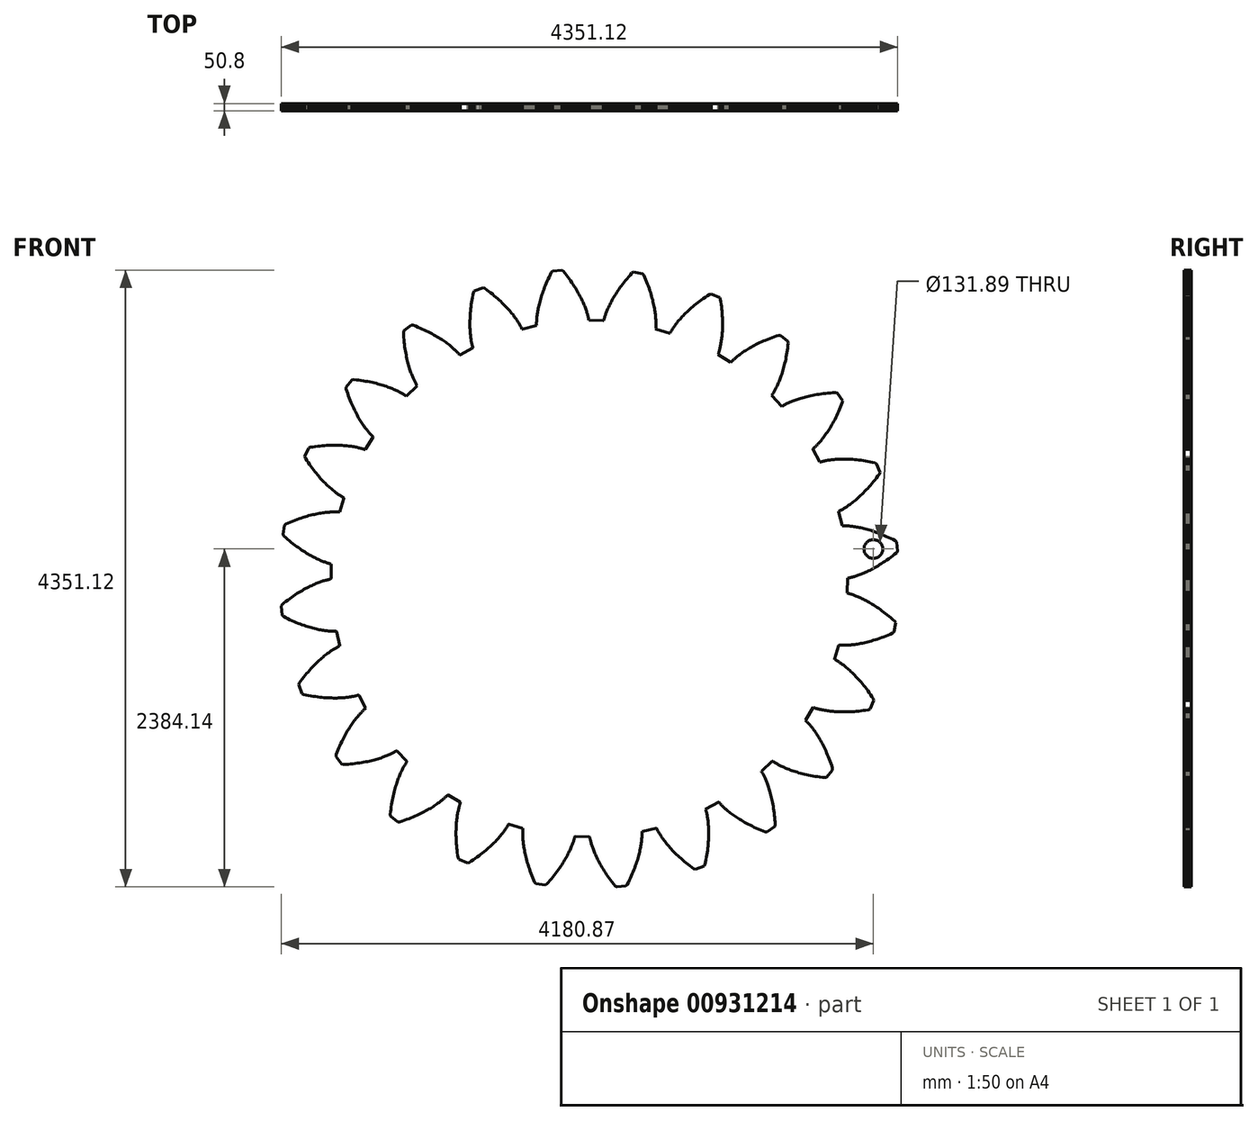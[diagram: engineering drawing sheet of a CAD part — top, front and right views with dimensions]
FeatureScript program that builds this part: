
annotation { "Feature Type Name" : "Feature", "Feature Type Description" : "" }
export const myFeature = defineFeature(function(context is Context, id is Id, definition is map)
    precondition{}
    {
        {
            var Q0;
            Q0=qCreatedBy(makeId("Front.planeOp"),FACE);
            var sketch = newSketch(context, id + "F0", { "sketchPlane" : qUnion([Q0])});
            skLineSegment(sketch, "E0", {"start": v(1823.53, 3.17) * mm, "end": v(1822.91, 0) * mm});
            skLineSegment(sketch, "E1", {"start": v(1822.91, 0) * mm, "end": v(1820.2, -99.34) * mm});
            skLineSegment(sketch, "E2", {"start": v(1820.2, -99.34) * mm, "end": v(1820.65, -102.54) * mm});
            skLineSegment(sketch, "E3", {"start": v(1820.65, -102.54) * mm, "end": v(1825.27, -103.65) * mm});
            skLineSegment(sketch, "E4", {"start": v(1825.27, -103.65) * mm, "end": v(1830.24, -104.93) * mm});
            skLineSegment(sketch, "E5", {"start": v(1830.24, -104.93) * mm, "end": v(1835.55, -106.37) * mm});
            skLineSegment(sketch, "E6", {"start": v(1835.55, -106.37) * mm, "end": v(1841.22, -108) * mm});
            skLineSegment(sketch, "E7", {"start": v(1841.22, -108) * mm, "end": v(1847.22, -109.82) * mm});
            skLineSegment(sketch, "E8", {"start": v(1847.22, -109.82) * mm, "end": v(1853.55, -111.84) * mm});
            skLineSegment(sketch, "E9", {"start": v(1853.55, -111.84) * mm, "end": v(1860.22, -114.08) * mm});
            skLineSegment(sketch, "E10", {"start": v(1860.22, -114.08) * mm, "end": v(1867.2, -116.54) * mm});
            skLineSegment(sketch, "E11", {"start": v(1867.2, -116.54) * mm, "end": v(1874.52, -119.23) * mm});
            skLineSegment(sketch, "E12", {"start": v(1874.52, -119.23) * mm, "end": v(1882.14, -122.16) * mm});
            skLineSegment(sketch, "E13", {"start": v(1882.14, -122.16) * mm, "end": v(1890.08, -125.35) * mm});
            skLineSegment(sketch, "E14", {"start": v(1890.08, -125.35) * mm, "end": v(1898.31, -128.8) * mm});
            skLineSegment(sketch, "E15", {"start": v(1898.31, -128.8) * mm, "end": v(1906.85, -132.52) * mm});
            skLineSegment(sketch, "E16", {"start": v(1906.85, -132.52) * mm, "end": v(1915.67, -136.52) * mm});
            skLineSegment(sketch, "E17", {"start": v(1915.67, -136.52) * mm, "end": v(1924.79, -140.8) * mm});
            skLineSegment(sketch, "E18", {"start": v(1924.79, -140.8) * mm, "end": v(1934.17, -145.4) * mm});
            skLineSegment(sketch, "E19", {"start": v(1934.17, -145.4) * mm, "end": v(1943.83, -150.29) * mm});
            skLineSegment(sketch, "E20", {"start": v(1943.83, -150.29) * mm, "end": v(1953.76, -155.5) * mm});
            skLineSegment(sketch, "E21", {"start": v(1953.76, -155.5) * mm, "end": v(1963.94, -161.04) * mm});
            skLineSegment(sketch, "E22", {"start": v(1963.94, -161.04) * mm, "end": v(1974.37, -166.91) * mm});
            skLineSegment(sketch, "E23", {"start": v(1974.37, -166.91) * mm, "end": v(1985.04, -173.12) * mm});
            skLineSegment(sketch, "E24", {"start": v(1985.04, -173.12) * mm, "end": v(1995.95, -179.69) * mm});
            skLineSegment(sketch, "E25", {"start": v(1995.95, -179.69) * mm, "end": v(2007.08, -186.61) * mm});
            skLineSegment(sketch, "E26", {"start": v(2007.08, -186.61) * mm, "end": v(2018.44, -193.9) * mm});
            skLineSegment(sketch, "E27", {"start": v(2018.44, -193.9) * mm, "end": v(2030, -201.57) * mm});
            skLineSegment(sketch, "E28", {"start": v(2030, -201.57) * mm, "end": v(2041.76, -209.61) * mm});
            skLineSegment(sketch, "E29", {"start": v(2041.76, -209.61) * mm, "end": v(2053.71, -218.05) * mm});
            skLineSegment(sketch, "E30", {"start": v(2053.71, -218.05) * mm, "end": v(2065.85, -226.88) * mm});
            skLineSegment(sketch, "E31", {"start": v(2065.85, -226.88) * mm, "end": v(2078.16, -236.11) * mm});
            skLineSegment(sketch, "E32", {"start": v(2078.16, -236.11) * mm, "end": v(2090.63, -245.76) * mm});
            skLineSegment(sketch, "E33", {"start": v(2090.63, -245.76) * mm, "end": v(2103.27, -255.82) * mm});
            skLineSegment(sketch, "E34", {"start": v(2103.27, -255.82) * mm, "end": v(2116.04, -266.3) * mm});
            skLineSegment(sketch, "E35", {"start": v(2116.04, -266.3) * mm, "end": v(2128.96, -277.23) * mm});
            skLineSegment(sketch, "E36", {"start": v(2128.96, -277.23) * mm, "end": v(2142, -288.58) * mm});
            skLineSegment(sketch, "E37", {"start": v(2142, -288.58) * mm, "end": v(2155.16, -300.37) * mm});
            skLineSegment(sketch, "E38", {"start": v(2155.16, -300.37) * mm, "end": v(2161.79, -311.66) * mm});
            skLineSegment(sketch, "E39", {"start": v(2161.79, -311.66) * mm, "end": v(2151.48, -376.27) * mm});
            skLineSegment(sketch, "E40", {"start": v(2151.48, -376.27) * mm, "end": v(2141.67, -384.94) * mm});
            skLineSegment(sketch, "E41", {"start": v(2141.67, -384.94) * mm, "end": v(2125.5, -392.05) * mm});
            skLineSegment(sketch, "E42", {"start": v(2125.5, -392.05) * mm, "end": v(2109.57, -398.79) * mm});
            skLineSegment(sketch, "E43", {"start": v(2109.57, -398.79) * mm, "end": v(2093.9, -405.14) * mm});
            skLineSegment(sketch, "E44", {"start": v(2093.9, -405.14) * mm, "end": v(2078.5, -411.14) * mm});
            skLineSegment(sketch, "E45", {"start": v(2078.5, -411.14) * mm, "end": v(2063.36, -416.77) * mm});
            skLineSegment(sketch, "E46", {"start": v(2063.36, -416.77) * mm, "end": v(2048.5, -422.06) * mm});
            skLineSegment(sketch, "E47", {"start": v(2048.5, -422.06) * mm, "end": v(2033.93, -427) * mm});
            skLineSegment(sketch, "E48", {"start": v(2033.93, -427) * mm, "end": v(2019.65, -431.62) * mm});
            skLineSegment(sketch, "E49", {"start": v(2019.65, -431.62) * mm, "end": v(2005.66, -435.92) * mm});
            skLineSegment(sketch, "E50", {"start": v(2005.66, -435.92) * mm, "end": v(1991.98, -439.9) * mm});
            skLineSegment(sketch, "E51", {"start": v(1991.98, -439.9) * mm, "end": v(1978.61, -443.6) * mm});
            skLineSegment(sketch, "E52", {"start": v(1978.61, -443.6) * mm, "end": v(1965.56, -447) * mm});
            skLineSegment(sketch, "E53", {"start": v(1965.56, -447) * mm, "end": v(1952.82, -450.1) * mm});
            skLineSegment(sketch, "E54", {"start": v(1952.82, -450.1) * mm, "end": v(1940.41, -452.96) * mm});
            skLineSegment(sketch, "E55", {"start": v(1940.41, -452.96) * mm, "end": v(1928.34, -455.54) * mm});
            skLineSegment(sketch, "E56", {"start": v(1928.34, -455.54) * mm, "end": v(1916.6, -457.88) * mm});
            skLineSegment(sketch, "E57", {"start": v(1916.6, -457.88) * mm, "end": v(1905.2, -459.97) * mm});
            skLineSegment(sketch, "E58", {"start": v(1905.2, -459.97) * mm, "end": v(1894.14, -461.84) * mm});
            skLineSegment(sketch, "E59", {"start": v(1894.14, -461.84) * mm, "end": v(1883.44, -463.49) * mm});
            skLineSegment(sketch, "E60", {"start": v(1883.44, -463.49) * mm, "end": v(1873.1, -464.93) * mm});
            skLineSegment(sketch, "E61", {"start": v(1873.1, -464.93) * mm, "end": v(1863.1, -466.17) * mm});
            skLineSegment(sketch, "E62", {"start": v(1863.1, -466.17) * mm, "end": v(1853.46, -467.22) * mm});
            skLineSegment(sketch, "E63", {"start": v(1853.46, -467.22) * mm, "end": v(1844.2, -468.1) * mm});
            skLineSegment(sketch, "E64", {"start": v(1844.2, -468.1) * mm, "end": v(1835.3, -468.82) * mm});
            skLineSegment(sketch, "E65", {"start": v(1835.3, -468.82) * mm, "end": v(1826.76, -469.38) * mm});
            skLineSegment(sketch, "E66", {"start": v(1826.76, -469.38) * mm, "end": v(1818.6, -469.8) * mm});
            skLineSegment(sketch, "E67", {"start": v(1818.6, -469.8) * mm, "end": v(1810.82, -470.08) * mm});
            skLineSegment(sketch, "E68", {"start": v(1810.82, -470.08) * mm, "end": v(1803.41, -470.24) * mm});
            skLineSegment(sketch, "E69", {"start": v(1803.41, -470.24) * mm, "end": v(1796.38, -470.3) * mm});
            skLineSegment(sketch, "E70", {"start": v(1796.38, -470.3) * mm, "end": v(1789.73, -470.24) * mm});
            skLineSegment(sketch, "E71", {"start": v(1789.73, -470.24) * mm, "end": v(1783.46, -470.1) * mm});
            skLineSegment(sketch, "E72", {"start": v(1783.46, -470.1) * mm, "end": v(1777.58, -469.9) * mm});
            skLineSegment(sketch, "E73", {"start": v(1777.58, -469.9) * mm, "end": v(1772.07, -469.61) * mm});
            skLineSegment(sketch, "E74", {"start": v(1772.07, -469.61) * mm, "end": v(1766.95, -469.28) * mm});
            skLineSegment(sketch, "E75", {"start": v(1766.95, -469.28) * mm, "end": v(1762.22, -468.9) * mm});
            skLineSegment(sketch, "E76", {"start": v(1762.22, -468.9) * mm, "end": v(1760.8, -471.8) * mm});
            skLineSegment(sketch, "E77", {"start": v(1760.8, -471.8) * mm, "end": v(1732.47, -567.06) * mm});
            skLineSegment(sketch, "E78", {"start": v(1732.47, -567.06) * mm, "end": v(1732.07, -570.26) * mm});
            skLineSegment(sketch, "E79", {"start": v(1732.07, -570.26) * mm, "end": v(1736.25, -572.54) * mm});
            skLineSegment(sketch, "E80", {"start": v(1736.25, -572.54) * mm, "end": v(1740.72, -575.05) * mm});
            skLineSegment(sketch, "E81", {"start": v(1740.72, -575.05) * mm, "end": v(1745.48, -577.82) * mm});
            skLineSegment(sketch, "E82", {"start": v(1745.48, -577.82) * mm, "end": v(1750.52, -580.86) * mm});
            skLineSegment(sketch, "E83", {"start": v(1750.52, -580.86) * mm, "end": v(1755.85, -584.17) * mm});
            skLineSegment(sketch, "E84", {"start": v(1755.85, -584.17) * mm, "end": v(1761.44, -587.77) * mm});
            skLineSegment(sketch, "E85", {"start": v(1761.44, -587.77) * mm, "end": v(1767.3, -591.65) * mm});
            skLineSegment(sketch, "E86", {"start": v(1767.3, -591.65) * mm, "end": v(1773.42, -595.84) * mm});
            skLineSegment(sketch, "E87", {"start": v(1773.42, -595.84) * mm, "end": v(1779.78, -600.33) * mm});
            skLineSegment(sketch, "E88", {"start": v(1779.78, -600.33) * mm, "end": v(1786.4, -605.13) * mm});
            skLineSegment(sketch, "E89", {"start": v(1786.4, -605.13) * mm, "end": v(1793.23, -610.27) * mm});
            skLineSegment(sketch, "E90", {"start": v(1793.23, -610.27) * mm, "end": v(1800.3, -615.73) * mm});
            skLineSegment(sketch, "E91", {"start": v(1800.3, -615.73) * mm, "end": v(1807.58, -621.53) * mm});
            skLineSegment(sketch, "E92", {"start": v(1807.58, -621.53) * mm, "end": v(1815.07, -627.68) * mm});
            skLineSegment(sketch, "E93", {"start": v(1815.07, -627.68) * mm, "end": v(1822.76, -634.18) * mm});
            skLineSegment(sketch, "E94", {"start": v(1822.76, -634.18) * mm, "end": v(1830.64, -641.04) * mm});
            skLineSegment(sketch, "E95", {"start": v(1830.64, -641.04) * mm, "end": v(1838.7, -648.27) * mm});
            skLineSegment(sketch, "E96", {"start": v(1838.7, -648.27) * mm, "end": v(1846.94, -655.87) * mm});
            skLineSegment(sketch, "E97", {"start": v(1846.94, -655.87) * mm, "end": v(1855.34, -663.86) * mm});
            skLineSegment(sketch, "E98", {"start": v(1855.34, -663.86) * mm, "end": v(1863.9, -672.23) * mm});
            skLineSegment(sketch, "E99", {"start": v(1863.9, -672.23) * mm, "end": v(1872.6, -681) * mm});
            skLineSegment(sketch, "E100", {"start": v(1872.6, -681) * mm, "end": v(1881.43, -690.16) * mm});
            skLineSegment(sketch, "E101", {"start": v(1881.43, -690.16) * mm, "end": v(1890.4, -699.73) * mm});
            skLineSegment(sketch, "E102", {"start": v(1890.4, -699.73) * mm, "end": v(1899.47, -709.7) * mm});
            skLineSegment(sketch, "E103", {"start": v(1899.47, -709.7) * mm, "end": v(1908.66, -720.1) * mm});
            skLineSegment(sketch, "E104", {"start": v(1908.66, -720.1) * mm, "end": v(1917.93, -730.91) * mm});
            skLineSegment(sketch, "E105", {"start": v(1917.93, -730.91) * mm, "end": v(1927.3, -742.16) * mm});
            skLineSegment(sketch, "E106", {"start": v(1927.3, -742.16) * mm, "end": v(1936.74, -753.83) * mm});
            skLineSegment(sketch, "E107", {"start": v(1936.74, -753.83) * mm, "end": v(1946.24, -765.94) * mm});
            skLineSegment(sketch, "E108", {"start": v(1946.24, -765.94) * mm, "end": v(1955.8, -778.48) * mm});
            skLineSegment(sketch, "E109", {"start": v(1955.8, -778.48) * mm, "end": v(1965.39, -791.47) * mm});
            skLineSegment(sketch, "E110", {"start": v(1965.39, -791.47) * mm, "end": v(1975.02, -804.9) * mm});
            skLineSegment(sketch, "E111", {"start": v(1975.02, -804.9) * mm, "end": v(1984.66, -818.8) * mm});
            skLineSegment(sketch, "E112", {"start": v(1984.66, -818.8) * mm, "end": v(1994.32, -833.14) * mm});
            skLineSegment(sketch, "E113", {"start": v(1994.32, -833.14) * mm, "end": v(2003.98, -847.93) * mm});
            skLineSegment(sketch, "E114", {"start": v(2003.98, -847.93) * mm, "end": v(2007.46, -860.55) * mm});
            skLineSegment(sketch, "E115", {"start": v(2007.46, -860.55) * mm, "end": v(1980.78, -920.3) * mm});
            skLineSegment(sketch, "E116", {"start": v(1980.78, -920.3) * mm, "end": v(1969.07, -926.12) * mm});
            skLineSegment(sketch, "E117", {"start": v(1969.07, -926.12) * mm, "end": v(1951.6, -928.81) * mm});
            skLineSegment(sketch, "E118", {"start": v(1951.6, -928.81) * mm, "end": v(1934.48, -931.2) * mm});
            skLineSegment(sketch, "E119", {"start": v(1934.48, -931.2) * mm, "end": v(1917.7, -933.28) * mm});
            skLineSegment(sketch, "E120", {"start": v(1917.7, -933.28) * mm, "end": v(1901.26, -935.08) * mm});
            skLineSegment(sketch, "E121", {"start": v(1901.26, -935.08) * mm, "end": v(1885.19, -936.6) * mm});
            skLineSegment(sketch, "E122", {"start": v(1885.19, -936.6) * mm, "end": v(1869.47, -937.87) * mm});
            skLineSegment(sketch, "E123", {"start": v(1869.47, -937.87) * mm, "end": v(1854.1, -938.87) * mm});
            skLineSegment(sketch, "E124", {"start": v(1854.1, -938.87) * mm, "end": v(1839.12, -939.64) * mm});
            skLineSegment(sketch, "E125", {"start": v(1839.12, -939.64) * mm, "end": v(1824.5, -940.17) * mm});
            skLineSegment(sketch, "E126", {"start": v(1824.5, -940.17) * mm, "end": v(1810.25, -940.48) * mm});
            skLineSegment(sketch, "E127", {"start": v(1810.25, -940.48) * mm, "end": v(1796.38, -940.58) * mm});
            skLineSegment(sketch, "E128", {"start": v(1796.38, -940.58) * mm, "end": v(1782.9, -940.48) * mm});
            skLineSegment(sketch, "E129", {"start": v(1782.9, -940.48) * mm, "end": v(1769.78, -940.2) * mm});
            skLineSegment(sketch, "E130", {"start": v(1769.78, -940.2) * mm, "end": v(1757.06, -939.74) * mm});
            skLineSegment(sketch, "E131", {"start": v(1757.06, -939.74) * mm, "end": v(1744.73, -939.1) * mm});
            skLineSegment(sketch, "E132", {"start": v(1744.73, -939.1) * mm, "end": v(1732.78, -938.33) * mm});
            skLineSegment(sketch, "E133", {"start": v(1732.78, -938.33) * mm, "end": v(1721.23, -937.4) * mm});
            skLineSegment(sketch, "E134", {"start": v(1721.23, -937.4) * mm, "end": v(1710.07, -936.34) * mm});
            skLineSegment(sketch, "E135", {"start": v(1710.07, -936.34) * mm, "end": v(1699.3, -935.16) * mm});
            skLineSegment(sketch, "E136", {"start": v(1699.3, -935.16) * mm, "end": v(1688.93, -933.88) * mm});
            skLineSegment(sketch, "E137", {"start": v(1688.93, -933.88) * mm, "end": v(1678.96, -932.5) * mm});
            skLineSegment(sketch, "E138", {"start": v(1678.96, -932.5) * mm, "end": v(1669.38, -931.02) * mm});
            skLineSegment(sketch, "E139", {"start": v(1669.38, -931.02) * mm, "end": v(1660.2, -929.47) * mm});
            skLineSegment(sketch, "E140", {"start": v(1660.2, -929.47) * mm, "end": v(1651.42, -927.85) * mm});
            skLineSegment(sketch, "E141", {"start": v(1651.42, -927.85) * mm, "end": v(1643.03, -926.18) * mm});
            skLineSegment(sketch, "E142", {"start": v(1643.03, -926.18) * mm, "end": v(1635.04, -924.48) * mm});
            skLineSegment(sketch, "E143", {"start": v(1635.04, -924.48) * mm, "end": v(1627.45, -922.73) * mm});
            skLineSegment(sketch, "E144", {"start": v(1627.45, -922.73) * mm, "end": v(1620.25, -920.97) * mm});
            skLineSegment(sketch, "E145", {"start": v(1620.25, -920.97) * mm, "end": v(1613.45, -919.2) * mm});
            skLineSegment(sketch, "E146", {"start": v(1613.45, -919.2) * mm, "end": v(1607.04, -917.44) * mm});
            skLineSegment(sketch, "E147", {"start": v(1607.04, -917.44) * mm, "end": v(1601.02, -915.68) * mm});
            skLineSegment(sketch, "E148", {"start": v(1601.02, -915.68) * mm, "end": v(1595.39, -913.95) * mm});
            skLineSegment(sketch, "E149", {"start": v(1595.39, -913.95) * mm, "end": v(1590.15, -912.26) * mm});
            skLineSegment(sketch, "E150", {"start": v(1590.15, -912.26) * mm, "end": v(1585.29, -910.6) * mm});
            skLineSegment(sketch, "E151", {"start": v(1585.29, -910.6) * mm, "end": v(1580.81, -909.02) * mm});
            skLineSegment(sketch, "E152", {"start": v(1580.81, -909.02) * mm, "end": v(1578.69, -911.46) * mm});
            skLineSegment(sketch, "E153", {"start": v(1578.69, -911.46) * mm, "end": v(1526.67, -996.13) * mm});
            skLineSegment(sketch, "E154", {"start": v(1526.67, -996.13) * mm, "end": v(1525.46, -999.13) * mm});
            skLineSegment(sketch, "E155", {"start": v(1525.46, -999.13) * mm, "end": v(1528.9, -1002.4) * mm});
            skLineSegment(sketch, "E156", {"start": v(1528.9, -1002.4) * mm, "end": v(1532.57, -1005.99) * mm});
            skLineSegment(sketch, "E157", {"start": v(1532.57, -1005.99) * mm, "end": v(1536.45, -1009.9) * mm});
            skLineSegment(sketch, "E158", {"start": v(1536.45, -1009.9) * mm, "end": v(1540.54, -1014.14) * mm});
            skLineSegment(sketch, "E159", {"start": v(1540.54, -1014.14) * mm, "end": v(1544.82, -1018.72) * mm});
            skLineSegment(sketch, "E160", {"start": v(1544.82, -1018.72) * mm, "end": v(1549.3, -1023.63) * mm});
            skLineSegment(sketch, "E161", {"start": v(1549.3, -1023.63) * mm, "end": v(1553.95, -1028.9) * mm});
            skLineSegment(sketch, "E162", {"start": v(1553.95, -1028.9) * mm, "end": v(1558.78, -1034.53) * mm});
            skLineSegment(sketch, "E163", {"start": v(1558.78, -1034.53) * mm, "end": v(1563.76, -1040.51) * mm});
            skLineSegment(sketch, "E164", {"start": v(1563.76, -1040.51) * mm, "end": v(1568.9, -1046.87) * mm});
            skLineSegment(sketch, "E165", {"start": v(1568.9, -1046.87) * mm, "end": v(1574.18, -1053.6) * mm});
            skLineSegment(sketch, "E166", {"start": v(1574.18, -1053.6) * mm, "end": v(1579.59, -1060.7) * mm});
            skLineSegment(sketch, "E167", {"start": v(1579.59, -1060.7) * mm, "end": v(1585.12, -1068.19) * mm});
            skLineSegment(sketch, "E168", {"start": v(1585.12, -1068.19) * mm, "end": v(1590.76, -1076.06) * mm});
            skLineSegment(sketch, "E169", {"start": v(1590.76, -1076.06) * mm, "end": v(1596.51, -1084.33) * mm});
            skLineSegment(sketch, "E170", {"start": v(1596.51, -1084.33) * mm, "end": v(1602.35, -1093) * mm});
            skLineSegment(sketch, "E171", {"start": v(1602.35, -1093) * mm, "end": v(1608.27, -1102.07) * mm});
            skLineSegment(sketch, "E172", {"start": v(1608.27, -1102.07) * mm, "end": v(1614.25, -1111.55) * mm});
            skLineSegment(sketch, "E173", {"start": v(1614.25, -1111.55) * mm, "end": v(1620.3, -1121.43) * mm});
            skLineSegment(sketch, "E174", {"start": v(1620.3, -1121.43) * mm, "end": v(1626.4, -1131.73) * mm});
            skLineSegment(sketch, "E175", {"start": v(1626.4, -1131.73) * mm, "end": v(1632.54, -1142.45) * mm});
            skLineSegment(sketch, "E176", {"start": v(1632.54, -1142.45) * mm, "end": v(1638.7, -1153.6) * mm});
            skLineSegment(sketch, "E177", {"start": v(1638.7, -1153.6) * mm, "end": v(1644.88, -1165.15) * mm});
            skLineSegment(sketch, "E178", {"start": v(1644.88, -1165.15) * mm, "end": v(1651.07, -1177.14) * mm});
            skLineSegment(sketch, "E179", {"start": v(1651.07, -1177.14) * mm, "end": v(1657.24, -1189.56) * mm});
            skLineSegment(sketch, "E180", {"start": v(1657.24, -1189.56) * mm, "end": v(1663.4, -1202.4) * mm});
            skLineSegment(sketch, "E181", {"start": v(1663.4, -1202.4) * mm, "end": v(1669.54, -1215.69) * mm});
            skLineSegment(sketch, "E182", {"start": v(1669.54, -1215.69) * mm, "end": v(1675.64, -1229.4) * mm});
            skLineSegment(sketch, "E183", {"start": v(1675.64, -1229.4) * mm, "end": v(1681.68, -1243.56) * mm});
            skLineSegment(sketch, "E184", {"start": v(1681.68, -1243.56) * mm, "end": v(1687.66, -1258.15) * mm});
            skLineSegment(sketch, "E185", {"start": v(1687.66, -1258.15) * mm, "end": v(1693.57, -1273.18) * mm});
            skLineSegment(sketch, "E186", {"start": v(1693.57, -1273.18) * mm, "end": v(1699.4, -1288.65) * mm});
            skLineSegment(sketch, "E187", {"start": v(1699.4, -1288.65) * mm, "end": v(1705.12, -1304.56) * mm});
            skLineSegment(sketch, "E188", {"start": v(1705.12, -1304.56) * mm, "end": v(1710.74, -1320.92) * mm});
            skLineSegment(sketch, "E189", {"start": v(1710.74, -1320.92) * mm, "end": v(1716.23, -1337.7) * mm});
            skLineSegment(sketch, "E190", {"start": v(1716.23, -1337.7) * mm, "end": v(1716.33, -1350.8) * mm});
            skLineSegment(sketch, "E191", {"start": v(1716.33, -1350.8) * mm, "end": v(1675.1, -1401.6) * mm});
            skLineSegment(sketch, "E192", {"start": v(1675.1, -1401.6) * mm, "end": v(1662.27, -1404.2) * mm});
            skLineSegment(sketch, "E193", {"start": v(1662.27, -1404.2) * mm, "end": v(1644.7, -1402.28) * mm});
            skLineSegment(sketch, "E194", {"start": v(1644.7, -1402.28) * mm, "end": v(1627.55, -1400.14) * mm});
            skLineSegment(sketch, "E195", {"start": v(1627.55, -1400.14) * mm, "end": v(1610.8, -1397.82) * mm});
            skLineSegment(sketch, "E196", {"start": v(1610.8, -1397.82) * mm, "end": v(1594.46, -1395.3) * mm});
            skLineSegment(sketch, "E197", {"start": v(1594.46, -1395.3) * mm, "end": v(1578.54, -1392.61) * mm});
            skLineSegment(sketch, "E198", {"start": v(1578.54, -1392.61) * mm, "end": v(1563.03, -1389.76) * mm});
            skLineSegment(sketch, "E199", {"start": v(1563.03, -1389.76) * mm, "end": v(1547.93, -1386.76) * mm});
            skLineSegment(sketch, "E200", {"start": v(1547.93, -1386.76) * mm, "end": v(1533.25, -1383.62) * mm});
            skLineSegment(sketch, "E201", {"start": v(1533.25, -1383.62) * mm, "end": v(1519, -1380.35) * mm});
            skLineSegment(sketch, "E202", {"start": v(1519, -1380.35) * mm, "end": v(1505.15, -1376.96) * mm});
            skLineSegment(sketch, "E203", {"start": v(1505.15, -1376.96) * mm, "end": v(1491.73, -1373.47) * mm});
            skLineSegment(sketch, "E204", {"start": v(1491.73, -1373.47) * mm, "end": v(1478.72, -1369.89) * mm});
            skLineSegment(sketch, "E205", {"start": v(1478.72, -1369.89) * mm, "end": v(1466.14, -1366.22) * mm});
            skLineSegment(sketch, "E206", {"start": v(1466.14, -1366.22) * mm, "end": v(1453.97, -1362.48) * mm});
            skLineSegment(sketch, "E207", {"start": v(1453.97, -1362.48) * mm, "end": v(1442.22, -1358.68) * mm});
            skLineSegment(sketch, "E208", {"start": v(1442.22, -1358.68) * mm, "end": v(1430.88, -1354.83) * mm});
            skLineSegment(sketch, "E209", {"start": v(1430.88, -1354.83) * mm, "end": v(1419.96, -1350.95) * mm});
            skLineSegment(sketch, "E210", {"start": v(1419.96, -1350.95) * mm, "end": v(1409.46, -1347.04) * mm});
            skLineSegment(sketch, "E211", {"start": v(1409.46, -1347.04) * mm, "end": v(1399.36, -1343.11) * mm});
            skLineSegment(sketch, "E212", {"start": v(1399.36, -1343.11) * mm, "end": v(1389.68, -1339.18) * mm});
            skLineSegment(sketch, "E213", {"start": v(1389.68, -1339.18) * mm, "end": v(1380.4, -1335.26) * mm});
            skLineSegment(sketch, "E214", {"start": v(1380.4, -1335.26) * mm, "end": v(1371.53, -1331.36) * mm});
            skLineSegment(sketch, "E215", {"start": v(1371.53, -1331.36) * mm, "end": v(1363.07, -1327.49) * mm});
            skLineSegment(sketch, "E216", {"start": v(1363.07, -1327.49) * mm, "end": v(1355, -1323.66) * mm});
            skLineSegment(sketch, "E217", {"start": v(1355, -1323.66) * mm, "end": v(1347.33, -1319.87) * mm});
            skLineSegment(sketch, "E218", {"start": v(1347.33, -1319.87) * mm, "end": v(1340.06, -1316.16) * mm});
            skLineSegment(sketch, "E219", {"start": v(1340.06, -1316.16) * mm, "end": v(1333.18, -1312.5) * mm});
            skLineSegment(sketch, "E220", {"start": v(1333.18, -1312.5) * mm, "end": v(1326.68, -1308.94) * mm});
            skLineSegment(sketch, "E221", {"start": v(1326.68, -1308.94) * mm, "end": v(1320.57, -1305.47) * mm});
            skLineSegment(sketch, "E222", {"start": v(1320.57, -1305.47) * mm, "end": v(1314.83, -1302.1) * mm});
            skLineSegment(sketch, "E223", {"start": v(1314.83, -1302.1) * mm, "end": v(1309.47, -1298.86) * mm});
            skLineSegment(sketch, "E224", {"start": v(1309.47, -1298.86) * mm, "end": v(1304.48, -1295.73) * mm});
            skLineSegment(sketch, "E225", {"start": v(1304.48, -1295.73) * mm, "end": v(1299.85, -1292.73) * mm});
            skLineSegment(sketch, "E226", {"start": v(1299.85, -1292.73) * mm, "end": v(1295.59, -1289.88) * mm});
            skLineSegment(sketch, "E227", {"start": v(1295.59, -1289.88) * mm, "end": v(1291.68, -1287.19) * mm});
            skLineSegment(sketch, "E228", {"start": v(1291.68, -1287.19) * mm, "end": v(1289, -1289) * mm});
            skLineSegment(sketch, "E229", {"start": v(1289, -1289) * mm, "end": v(1216.84, -1357.32) * mm});
            skLineSegment(sketch, "E230", {"start": v(1216.84, -1357.32) * mm, "end": v(1214.89, -1359.9) * mm});
            skLineSegment(sketch, "E231", {"start": v(1214.89, -1359.9) * mm, "end": v(1217.37, -1363.95) * mm});
            skLineSegment(sketch, "E232", {"start": v(1217.37, -1363.95) * mm, "end": v(1219.98, -1368.37) * mm});
            skLineSegment(sketch, "E233", {"start": v(1219.98, -1368.37) * mm, "end": v(1222.72, -1373.15) * mm});
            skLineSegment(sketch, "E234", {"start": v(1222.72, -1373.15) * mm, "end": v(1225.57, -1378.3) * mm});
            skLineSegment(sketch, "E235", {"start": v(1225.57, -1378.3) * mm, "end": v(1228.52, -1383.83) * mm});
            skLineSegment(sketch, "E236", {"start": v(1228.52, -1383.83) * mm, "end": v(1231.57, -1389.74) * mm});
            skLineSegment(sketch, "E237", {"start": v(1231.57, -1389.74) * mm, "end": v(1234.7, -1396.04) * mm});
            skLineSegment(sketch, "E238", {"start": v(1234.7, -1396.04) * mm, "end": v(1237.9, -1402.72) * mm});
            skLineSegment(sketch, "E239", {"start": v(1237.9, -1402.72) * mm, "end": v(1241.17, -1409.8) * mm});
            skLineSegment(sketch, "E240", {"start": v(1241.17, -1409.8) * mm, "end": v(1244.5, -1417.26) * mm});
            skLineSegment(sketch, "E241", {"start": v(1244.5, -1417.26) * mm, "end": v(1247.85, -1425.12) * mm});
            skLineSegment(sketch, "E242", {"start": v(1247.85, -1425.12) * mm, "end": v(1251.24, -1433.38) * mm});
            skLineSegment(sketch, "E243", {"start": v(1251.24, -1433.38) * mm, "end": v(1254.64, -1442.05) * mm});
            skLineSegment(sketch, "E244", {"start": v(1254.64, -1442.05) * mm, "end": v(1258.06, -1451.12) * mm});
            skLineSegment(sketch, "E245", {"start": v(1258.06, -1451.12) * mm, "end": v(1261.47, -1460.6) * mm});
            skLineSegment(sketch, "E246", {"start": v(1261.47, -1460.6) * mm, "end": v(1264.86, -1470.48) * mm});
            skLineSegment(sketch, "E247", {"start": v(1264.86, -1470.48) * mm, "end": v(1268.23, -1480.77) * mm});
            skLineSegment(sketch, "E248", {"start": v(1268.23, -1480.77) * mm, "end": v(1271.56, -1491.47) * mm});
            skLineSegment(sketch, "E249", {"start": v(1271.56, -1491.47) * mm, "end": v(1274.84, -1502.59) * mm});
            skLineSegment(sketch, "E250", {"start": v(1274.84, -1502.59) * mm, "end": v(1278.07, -1514.11) * mm});
            skLineSegment(sketch, "E251", {"start": v(1278.07, -1514.11) * mm, "end": v(1281.22, -1526.06) * mm});
            skLineSegment(sketch, "E252", {"start": v(1281.22, -1526.06) * mm, "end": v(1284.3, -1538.41) * mm});
            skLineSegment(sketch, "E253", {"start": v(1284.3, -1538.41) * mm, "end": v(1287.27, -1551.18) * mm});
            skLineSegment(sketch, "E254", {"start": v(1287.27, -1551.18) * mm, "end": v(1290.14, -1564.36) * mm});
            skLineSegment(sketch, "E255", {"start": v(1290.14, -1564.36) * mm, "end": v(1292.9, -1577.95) * mm});
            skLineSegment(sketch, "E256", {"start": v(1292.9, -1577.95) * mm, "end": v(1295.52, -1591.96) * mm});
            skLineSegment(sketch, "E257", {"start": v(1295.52, -1591.96) * mm, "end": v(1298.01, -1606.38) * mm});
            skLineSegment(sketch, "E258", {"start": v(1298.01, -1606.38) * mm, "end": v(1300.35, -1621.2) * mm});
            skLineSegment(sketch, "E259", {"start": v(1300.35, -1621.2) * mm, "end": v(1302.52, -1636.44) * mm});
            skLineSegment(sketch, "E260", {"start": v(1302.52, -1636.44) * mm, "end": v(1304.52, -1652.08) * mm});
            skLineSegment(sketch, "E261", {"start": v(1304.52, -1652.08) * mm, "end": v(1306.34, -1668.13) * mm});
            skLineSegment(sketch, "E262", {"start": v(1306.34, -1668.13) * mm, "end": v(1307.96, -1684.58) * mm});
            skLineSegment(sketch, "E263", {"start": v(1307.96, -1684.58) * mm, "end": v(1309.37, -1701.43) * mm});
            skLineSegment(sketch, "E264", {"start": v(1309.37, -1701.43) * mm, "end": v(1310.57, -1718.68) * mm});
            skLineSegment(sketch, "E265", {"start": v(1310.57, -1718.68) * mm, "end": v(1311.53, -1736.32) * mm});
            skLineSegment(sketch, "E266", {"start": v(1311.53, -1736.32) * mm, "end": v(1308.24, -1748.99) * mm});
            skLineSegment(sketch, "E267", {"start": v(1308.24, -1748.99) * mm, "end": v(1255.26, -1787.4) * mm});
            skLineSegment(sketch, "E268", {"start": v(1255.26, -1787.4) * mm, "end": v(1242.2, -1786.58) * mm});
            skLineSegment(sketch, "E269", {"start": v(1242.2, -1786.58) * mm, "end": v(1225.73, -1780.18) * mm});
            skLineSegment(sketch, "E270", {"start": v(1225.73, -1780.18) * mm, "end": v(1209.7, -1773.68) * mm});
            skLineSegment(sketch, "E271", {"start": v(1209.7, -1773.68) * mm, "end": v(1194.13, -1767.1) * mm});
            skLineSegment(sketch, "E272", {"start": v(1194.13, -1767.1) * mm, "end": v(1179, -1760.44) * mm});
            skLineSegment(sketch, "E273", {"start": v(1179, -1760.44) * mm, "end": v(1164.31, -1753.72) * mm});
            skLineSegment(sketch, "E274", {"start": v(1164.31, -1753.72) * mm, "end": v(1150.07, -1746.95) * mm});
            skLineSegment(sketch, "E275", {"start": v(1150.07, -1746.95) * mm, "end": v(1136.27, -1740.14) * mm});
            skLineSegment(sketch, "E276", {"start": v(1136.27, -1740.14) * mm, "end": v(1122.9, -1733.3) * mm});
            skLineSegment(sketch, "E277", {"start": v(1122.9, -1733.3) * mm, "end": v(1109.98, -1726.46) * mm});
            skLineSegment(sketch, "E278", {"start": v(1109.98, -1726.46) * mm, "end": v(1097.48, -1719.6) * mm});
            skLineSegment(sketch, "E279", {"start": v(1097.48, -1719.6) * mm, "end": v(1085.42, -1712.76) * mm});
            skLineSegment(sketch, "E280", {"start": v(1085.42, -1712.76) * mm, "end": v(1073.79, -1705.93) * mm});
            skLineSegment(sketch, "E281", {"start": v(1073.79, -1705.93) * mm, "end": v(1062.58, -1699.13) * mm});
            skLineSegment(sketch, "E282", {"start": v(1062.58, -1699.13) * mm, "end": v(1051.8, -1692.37) * mm});
            skLineSegment(sketch, "E283", {"start": v(1051.8, -1692.37) * mm, "end": v(1041.42, -1685.66) * mm});
            skLineSegment(sketch, "E284", {"start": v(1041.42, -1685.66) * mm, "end": v(1031.47, -1679) * mm});
            skLineSegment(sketch, "E285", {"start": v(1031.47, -1679) * mm, "end": v(1021.93, -1672.43) * mm});
            skLineSegment(sketch, "E286", {"start": v(1021.93, -1672.43) * mm, "end": v(1012.8, -1665.93) * mm});
            skLineSegment(sketch, "E287", {"start": v(1012.8, -1665.93) * mm, "end": v(1004.06, -1659.53) * mm});
            skLineSegment(sketch, "E288", {"start": v(1004.06, -1659.53) * mm, "end": v(995.72, -1653.23) * mm});
            skLineSegment(sketch, "E289", {"start": v(995.72, -1653.23) * mm, "end": v(987.78, -1647.04) * mm});
            skLineSegment(sketch, "E290", {"start": v(987.78, -1647.04) * mm, "end": v(980.22, -1640.98) * mm});
            skLineSegment(sketch, "E291", {"start": v(980.22, -1640.98) * mm, "end": v(973.04, -1635.04) * mm});
            skLineSegment(sketch, "E292", {"start": v(973.04, -1635.04) * mm, "end": v(966.24, -1629.25) * mm});
            skLineSegment(sketch, "E293", {"start": v(966.24, -1629.25) * mm, "end": v(959.82, -1623.62) * mm});
            skLineSegment(sketch, "E294", {"start": v(959.82, -1623.62) * mm, "end": v(953.75, -1618.14) * mm});
            skLineSegment(sketch, "E295", {"start": v(953.75, -1618.14) * mm, "end": v(948.05, -1612.84) * mm});
            skLineSegment(sketch, "E296", {"start": v(948.05, -1612.84) * mm, "end": v(942.7, -1607.71) * mm});
            skLineSegment(sketch, "E297", {"start": v(942.7, -1607.71) * mm, "end": v(937.69, -1602.78) * mm});
            skLineSegment(sketch, "E298", {"start": v(937.69, -1602.78) * mm, "end": v(933.02, -1598.04) * mm});
            skLineSegment(sketch, "E299", {"start": v(933.02, -1598.04) * mm, "end": v(928.68, -1593.51) * mm});
            skLineSegment(sketch, "E300", {"start": v(928.68, -1593.51) * mm, "end": v(924.67, -1589.2) * mm});
            skLineSegment(sketch, "E301", {"start": v(924.67, -1589.2) * mm, "end": v(920.98, -1585.11) * mm});
            skLineSegment(sketch, "E302", {"start": v(920.98, -1585.11) * mm, "end": v(917.6, -1581.25) * mm});
            skLineSegment(sketch, "E303", {"start": v(917.6, -1581.25) * mm, "end": v(914.51, -1577.64) * mm});
            skLineSegment(sketch, "E304", {"start": v(914.51, -1577.64) * mm, "end": v(911.46, -1578.69) * mm});
            skLineSegment(sketch, "E305", {"start": v(911.46, -1578.69) * mm, "end": v(824.07, -1626.01) * mm});
            skLineSegment(sketch, "E306", {"start": v(824.07, -1626.01) * mm, "end": v(821.52, -1628) * mm});
            skLineSegment(sketch, "E307", {"start": v(821.52, -1628) * mm, "end": v(822.87, -1632.56) * mm});
            skLineSegment(sketch, "E308", {"start": v(822.87, -1632.56) * mm, "end": v(824.25, -1637.5) * mm});
            skLineSegment(sketch, "E309", {"start": v(824.25, -1637.5) * mm, "end": v(825.66, -1642.82) * mm});
            skLineSegment(sketch, "E310", {"start": v(825.66, -1642.82) * mm, "end": v(827.08, -1648.54) * mm});
            skLineSegment(sketch, "E311", {"start": v(827.08, -1648.54) * mm, "end": v(828.5, -1654.65) * mm});
            skLineSegment(sketch, "E312", {"start": v(828.5, -1654.65) * mm, "end": v(829.92, -1661.14) * mm});
            skLineSegment(sketch, "E313", {"start": v(829.92, -1661.14) * mm, "end": v(831.31, -1668.03) * mm});
            skLineSegment(sketch, "E314", {"start": v(831.31, -1668.03) * mm, "end": v(832.68, -1675.32) * mm});
            skLineSegment(sketch, "E315", {"start": v(832.68, -1675.32) * mm, "end": v(834, -1683) * mm});
            skLineSegment(sketch, "E316", {"start": v(834, -1683) * mm, "end": v(835.27, -1691.06) * mm});
            skLineSegment(sketch, "E317", {"start": v(835.27, -1691.06) * mm, "end": v(836.48, -1699.53) * mm});
            skLineSegment(sketch, "E318", {"start": v(836.48, -1699.53) * mm, "end": v(837.62, -1708.39) * mm});
            skLineSegment(sketch, "E319", {"start": v(837.62, -1708.39) * mm, "end": v(838.66, -1717.64) * mm});
            skLineSegment(sketch, "E320", {"start": v(838.66, -1717.64) * mm, "end": v(839.61, -1727.28) * mm});
            skLineSegment(sketch, "E321", {"start": v(839.61, -1727.28) * mm, "end": v(840.45, -1737.32) * mm});
            skLineSegment(sketch, "E322", {"start": v(840.45, -1737.32) * mm, "end": v(841.17, -1747.74) * mm});
            skLineSegment(sketch, "E323", {"start": v(841.17, -1747.74) * mm, "end": v(841.76, -1758.55) * mm});
            skLineSegment(sketch, "E324", {"start": v(841.76, -1758.55) * mm, "end": v(842.21, -1769.76) * mm});
            skLineSegment(sketch, "E325", {"start": v(842.21, -1769.76) * mm, "end": v(842.5, -1781.34) * mm});
            skLineSegment(sketch, "E326", {"start": v(842.5, -1781.34) * mm, "end": v(842.64, -1793.31) * mm});
            skLineSegment(sketch, "E327", {"start": v(842.64, -1793.31) * mm, "end": v(842.6, -1805.66) * mm});
            skLineSegment(sketch, "E328", {"start": v(842.6, -1805.66) * mm, "end": v(842.36, -1818.39) * mm});
            skLineSegment(sketch, "E329", {"start": v(842.36, -1818.39) * mm, "end": v(841.93, -1831.5) * mm});
            skLineSegment(sketch, "E330", {"start": v(841.93, -1831.5) * mm, "end": v(841.3, -1844.97) * mm});
            skLineSegment(sketch, "E331", {"start": v(841.3, -1844.97) * mm, "end": v(840.44, -1858.81) * mm});
            skLineSegment(sketch, "E332", {"start": v(840.44, -1858.81) * mm, "end": v(839.35, -1873.02) * mm});
            skLineSegment(sketch, "E333", {"start": v(839.35, -1873.02) * mm, "end": v(838.02, -1887.59) * mm});
            skLineSegment(sketch, "E334", {"start": v(838.02, -1887.59) * mm, "end": v(836.44, -1902.52) * mm});
            skLineSegment(sketch, "E335", {"start": v(836.44, -1902.52) * mm, "end": v(834.6, -1917.8) * mm});
            skLineSegment(sketch, "E336", {"start": v(834.6, -1917.8) * mm, "end": v(832.48, -1933.42) * mm});
            skLineSegment(sketch, "E337", {"start": v(832.48, -1933.42) * mm, "end": v(830.08, -1949.4) * mm});
            skLineSegment(sketch, "E338", {"start": v(830.08, -1949.4) * mm, "end": v(827.4, -1965.7) * mm});
            skLineSegment(sketch, "E339", {"start": v(827.4, -1965.7) * mm, "end": v(824.4, -1982.35) * mm});
            skLineSegment(sketch, "E340", {"start": v(824.4, -1982.35) * mm, "end": v(821.08, -1999.32) * mm});
            skLineSegment(sketch, "E341", {"start": v(821.08, -1999.32) * mm, "end": v(817.45, -2016.6) * mm});
            skLineSegment(sketch, "E342", {"start": v(817.45, -2016.6) * mm, "end": v(810.99, -2028) * mm});
            skLineSegment(sketch, "E343", {"start": v(810.99, -2028) * mm, "end": v(749.88, -2051.37) * mm});
            skLineSegment(sketch, "E344", {"start": v(749.88, -2051.37) * mm, "end": v(737.47, -2047.2) * mm});
            skLineSegment(sketch, "E345", {"start": v(737.47, -2047.2) * mm, "end": v(723.22, -2036.76) * mm});
            skLineSegment(sketch, "E346", {"start": v(723.22, -2036.76) * mm, "end": v(709.43, -2026.34) * mm});
            skLineSegment(sketch, "E347", {"start": v(709.43, -2026.34) * mm, "end": v(696.09, -2015.94) * mm});
            skLineSegment(sketch, "E348", {"start": v(696.09, -2015.94) * mm, "end": v(683.2, -2005.6) * mm});
            skLineSegment(sketch, "E349", {"start": v(683.2, -2005.6) * mm, "end": v(670.75, -1995.3) * mm});
            skLineSegment(sketch, "E350", {"start": v(670.75, -1995.3) * mm, "end": v(658.74, -1985.08) * mm});
            skLineSegment(sketch, "E351", {"start": v(658.74, -1985.08) * mm, "end": v(647.17, -1974.94) * mm});
            skLineSegment(sketch, "E352", {"start": v(647.17, -1974.94) * mm, "end": v(636.03, -1964.88) * mm});
            skLineSegment(sketch, "E353", {"start": v(636.03, -1964.88) * mm, "end": v(625.31, -1954.91) * mm});
            skLineSegment(sketch, "E354", {"start": v(625.31, -1954.91) * mm, "end": v(615.02, -1945.06) * mm});
            skLineSegment(sketch, "E355", {"start": v(615.02, -1945.06) * mm, "end": v(605.14, -1935.33) * mm});
            skLineSegment(sketch, "E356", {"start": v(605.14, -1935.33) * mm, "end": v(595.67, -1925.72) * mm});
            skLineSegment(sketch, "E357", {"start": v(595.67, -1925.72) * mm, "end": v(586.6, -1916.25) * mm});
            skLineSegment(sketch, "E358", {"start": v(586.6, -1916.25) * mm, "end": v(577.94, -1906.92) * mm});
            skLineSegment(sketch, "E359", {"start": v(577.94, -1906.92) * mm, "end": v(569.66, -1897.76) * mm});
            skLineSegment(sketch, "E360", {"start": v(569.66, -1897.76) * mm, "end": v(561.77, -1888.76) * mm});
            skLineSegment(sketch, "E361", {"start": v(561.77, -1888.76) * mm, "end": v(554.25, -1879.94) * mm});
            skLineSegment(sketch, "E362", {"start": v(554.25, -1879.94) * mm, "end": v(547.1, -1871.3) * mm});
            skLineSegment(sketch, "E363", {"start": v(547.1, -1871.3) * mm, "end": v(540.33, -1862.85) * mm});
            skLineSegment(sketch, "E364", {"start": v(540.33, -1862.85) * mm, "end": v(533.9, -1854.6) * mm});
            skLineSegment(sketch, "E365", {"start": v(533.9, -1854.6) * mm, "end": v(527.83, -1846.57) * mm});
            skLineSegment(sketch, "E366", {"start": v(527.83, -1846.57) * mm, "end": v(522.1, -1838.76) * mm});
            skLineSegment(sketch, "E367", {"start": v(522.1, -1838.76) * mm, "end": v(516.7, -1831.17) * mm});
            skLineSegment(sketch, "E368", {"start": v(516.7, -1831.17) * mm, "end": v(511.64, -1823.82) * mm});
            skLineSegment(sketch, "E369", {"start": v(511.64, -1823.82) * mm, "end": v(506.89, -1816.71) * mm});
            skLineSegment(sketch, "E370", {"start": v(506.89, -1816.71) * mm, "end": v(502.45, -1809.85) * mm});
            skLineSegment(sketch, "E371", {"start": v(502.45, -1809.85) * mm, "end": v(498.31, -1803.25) * mm});
            skLineSegment(sketch, "E372", {"start": v(498.31, -1803.25) * mm, "end": v(494.47, -1796.92) * mm});
            skLineSegment(sketch, "E373", {"start": v(494.47, -1796.92) * mm, "end": v(490.9, -1790.86) * mm});
            skLineSegment(sketch, "E374", {"start": v(490.9, -1790.86) * mm, "end": v(487.62, -1785.07) * mm});
            skLineSegment(sketch, "E375", {"start": v(487.62, -1785.07) * mm, "end": v(484.6, -1779.58) * mm});
            skLineSegment(sketch, "E376", {"start": v(484.6, -1779.58) * mm, "end": v(481.85, -1774.37) * mm});
            skLineSegment(sketch, "E377", {"start": v(481.85, -1774.37) * mm, "end": v(479.34, -1769.47) * mm});
            skLineSegment(sketch, "E378", {"start": v(479.34, -1769.47) * mm, "end": v(477.07, -1764.87) * mm});
            skLineSegment(sketch, "E379", {"start": v(477.07, -1764.87) * mm, "end": v(475.03, -1760.58) * mm});
            skLineSegment(sketch, "E380", {"start": v(475.03, -1760.58) * mm, "end": v(471.8, -1760.8) * mm});
            skLineSegment(sketch, "E381", {"start": v(471.8, -1760.8) * mm, "end": v(375.15, -1783.9) * mm});
            skLineSegment(sketch, "E382", {"start": v(375.15, -1783.9) * mm, "end": v(372.17, -1785.15) * mm});
            skLineSegment(sketch, "E383", {"start": v(372.17, -1785.15) * mm, "end": v(372.3, -1789.9) * mm});
            skLineSegment(sketch, "E384", {"start": v(372.3, -1789.9) * mm, "end": v(372.35, -1795.03) * mm});
            skLineSegment(sketch, "E385", {"start": v(372.35, -1795.03) * mm, "end": v(372.33, -1800.54) * mm});
            skLineSegment(sketch, "E386", {"start": v(372.33, -1800.54) * mm, "end": v(372.22, -1806.43) * mm});
            skLineSegment(sketch, "E387", {"start": v(372.22, -1806.43) * mm, "end": v(372.02, -1812.7) * mm});
            skLineSegment(sketch, "E388", {"start": v(372.02, -1812.7) * mm, "end": v(371.7, -1819.34) * mm});
            skLineSegment(sketch, "E389", {"start": v(371.7, -1819.34) * mm, "end": v(371.27, -1826.36) * mm});
            skLineSegment(sketch, "E390", {"start": v(371.27, -1826.36) * mm, "end": v(370.7, -1833.74) * mm});
            skLineSegment(sketch, "E391", {"start": v(370.7, -1833.74) * mm, "end": v(370, -1841.5) * mm});
            skLineSegment(sketch, "E392", {"start": v(370, -1841.5) * mm, "end": v(369.13, -1849.63) * mm});
            skLineSegment(sketch, "E393", {"start": v(369.13, -1849.63) * mm, "end": v(368.1, -1858.12) * mm});
            skLineSegment(sketch, "E394", {"start": v(368.1, -1858.12) * mm, "end": v(366.91, -1866.96) * mm});
            skLineSegment(sketch, "E395", {"start": v(366.91, -1866.96) * mm, "end": v(365.53, -1876.17) * mm});
            skLineSegment(sketch, "E396", {"start": v(365.53, -1876.17) * mm, "end": v(363.95, -1885.73) * mm});
            skLineSegment(sketch, "E397", {"start": v(363.95, -1885.73) * mm, "end": v(362.16, -1895.64) * mm});
            skLineSegment(sketch, "E398", {"start": v(362.16, -1895.64) * mm, "end": v(360.16, -1905.9) * mm});
            skLineSegment(sketch, "E399", {"start": v(360.16, -1905.9) * mm, "end": v(357.93, -1916.5) * mm});
            skLineSegment(sketch, "E400", {"start": v(357.93, -1916.5) * mm, "end": v(355.47, -1927.43) * mm});
            skLineSegment(sketch, "E401", {"start": v(355.47, -1927.43) * mm, "end": v(352.75, -1938.7) * mm});
            skLineSegment(sketch, "E402", {"start": v(352.75, -1938.7) * mm, "end": v(349.78, -1950.3) * mm});
            skLineSegment(sketch, "E403", {"start": v(349.78, -1950.3) * mm, "end": v(346.54, -1962.21) * mm});
            skLineSegment(sketch, "E404", {"start": v(346.54, -1962.21) * mm, "end": v(343.02, -1974.45) * mm});
            skLineSegment(sketch, "E405", {"start": v(343.02, -1974.45) * mm, "end": v(339.22, -1987) * mm});
            skLineSegment(sketch, "E406", {"start": v(339.22, -1987) * mm, "end": v(335.11, -1999.84) * mm});
            skLineSegment(sketch, "E407", {"start": v(335.11, -1999.84) * mm, "end": v(330.7, -2013) * mm});
            skLineSegment(sketch, "E408", {"start": v(330.7, -2013) * mm, "end": v(325.98, -2026.44) * mm});
            skLineSegment(sketch, "E409", {"start": v(325.98, -2026.44) * mm, "end": v(320.92, -2040.17) * mm});
            skLineSegment(sketch, "E410", {"start": v(320.92, -2040.17) * mm, "end": v(315.53, -2054.18) * mm});
            skLineSegment(sketch, "E411", {"start": v(315.53, -2054.18) * mm, "end": v(309.8, -2068.46) * mm});
            skLineSegment(sketch, "E412", {"start": v(309.8, -2068.46) * mm, "end": v(303.71, -2083) * mm});
            skLineSegment(sketch, "E413", {"start": v(303.71, -2083) * mm, "end": v(297.26, -2097.81) * mm});
            skLineSegment(sketch, "E414", {"start": v(297.26, -2097.81) * mm, "end": v(290.44, -2112.87) * mm});
            skLineSegment(sketch, "E415", {"start": v(290.44, -2112.87) * mm, "end": v(283.24, -2128.17) * mm});
            skLineSegment(sketch, "E416", {"start": v(283.24, -2128.17) * mm, "end": v(275.64, -2143.7) * mm});
            skLineSegment(sketch, "E417", {"start": v(275.64, -2143.7) * mm, "end": v(267.66, -2159.46) * mm});
            skLineSegment(sketch, "E418", {"start": v(267.66, -2159.46) * mm, "end": v(258.47, -2168.79) * mm});
            skLineSegment(sketch, "E419", {"start": v(258.47, -2168.79) * mm, "end": v(193.4, -2175.56) * mm});
            skLineSegment(sketch, "E420", {"start": v(193.4, -2175.56) * mm, "end": v(182.48, -2168.32) * mm});
            skLineSegment(sketch, "E421", {"start": v(182.48, -2168.32) * mm, "end": v(171.42, -2154.54) * mm});
            skLineSegment(sketch, "E422", {"start": v(171.42, -2154.54) * mm, "end": v(160.8, -2140.9) * mm});
            skLineSegment(sketch, "E423", {"start": v(160.8, -2140.9) * mm, "end": v(150.6, -2127.41) * mm});
            skLineSegment(sketch, "E424", {"start": v(150.6, -2127.41) * mm, "end": v(140.83, -2114.08) * mm});
            skLineSegment(sketch, "E425", {"start": v(140.83, -2114.08) * mm, "end": v(131.47, -2100.92) * mm});
            skLineSegment(sketch, "E426", {"start": v(131.47, -2100.92) * mm, "end": v(122.52, -2087.94) * mm});
            skLineSegment(sketch, "E427", {"start": v(122.52, -2087.94) * mm, "end": v(113.97, -2075.14) * mm});
            skLineSegment(sketch, "E428", {"start": v(113.97, -2075.14) * mm, "end": v(105.8, -2062.54) * mm});
            skLineSegment(sketch, "E429", {"start": v(105.8, -2062.54) * mm, "end": v(98.04, -2050.15) * mm});
            skLineSegment(sketch, "E430", {"start": v(98.04, -2050.15) * mm, "end": v(90.64, -2037.96) * mm});
            skLineSegment(sketch, "E431", {"start": v(90.64, -2037.96) * mm, "end": v(83.62, -2026) * mm});
            skLineSegment(sketch, "E432", {"start": v(83.62, -2026) * mm, "end": v(76.96, -2014.27) * mm});
            skLineSegment(sketch, "E433", {"start": v(76.96, -2014.27) * mm, "end": v(70.66, -2002.78) * mm});
            skLineSegment(sketch, "E434", {"start": v(70.66, -2002.78) * mm, "end": v(64.7, -1991.53) * mm});
            skLineSegment(sketch, "E435", {"start": v(64.7, -1991.53) * mm, "end": v(59.07, -1980.53) * mm});
            skLineSegment(sketch, "E436", {"start": v(59.07, -1980.53) * mm, "end": v(53.78, -1969.8) * mm});
            skLineSegment(sketch, "E437", {"start": v(53.78, -1969.8) * mm, "end": v(48.8, -1959.33) * mm});
            skLineSegment(sketch, "E438", {"start": v(48.8, -1959.33) * mm, "end": v(44.14, -1949.14) * mm});
            skLineSegment(sketch, "E439", {"start": v(44.14, -1949.14) * mm, "end": v(39.78, -1939.22) * mm});
            skLineSegment(sketch, "E440", {"start": v(39.78, -1939.22) * mm, "end": v(35.7, -1929.6) * mm});
            skLineSegment(sketch, "E441", {"start": v(35.7, -1929.6) * mm, "end": v(31.92, -1920.27) * mm});
            skLineSegment(sketch, "E442", {"start": v(31.92, -1920.27) * mm, "end": v(28.4, -1911.24) * mm});
            skLineSegment(sketch, "E443", {"start": v(28.4, -1911.24) * mm, "end": v(25.16, -1902.51) * mm});
            skLineSegment(sketch, "E444", {"start": v(25.16, -1902.51) * mm, "end": v(22.17, -1894.1) * mm});
            skLineSegment(sketch, "E445", {"start": v(22.17, -1894.1) * mm, "end": v(19.42, -1886) * mm});
            skLineSegment(sketch, "E446", {"start": v(19.42, -1886) * mm, "end": v(16.9, -1878.23) * mm});
            skLineSegment(sketch, "E447", {"start": v(16.9, -1878.23) * mm, "end": v(14.61, -1870.78) * mm});
            skLineSegment(sketch, "E448", {"start": v(14.61, -1870.78) * mm, "end": v(12.54, -1863.67) * mm});
            skLineSegment(sketch, "E449", {"start": v(12.54, -1863.67) * mm, "end": v(10.67, -1856.9) * mm});
            skLineSegment(sketch, "E450", {"start": v(10.67, -1856.9) * mm, "end": v(9, -1850.46) * mm});
            skLineSegment(sketch, "E451", {"start": v(9, -1850.46) * mm, "end": v(7.5, -1844.36) * mm});
            skLineSegment(sketch, "E452", {"start": v(7.5, -1844.36) * mm, "end": v(6.19, -1838.62) * mm});
            skLineSegment(sketch, "E453", {"start": v(6.19, -1838.62) * mm, "end": v(5.03, -1833.24) * mm});
            skLineSegment(sketch, "E454", {"start": v(5.03, -1833.24) * mm, "end": v(4.03, -1828.2) * mm});
            skLineSegment(sketch, "E455", {"start": v(4.03, -1828.2) * mm, "end": v(3.17, -1823.53) * mm});
            skLineSegment(sketch, "E456", {"start": v(3.17, -1823.53) * mm, "end": v(0, -1822.91) * mm});
            skLineSegment(sketch, "E457", {"start": v(0, -1822.91) * mm, "end": v(-99.34, -1820.2) * mm});
            skLineSegment(sketch, "E458", {"start": v(-99.34, -1820.2) * mm, "end": v(-102.54, -1820.65) * mm});
            skLineSegment(sketch, "E459", {"start": v(-102.54, -1820.65) * mm, "end": v(-103.65, -1825.27) * mm});
            skLineSegment(sketch, "E460", {"start": v(-103.65, -1825.27) * mm, "end": v(-104.93, -1830.24) * mm});
            skLineSegment(sketch, "E461", {"start": v(-104.93, -1830.24) * mm, "end": v(-106.37, -1835.55) * mm});
            skLineSegment(sketch, "E462", {"start": v(-106.37, -1835.55) * mm, "end": v(-108, -1841.22) * mm});
            skLineSegment(sketch, "E463", {"start": v(-108, -1841.22) * mm, "end": v(-109.82, -1847.22) * mm});
            skLineSegment(sketch, "E464", {"start": v(-109.82, -1847.22) * mm, "end": v(-111.84, -1853.55) * mm});
            skLineSegment(sketch, "E465", {"start": v(-111.84, -1853.55) * mm, "end": v(-114.08, -1860.22) * mm});
            skLineSegment(sketch, "E466", {"start": v(-114.08, -1860.22) * mm, "end": v(-116.54, -1867.2) * mm});
            skLineSegment(sketch, "E467", {"start": v(-116.54, -1867.2) * mm, "end": v(-119.23, -1874.52) * mm});
            skLineSegment(sketch, "E468", {"start": v(-119.23, -1874.52) * mm, "end": v(-122.16, -1882.14) * mm});
            skLineSegment(sketch, "E469", {"start": v(-122.16, -1882.14) * mm, "end": v(-125.35, -1890.08) * mm});
            skLineSegment(sketch, "E470", {"start": v(-125.35, -1890.08) * mm, "end": v(-128.8, -1898.31) * mm});
            skLineSegment(sketch, "E471", {"start": v(-128.8, -1898.31) * mm, "end": v(-132.52, -1906.85) * mm});
            skLineSegment(sketch, "E472", {"start": v(-132.52, -1906.85) * mm, "end": v(-136.52, -1915.67) * mm});
            skLineSegment(sketch, "E473", {"start": v(-136.52, -1915.67) * mm, "end": v(-140.8, -1924.79) * mm});
            skLineSegment(sketch, "E474", {"start": v(-140.8, -1924.79) * mm, "end": v(-145.4, -1934.17) * mm});
            skLineSegment(sketch, "E475", {"start": v(-145.4, -1934.17) * mm, "end": v(-150.29, -1943.83) * mm});
            skLineSegment(sketch, "E476", {"start": v(-150.29, -1943.83) * mm, "end": v(-155.5, -1953.76) * mm});
            skLineSegment(sketch, "E477", {"start": v(-155.5, -1953.76) * mm, "end": v(-161.04, -1963.94) * mm});
            skLineSegment(sketch, "E478", {"start": v(-161.04, -1963.94) * mm, "end": v(-166.91, -1974.37) * mm});
            skLineSegment(sketch, "E479", {"start": v(-166.91, -1974.37) * mm, "end": v(-173.12, -1985.04) * mm});
            skLineSegment(sketch, "E480", {"start": v(-173.12, -1985.04) * mm, "end": v(-179.69, -1995.95) * mm});
            skLineSegment(sketch, "E481", {"start": v(-179.69, -1995.95) * mm, "end": v(-186.61, -2007.08) * mm});
            skLineSegment(sketch, "E482", {"start": v(-186.61, -2007.08) * mm, "end": v(-193.9, -2018.44) * mm});
            skLineSegment(sketch, "E483", {"start": v(-193.9, -2018.44) * mm, "end": v(-201.57, -2030) * mm});
            skLineSegment(sketch, "E484", {"start": v(-201.57, -2030) * mm, "end": v(-209.61, -2041.76) * mm});
            skLineSegment(sketch, "E485", {"start": v(-209.61, -2041.76) * mm, "end": v(-218.05, -2053.71) * mm});
            skLineSegment(sketch, "E486", {"start": v(-218.05, -2053.71) * mm, "end": v(-226.88, -2065.85) * mm});
            skLineSegment(sketch, "E487", {"start": v(-226.88, -2065.85) * mm, "end": v(-236.11, -2078.16) * mm});
            skLineSegment(sketch, "E488", {"start": v(-236.11, -2078.16) * mm, "end": v(-245.76, -2090.63) * mm});
            skLineSegment(sketch, "E489", {"start": v(-245.76, -2090.63) * mm, "end": v(-255.82, -2103.27) * mm});
            skLineSegment(sketch, "E490", {"start": v(-255.82, -2103.27) * mm, "end": v(-266.3, -2116.04) * mm});
            skLineSegment(sketch, "E491", {"start": v(-266.3, -2116.04) * mm, "end": v(-277.23, -2128.96) * mm});
            skLineSegment(sketch, "E492", {"start": v(-277.23, -2128.96) * mm, "end": v(-288.58, -2142) * mm});
            skLineSegment(sketch, "E493", {"start": v(-288.58, -2142) * mm, "end": v(-300.37, -2155.16) * mm});
            skLineSegment(sketch, "E494", {"start": v(-300.37, -2155.16) * mm, "end": v(-311.66, -2161.79) * mm});
            skLineSegment(sketch, "E495", {"start": v(-311.66, -2161.79) * mm, "end": v(-376.27, -2151.48) * mm});
            skLineSegment(sketch, "E496", {"start": v(-376.27, -2151.48) * mm, "end": v(-384.94, -2141.67) * mm});
            skLineSegment(sketch, "E497", {"start": v(-384.94, -2141.67) * mm, "end": v(-392.05, -2125.5) * mm});
            skLineSegment(sketch, "E498", {"start": v(-392.05, -2125.5) * mm, "end": v(-398.79, -2109.57) * mm});
            skLineSegment(sketch, "E499", {"start": v(-398.79, -2109.57) * mm, "end": v(-405.14, -2093.9) * mm});
            skLineSegment(sketch, "E500", {"start": v(-405.14, -2093.9) * mm, "end": v(-411.14, -2078.5) * mm});
            skLineSegment(sketch, "E501", {"start": v(-411.14, -2078.5) * mm, "end": v(-416.77, -2063.36) * mm});
            skLineSegment(sketch, "E502", {"start": v(-416.77, -2063.36) * mm, "end": v(-422.06, -2048.5) * mm});
            skLineSegment(sketch, "E503", {"start": v(-422.06, -2048.5) * mm, "end": v(-427, -2033.93) * mm});
            skLineSegment(sketch, "E504", {"start": v(-427, -2033.93) * mm, "end": v(-431.62, -2019.65) * mm});
            skLineSegment(sketch, "E505", {"start": v(-431.62, -2019.65) * mm, "end": v(-435.92, -2005.66) * mm});
            skLineSegment(sketch, "E506", {"start": v(-435.92, -2005.66) * mm, "end": v(-439.9, -1991.98) * mm});
            skLineSegment(sketch, "E507", {"start": v(-439.9, -1991.98) * mm, "end": v(-443.6, -1978.61) * mm});
            skLineSegment(sketch, "E508", {"start": v(-443.6, -1978.61) * mm, "end": v(-447, -1965.56) * mm});
            skLineSegment(sketch, "E509", {"start": v(-447, -1965.56) * mm, "end": v(-450.1, -1952.82) * mm});
            skLineSegment(sketch, "E510", {"start": v(-450.1, -1952.82) * mm, "end": v(-452.96, -1940.41) * mm});
            skLineSegment(sketch, "E511", {"start": v(-452.96, -1940.41) * mm, "end": v(-455.54, -1928.34) * mm});
            skLineSegment(sketch, "E512", {"start": v(-455.54, -1928.34) * mm, "end": v(-457.88, -1916.6) * mm});
            skLineSegment(sketch, "E513", {"start": v(-457.88, -1916.6) * mm, "end": v(-459.97, -1905.2) * mm});
            skLineSegment(sketch, "E514", {"start": v(-459.97, -1905.2) * mm, "end": v(-461.84, -1894.14) * mm});
            skLineSegment(sketch, "E515", {"start": v(-461.84, -1894.14) * mm, "end": v(-463.49, -1883.44) * mm});
            skLineSegment(sketch, "E516", {"start": v(-463.49, -1883.44) * mm, "end": v(-464.93, -1873.1) * mm});
            skLineSegment(sketch, "E517", {"start": v(-464.93, -1873.1) * mm, "end": v(-466.17, -1863.1) * mm});
            skLineSegment(sketch, "E518", {"start": v(-466.17, -1863.1) * mm, "end": v(-467.22, -1853.46) * mm});
            skLineSegment(sketch, "E519", {"start": v(-467.22, -1853.46) * mm, "end": v(-468.1, -1844.2) * mm});
            skLineSegment(sketch, "E520", {"start": v(-468.1, -1844.2) * mm, "end": v(-468.82, -1835.3) * mm});
            skLineSegment(sketch, "E521", {"start": v(-468.82, -1835.3) * mm, "end": v(-469.38, -1826.76) * mm});
            skLineSegment(sketch, "E522", {"start": v(-469.38, -1826.76) * mm, "end": v(-469.8, -1818.6) * mm});
            skLineSegment(sketch, "E523", {"start": v(-469.8, -1818.6) * mm, "end": v(-470.08, -1810.82) * mm});
            skLineSegment(sketch, "E524", {"start": v(-470.08, -1810.82) * mm, "end": v(-470.24, -1803.41) * mm});
            skLineSegment(sketch, "E525", {"start": v(-470.24, -1803.41) * mm, "end": v(-470.3, -1796.38) * mm});
            skLineSegment(sketch, "E526", {"start": v(-470.3, -1796.38) * mm, "end": v(-470.24, -1789.73) * mm});
            skLineSegment(sketch, "E527", {"start": v(-470.24, -1789.73) * mm, "end": v(-470.1, -1783.46) * mm});
            skLineSegment(sketch, "E528", {"start": v(-470.1, -1783.46) * mm, "end": v(-469.9, -1777.58) * mm});
            skLineSegment(sketch, "E529", {"start": v(-469.9, -1777.58) * mm, "end": v(-469.61, -1772.07) * mm});
            skLineSegment(sketch, "E530", {"start": v(-469.61, -1772.07) * mm, "end": v(-469.28, -1766.95) * mm});
            skLineSegment(sketch, "E531", {"start": v(-469.28, -1766.95) * mm, "end": v(-468.9, -1762.22) * mm});
            skLineSegment(sketch, "E532", {"start": v(-468.9, -1762.22) * mm, "end": v(-471.8, -1760.8) * mm});
            skLineSegment(sketch, "E533", {"start": v(-471.8, -1760.8) * mm, "end": v(-567.06, -1732.47) * mm});
            skLineSegment(sketch, "E534", {"start": v(-567.06, -1732.47) * mm, "end": v(-570.26, -1732.07) * mm});
            skLineSegment(sketch, "E535", {"start": v(-570.26, -1732.07) * mm, "end": v(-572.54, -1736.25) * mm});
            skLineSegment(sketch, "E536", {"start": v(-572.54, -1736.25) * mm, "end": v(-575.05, -1740.72) * mm});
            skLineSegment(sketch, "E537", {"start": v(-575.05, -1740.72) * mm, "end": v(-577.82, -1745.48) * mm});
            skLineSegment(sketch, "E538", {"start": v(-577.82, -1745.48) * mm, "end": v(-580.86, -1750.52) * mm});
            skLineSegment(sketch, "E539", {"start": v(-580.86, -1750.52) * mm, "end": v(-584.17, -1755.85) * mm});
            skLineSegment(sketch, "E540", {"start": v(-584.17, -1755.85) * mm, "end": v(-587.77, -1761.44) * mm});
            skLineSegment(sketch, "E541", {"start": v(-587.77, -1761.44) * mm, "end": v(-591.65, -1767.3) * mm});
            skLineSegment(sketch, "E542", {"start": v(-591.65, -1767.3) * mm, "end": v(-595.84, -1773.42) * mm});
            skLineSegment(sketch, "E543", {"start": v(-595.84, -1773.42) * mm, "end": v(-600.33, -1779.78) * mm});
            skLineSegment(sketch, "E544", {"start": v(-600.33, -1779.78) * mm, "end": v(-605.13, -1786.4) * mm});
            skLineSegment(sketch, "E545", {"start": v(-605.13, -1786.4) * mm, "end": v(-610.27, -1793.23) * mm});
            skLineSegment(sketch, "E546", {"start": v(-610.27, -1793.23) * mm, "end": v(-615.73, -1800.3) * mm});
            skLineSegment(sketch, "E547", {"start": v(-615.73, -1800.3) * mm, "end": v(-621.53, -1807.58) * mm});
            skLineSegment(sketch, "E548", {"start": v(-621.53, -1807.58) * mm, "end": v(-627.68, -1815.07) * mm});
            skLineSegment(sketch, "E549", {"start": v(-627.68, -1815.07) * mm, "end": v(-634.18, -1822.76) * mm});
            skLineSegment(sketch, "E550", {"start": v(-634.18, -1822.76) * mm, "end": v(-641.04, -1830.64) * mm});
            skLineSegment(sketch, "E551", {"start": v(-641.04, -1830.64) * mm, "end": v(-648.27, -1838.7) * mm});
            skLineSegment(sketch, "E552", {"start": v(-648.27, -1838.7) * mm, "end": v(-655.87, -1846.94) * mm});
            skLineSegment(sketch, "E553", {"start": v(-655.87, -1846.94) * mm, "end": v(-663.86, -1855.34) * mm});
            skLineSegment(sketch, "E554", {"start": v(-663.86, -1855.34) * mm, "end": v(-672.23, -1863.9) * mm});
            skLineSegment(sketch, "E555", {"start": v(-672.23, -1863.9) * mm, "end": v(-681, -1872.6) * mm});
            skLineSegment(sketch, "E556", {"start": v(-681, -1872.6) * mm, "end": v(-690.16, -1881.43) * mm});
            skLineSegment(sketch, "E557", {"start": v(-690.16, -1881.43) * mm, "end": v(-699.73, -1890.4) * mm});
            skLineSegment(sketch, "E558", {"start": v(-699.73, -1890.4) * mm, "end": v(-709.7, -1899.47) * mm});
            skLineSegment(sketch, "E559", {"start": v(-709.7, -1899.47) * mm, "end": v(-720.1, -1908.66) * mm});
            skLineSegment(sketch, "E560", {"start": v(-720.1, -1908.66) * mm, "end": v(-730.91, -1917.93) * mm});
            skLineSegment(sketch, "E561", {"start": v(-730.91, -1917.93) * mm, "end": v(-742.16, -1927.3) * mm});
            skLineSegment(sketch, "E562", {"start": v(-742.16, -1927.3) * mm, "end": v(-753.83, -1936.74) * mm});
            skLineSegment(sketch, "E563", {"start": v(-753.83, -1936.74) * mm, "end": v(-765.94, -1946.24) * mm});
            skLineSegment(sketch, "E564", {"start": v(-765.94, -1946.24) * mm, "end": v(-778.48, -1955.8) * mm});
            skLineSegment(sketch, "E565", {"start": v(-778.48, -1955.8) * mm, "end": v(-791.47, -1965.39) * mm});
            skLineSegment(sketch, "E566", {"start": v(-791.47, -1965.39) * mm, "end": v(-804.9, -1975.02) * mm});
            skLineSegment(sketch, "E567", {"start": v(-804.9, -1975.02) * mm, "end": v(-818.8, -1984.66) * mm});
            skLineSegment(sketch, "E568", {"start": v(-818.8, -1984.66) * mm, "end": v(-833.14, -1994.32) * mm});
            skLineSegment(sketch, "E569", {"start": v(-833.14, -1994.32) * mm, "end": v(-847.93, -2003.98) * mm});
            skLineSegment(sketch, "E570", {"start": v(-847.93, -2003.98) * mm, "end": v(-860.55, -2007.46) * mm});
            skLineSegment(sketch, "E571", {"start": v(-860.55, -2007.46) * mm, "end": v(-920.3, -1980.78) * mm});
            skLineSegment(sketch, "E572", {"start": v(-920.3, -1980.78) * mm, "end": v(-926.12, -1969.07) * mm});
            skLineSegment(sketch, "E573", {"start": v(-926.12, -1969.07) * mm, "end": v(-928.81, -1951.6) * mm});
            skLineSegment(sketch, "E574", {"start": v(-928.81, -1951.6) * mm, "end": v(-931.2, -1934.48) * mm});
            skLineSegment(sketch, "E575", {"start": v(-931.2, -1934.48) * mm, "end": v(-933.28, -1917.7) * mm});
            skLineSegment(sketch, "E576", {"start": v(-933.28, -1917.7) * mm, "end": v(-935.08, -1901.26) * mm});
            skLineSegment(sketch, "E577", {"start": v(-935.08, -1901.26) * mm, "end": v(-936.6, -1885.19) * mm});
            skLineSegment(sketch, "E578", {"start": v(-936.6, -1885.19) * mm, "end": v(-937.87, -1869.47) * mm});
            skLineSegment(sketch, "E579", {"start": v(-937.87, -1869.47) * mm, "end": v(-938.87, -1854.1) * mm});
            skLineSegment(sketch, "E580", {"start": v(-938.87, -1854.1) * mm, "end": v(-939.64, -1839.12) * mm});
            skLineSegment(sketch, "E581", {"start": v(-939.64, -1839.12) * mm, "end": v(-940.17, -1824.5) * mm});
            skLineSegment(sketch, "E582", {"start": v(-940.17, -1824.5) * mm, "end": v(-940.48, -1810.25) * mm});
            skLineSegment(sketch, "E583", {"start": v(-940.48, -1810.25) * mm, "end": v(-940.58, -1796.38) * mm});
            skLineSegment(sketch, "E584", {"start": v(-940.58, -1796.38) * mm, "end": v(-940.48, -1782.9) * mm});
            skLineSegment(sketch, "E585", {"start": v(-940.48, -1782.9) * mm, "end": v(-940.2, -1769.78) * mm});
            skLineSegment(sketch, "E586", {"start": v(-940.2, -1769.78) * mm, "end": v(-939.74, -1757.06) * mm});
            skLineSegment(sketch, "E587", {"start": v(-939.74, -1757.06) * mm, "end": v(-939.1, -1744.73) * mm});
            skLineSegment(sketch, "E588", {"start": v(-939.1, -1744.73) * mm, "end": v(-938.33, -1732.78) * mm});
            skLineSegment(sketch, "E589", {"start": v(-938.33, -1732.78) * mm, "end": v(-937.4, -1721.23) * mm});
            skLineSegment(sketch, "E590", {"start": v(-937.4, -1721.23) * mm, "end": v(-936.34, -1710.07) * mm});
            skLineSegment(sketch, "E591", {"start": v(-936.34, -1710.07) * mm, "end": v(-935.16, -1699.3) * mm});
            skLineSegment(sketch, "E592", {"start": v(-935.16, -1699.3) * mm, "end": v(-933.88, -1688.93) * mm});
            skLineSegment(sketch, "E593", {"start": v(-933.88, -1688.93) * mm, "end": v(-932.5, -1678.96) * mm});
            skLineSegment(sketch, "E594", {"start": v(-932.5, -1678.96) * mm, "end": v(-931.02, -1669.38) * mm});
            skLineSegment(sketch, "E595", {"start": v(-931.02, -1669.38) * mm, "end": v(-929.47, -1660.2) * mm});
            skLineSegment(sketch, "E596", {"start": v(-929.47, -1660.2) * mm, "end": v(-927.85, -1651.42) * mm});
            skLineSegment(sketch, "E597", {"start": v(-927.85, -1651.42) * mm, "end": v(-926.18, -1643.03) * mm});
            skLineSegment(sketch, "E598", {"start": v(-926.18, -1643.03) * mm, "end": v(-924.48, -1635.04) * mm});
            skLineSegment(sketch, "E599", {"start": v(-924.48, -1635.04) * mm, "end": v(-922.73, -1627.45) * mm});
            skLineSegment(sketch, "E600", {"start": v(-922.73, -1627.45) * mm, "end": v(-920.97, -1620.25) * mm});
            skLineSegment(sketch, "E601", {"start": v(-920.97, -1620.25) * mm, "end": v(-919.2, -1613.45) * mm});
            skLineSegment(sketch, "E602", {"start": v(-919.2, -1613.45) * mm, "end": v(-917.44, -1607.04) * mm});
            skLineSegment(sketch, "E603", {"start": v(-917.44, -1607.04) * mm, "end": v(-915.68, -1601.02) * mm});
            skLineSegment(sketch, "E604", {"start": v(-915.68, -1601.02) * mm, "end": v(-913.95, -1595.39) * mm});
            skLineSegment(sketch, "E605", {"start": v(-913.95, -1595.39) * mm, "end": v(-912.26, -1590.15) * mm});
            skLineSegment(sketch, "E606", {"start": v(-912.26, -1590.15) * mm, "end": v(-910.6, -1585.29) * mm});
            skLineSegment(sketch, "E607", {"start": v(-910.6, -1585.29) * mm, "end": v(-909.02, -1580.81) * mm});
            skLineSegment(sketch, "E608", {"start": v(-909.02, -1580.81) * mm, "end": v(-911.46, -1578.69) * mm});
            skLineSegment(sketch, "E609", {"start": v(-911.46, -1578.69) * mm, "end": v(-996.13, -1526.67) * mm});
            skLineSegment(sketch, "E610", {"start": v(-996.13, -1526.67) * mm, "end": v(-999.13, -1525.46) * mm});
            skLineSegment(sketch, "E611", {"start": v(-999.13, -1525.46) * mm, "end": v(-1002.4, -1528.9) * mm});
            skLineSegment(sketch, "E612", {"start": v(-1002.4, -1528.9) * mm, "end": v(-1005.99, -1532.57) * mm});
            skLineSegment(sketch, "E613", {"start": v(-1005.99, -1532.57) * mm, "end": v(-1009.9, -1536.45) * mm});
            skLineSegment(sketch, "E614", {"start": v(-1009.9, -1536.45) * mm, "end": v(-1014.14, -1540.54) * mm});
            skLineSegment(sketch, "E615", {"start": v(-1014.14, -1540.54) * mm, "end": v(-1018.72, -1544.82) * mm});
            skLineSegment(sketch, "E616", {"start": v(-1018.72, -1544.82) * mm, "end": v(-1023.63, -1549.3) * mm});
            skLineSegment(sketch, "E617", {"start": v(-1023.63, -1549.3) * mm, "end": v(-1028.9, -1553.95) * mm});
            skLineSegment(sketch, "E618", {"start": v(-1028.9, -1553.95) * mm, "end": v(-1034.53, -1558.78) * mm});
            skLineSegment(sketch, "E619", {"start": v(-1034.53, -1558.78) * mm, "end": v(-1040.51, -1563.76) * mm});
            skLineSegment(sketch, "E620", {"start": v(-1040.51, -1563.76) * mm, "end": v(-1046.87, -1568.9) * mm});
            skLineSegment(sketch, "E621", {"start": v(-1046.87, -1568.9) * mm, "end": v(-1053.6, -1574.18) * mm});
            skLineSegment(sketch, "E622", {"start": v(-1053.6, -1574.18) * mm, "end": v(-1060.7, -1579.59) * mm});
            skLineSegment(sketch, "E623", {"start": v(-1060.7, -1579.59) * mm, "end": v(-1068.19, -1585.12) * mm});
            skLineSegment(sketch, "E624", {"start": v(-1068.19, -1585.12) * mm, "end": v(-1076.06, -1590.76) * mm});
            skLineSegment(sketch, "E625", {"start": v(-1076.06, -1590.76) * mm, "end": v(-1084.33, -1596.51) * mm});
            skLineSegment(sketch, "E626", {"start": v(-1084.33, -1596.51) * mm, "end": v(-1093, -1602.35) * mm});
            skLineSegment(sketch, "E627", {"start": v(-1093, -1602.35) * mm, "end": v(-1102.07, -1608.27) * mm});
            skLineSegment(sketch, "E628", {"start": v(-1102.07, -1608.27) * mm, "end": v(-1111.55, -1614.25) * mm});
            skLineSegment(sketch, "E629", {"start": v(-1111.55, -1614.25) * mm, "end": v(-1121.43, -1620.3) * mm});
            skLineSegment(sketch, "E630", {"start": v(-1121.43, -1620.3) * mm, "end": v(-1131.73, -1626.4) * mm});
            skLineSegment(sketch, "E631", {"start": v(-1131.73, -1626.4) * mm, "end": v(-1142.45, -1632.54) * mm});
            skLineSegment(sketch, "E632", {"start": v(-1142.45, -1632.54) * mm, "end": v(-1153.6, -1638.7) * mm});
            skLineSegment(sketch, "E633", {"start": v(-1153.6, -1638.7) * mm, "end": v(-1165.15, -1644.88) * mm});
            skLineSegment(sketch, "E634", {"start": v(-1165.15, -1644.88) * mm, "end": v(-1177.14, -1651.07) * mm});
            skLineSegment(sketch, "E635", {"start": v(-1177.14, -1651.07) * mm, "end": v(-1189.56, -1657.24) * mm});
            skLineSegment(sketch, "E636", {"start": v(-1189.56, -1657.24) * mm, "end": v(-1202.4, -1663.4) * mm});
            skLineSegment(sketch, "E637", {"start": v(-1202.4, -1663.4) * mm, "end": v(-1215.69, -1669.54) * mm});
            skLineSegment(sketch, "E638", {"start": v(-1215.69, -1669.54) * mm, "end": v(-1229.4, -1675.64) * mm});
            skLineSegment(sketch, "E639", {"start": v(-1229.4, -1675.64) * mm, "end": v(-1243.56, -1681.68) * mm});
            skLineSegment(sketch, "E640", {"start": v(-1243.56, -1681.68) * mm, "end": v(-1258.15, -1687.66) * mm});
            skLineSegment(sketch, "E641", {"start": v(-1258.15, -1687.66) * mm, "end": v(-1273.18, -1693.57) * mm});
            skLineSegment(sketch, "E642", {"start": v(-1273.18, -1693.57) * mm, "end": v(-1288.65, -1699.4) * mm});
            skLineSegment(sketch, "E643", {"start": v(-1288.65, -1699.4) * mm, "end": v(-1304.56, -1705.12) * mm});
            skLineSegment(sketch, "E644", {"start": v(-1304.56, -1705.12) * mm, "end": v(-1320.92, -1710.74) * mm});
            skLineSegment(sketch, "E645", {"start": v(-1320.92, -1710.74) * mm, "end": v(-1337.7, -1716.23) * mm});
            skLineSegment(sketch, "E646", {"start": v(-1337.7, -1716.23) * mm, "end": v(-1350.8, -1716.33) * mm});
            skLineSegment(sketch, "E647", {"start": v(-1350.8, -1716.33) * mm, "end": v(-1401.6, -1675.1) * mm});
            skLineSegment(sketch, "E648", {"start": v(-1401.6, -1675.1) * mm, "end": v(-1404.2, -1662.27) * mm});
            skLineSegment(sketch, "E649", {"start": v(-1404.2, -1662.27) * mm, "end": v(-1402.28, -1644.7) * mm});
            skLineSegment(sketch, "E650", {"start": v(-1402.28, -1644.7) * mm, "end": v(-1400.14, -1627.55) * mm});
            skLineSegment(sketch, "E651", {"start": v(-1400.14, -1627.55) * mm, "end": v(-1397.82, -1610.8) * mm});
            skLineSegment(sketch, "E652", {"start": v(-1397.82, -1610.8) * mm, "end": v(-1395.3, -1594.46) * mm});
            skLineSegment(sketch, "E653", {"start": v(-1395.3, -1594.46) * mm, "end": v(-1392.61, -1578.54) * mm});
            skLineSegment(sketch, "E654", {"start": v(-1392.61, -1578.54) * mm, "end": v(-1389.76, -1563.03) * mm});
            skLineSegment(sketch, "E655", {"start": v(-1389.76, -1563.03) * mm, "end": v(-1386.76, -1547.93) * mm});
            skLineSegment(sketch, "E656", {"start": v(-1386.76, -1547.93) * mm, "end": v(-1383.62, -1533.25) * mm});
            skLineSegment(sketch, "E657", {"start": v(-1383.62, -1533.25) * mm, "end": v(-1380.35, -1519) * mm});
            skLineSegment(sketch, "E658", {"start": v(-1380.35, -1519) * mm, "end": v(-1376.96, -1505.15) * mm});
            skLineSegment(sketch, "E659", {"start": v(-1376.96, -1505.15) * mm, "end": v(-1373.47, -1491.73) * mm});
            skLineSegment(sketch, "E660", {"start": v(-1373.47, -1491.73) * mm, "end": v(-1369.89, -1478.72) * mm});
            skLineSegment(sketch, "E661", {"start": v(-1369.89, -1478.72) * mm, "end": v(-1366.22, -1466.14) * mm});
            skLineSegment(sketch, "E662", {"start": v(-1366.22, -1466.14) * mm, "end": v(-1362.48, -1453.97) * mm});
            skLineSegment(sketch, "E663", {"start": v(-1362.48, -1453.97) * mm, "end": v(-1358.68, -1442.22) * mm});
            skLineSegment(sketch, "E664", {"start": v(-1358.68, -1442.22) * mm, "end": v(-1354.83, -1430.88) * mm});
            skLineSegment(sketch, "E665", {"start": v(-1354.83, -1430.88) * mm, "end": v(-1350.95, -1419.96) * mm});
            skLineSegment(sketch, "E666", {"start": v(-1350.95, -1419.96) * mm, "end": v(-1347.04, -1409.46) * mm});
            skLineSegment(sketch, "E667", {"start": v(-1347.04, -1409.46) * mm, "end": v(-1343.11, -1399.36) * mm});
            skLineSegment(sketch, "E668", {"start": v(-1343.11, -1399.36) * mm, "end": v(-1339.18, -1389.68) * mm});
            skLineSegment(sketch, "E669", {"start": v(-1339.18, -1389.68) * mm, "end": v(-1335.26, -1380.4) * mm});
            skLineSegment(sketch, "E670", {"start": v(-1335.26, -1380.4) * mm, "end": v(-1331.36, -1371.53) * mm});
            skLineSegment(sketch, "E671", {"start": v(-1331.36, -1371.53) * mm, "end": v(-1327.49, -1363.07) * mm});
            skLineSegment(sketch, "E672", {"start": v(-1327.49, -1363.07) * mm, "end": v(-1323.66, -1355) * mm});
            skLineSegment(sketch, "E673", {"start": v(-1323.66, -1355) * mm, "end": v(-1319.87, -1347.33) * mm});
            skLineSegment(sketch, "E674", {"start": v(-1319.87, -1347.33) * mm, "end": v(-1316.16, -1340.06) * mm});
            skLineSegment(sketch, "E675", {"start": v(-1316.16, -1340.06) * mm, "end": v(-1312.5, -1333.18) * mm});
            skLineSegment(sketch, "E676", {"start": v(-1312.5, -1333.18) * mm, "end": v(-1308.94, -1326.68) * mm});
            skLineSegment(sketch, "E677", {"start": v(-1308.94, -1326.68) * mm, "end": v(-1305.47, -1320.57) * mm});
            skLineSegment(sketch, "E678", {"start": v(-1305.47, -1320.57) * mm, "end": v(-1302.1, -1314.83) * mm});
            skLineSegment(sketch, "E679", {"start": v(-1302.1, -1314.83) * mm, "end": v(-1298.86, -1309.47) * mm});
            skLineSegment(sketch, "E680", {"start": v(-1298.86, -1309.47) * mm, "end": v(-1295.73, -1304.48) * mm});
            skLineSegment(sketch, "E681", {"start": v(-1295.73, -1304.48) * mm, "end": v(-1292.73, -1299.85) * mm});
            skLineSegment(sketch, "E682", {"start": v(-1292.73, -1299.85) * mm, "end": v(-1289.88, -1295.59) * mm});
            skLineSegment(sketch, "E683", {"start": v(-1289.88, -1295.59) * mm, "end": v(-1287.19, -1291.68) * mm});
            skLineSegment(sketch, "E684", {"start": v(-1287.19, -1291.68) * mm, "end": v(-1289, -1289) * mm});
            skLineSegment(sketch, "E685", {"start": v(-1289, -1289) * mm, "end": v(-1357.32, -1216.84) * mm});
            skLineSegment(sketch, "E686", {"start": v(-1357.32, -1216.84) * mm, "end": v(-1359.9, -1214.89) * mm});
            skLineSegment(sketch, "E687", {"start": v(-1359.9, -1214.89) * mm, "end": v(-1363.95, -1217.37) * mm});
            skLineSegment(sketch, "E688", {"start": v(-1363.95, -1217.37) * mm, "end": v(-1368.37, -1219.98) * mm});
            skLineSegment(sketch, "E689", {"start": v(-1368.37, -1219.98) * mm, "end": v(-1373.15, -1222.72) * mm});
            skLineSegment(sketch, "E690", {"start": v(-1373.15, -1222.72) * mm, "end": v(-1378.3, -1225.57) * mm});
            skLineSegment(sketch, "E691", {"start": v(-1378.3, -1225.57) * mm, "end": v(-1383.83, -1228.52) * mm});
            skLineSegment(sketch, "E692", {"start": v(-1383.83, -1228.52) * mm, "end": v(-1389.74, -1231.57) * mm});
            skLineSegment(sketch, "E693", {"start": v(-1389.74, -1231.57) * mm, "end": v(-1396.04, -1234.7) * mm});
            skLineSegment(sketch, "E694", {"start": v(-1396.04, -1234.7) * mm, "end": v(-1402.72, -1237.9) * mm});
            skLineSegment(sketch, "E695", {"start": v(-1402.72, -1237.9) * mm, "end": v(-1409.8, -1241.17) * mm});
            skLineSegment(sketch, "E696", {"start": v(-1409.8, -1241.17) * mm, "end": v(-1417.26, -1244.5) * mm});
            skLineSegment(sketch, "E697", {"start": v(-1417.26, -1244.5) * mm, "end": v(-1425.12, -1247.85) * mm});
            skLineSegment(sketch, "E698", {"start": v(-1425.12, -1247.85) * mm, "end": v(-1433.38, -1251.24) * mm});
            skLineSegment(sketch, "E699", {"start": v(-1433.38, -1251.24) * mm, "end": v(-1442.05, -1254.64) * mm});
            skLineSegment(sketch, "E700", {"start": v(-1442.05, -1254.64) * mm, "end": v(-1451.12, -1258.06) * mm});
            skLineSegment(sketch, "E701", {"start": v(-1451.12, -1258.06) * mm, "end": v(-1460.6, -1261.47) * mm});
            skLineSegment(sketch, "E702", {"start": v(-1460.6, -1261.47) * mm, "end": v(-1470.48, -1264.86) * mm});
            skLineSegment(sketch, "E703", {"start": v(-1470.48, -1264.86) * mm, "end": v(-1480.77, -1268.23) * mm});
            skLineSegment(sketch, "E704", {"start": v(-1480.77, -1268.23) * mm, "end": v(-1491.47, -1271.56) * mm});
            skLineSegment(sketch, "E705", {"start": v(-1491.47, -1271.56) * mm, "end": v(-1502.59, -1274.84) * mm});
            skLineSegment(sketch, "E706", {"start": v(-1502.59, -1274.84) * mm, "end": v(-1514.11, -1278.07) * mm});
            skLineSegment(sketch, "E707", {"start": v(-1514.11, -1278.07) * mm, "end": v(-1526.06, -1281.22) * mm});
            skLineSegment(sketch, "E708", {"start": v(-1526.06, -1281.22) * mm, "end": v(-1538.41, -1284.3) * mm});
            skLineSegment(sketch, "E709", {"start": v(-1538.41, -1284.3) * mm, "end": v(-1551.18, -1287.27) * mm});
            skLineSegment(sketch, "E710", {"start": v(-1551.18, -1287.27) * mm, "end": v(-1564.36, -1290.14) * mm});
            skLineSegment(sketch, "E711", {"start": v(-1564.36, -1290.14) * mm, "end": v(-1577.95, -1292.9) * mm});
            skLineSegment(sketch, "E712", {"start": v(-1577.95, -1292.9) * mm, "end": v(-1591.96, -1295.52) * mm});
            skLineSegment(sketch, "E713", {"start": v(-1591.96, -1295.52) * mm, "end": v(-1606.38, -1298.01) * mm});
            skLineSegment(sketch, "E714", {"start": v(-1606.38, -1298.01) * mm, "end": v(-1621.2, -1300.35) * mm});
            skLineSegment(sketch, "E715", {"start": v(-1621.2, -1300.35) * mm, "end": v(-1636.44, -1302.52) * mm});
            skLineSegment(sketch, "E716", {"start": v(-1636.44, -1302.52) * mm, "end": v(-1652.08, -1304.52) * mm});
            skLineSegment(sketch, "E717", {"start": v(-1652.08, -1304.52) * mm, "end": v(-1668.13, -1306.34) * mm});
            skLineSegment(sketch, "E718", {"start": v(-1668.13, -1306.34) * mm, "end": v(-1684.58, -1307.96) * mm});
            skLineSegment(sketch, "E719", {"start": v(-1684.58, -1307.96) * mm, "end": v(-1701.43, -1309.37) * mm});
            skLineSegment(sketch, "E720", {"start": v(-1701.43, -1309.37) * mm, "end": v(-1718.68, -1310.57) * mm});
            skLineSegment(sketch, "E721", {"start": v(-1718.68, -1310.57) * mm, "end": v(-1736.32, -1311.53) * mm});
            skLineSegment(sketch, "E722", {"start": v(-1736.32, -1311.53) * mm, "end": v(-1748.99, -1308.24) * mm});
            skLineSegment(sketch, "E723", {"start": v(-1748.99, -1308.24) * mm, "end": v(-1787.4, -1255.26) * mm});
            skLineSegment(sketch, "E724", {"start": v(-1787.4, -1255.26) * mm, "end": v(-1786.58, -1242.2) * mm});
            skLineSegment(sketch, "E725", {"start": v(-1786.58, -1242.2) * mm, "end": v(-1780.18, -1225.73) * mm});
            skLineSegment(sketch, "E726", {"start": v(-1780.18, -1225.73) * mm, "end": v(-1773.68, -1209.7) * mm});
            skLineSegment(sketch, "E727", {"start": v(-1773.68, -1209.7) * mm, "end": v(-1767.1, -1194.13) * mm});
            skLineSegment(sketch, "E728", {"start": v(-1767.1, -1194.13) * mm, "end": v(-1760.44, -1179) * mm});
            skLineSegment(sketch, "E729", {"start": v(-1760.44, -1179) * mm, "end": v(-1753.72, -1164.31) * mm});
            skLineSegment(sketch, "E730", {"start": v(-1753.72, -1164.31) * mm, "end": v(-1746.95, -1150.07) * mm});
            skLineSegment(sketch, "E731", {"start": v(-1746.95, -1150.07) * mm, "end": v(-1740.14, -1136.27) * mm});
            skLineSegment(sketch, "E732", {"start": v(-1740.14, -1136.27) * mm, "end": v(-1733.3, -1122.9) * mm});
            skLineSegment(sketch, "E733", {"start": v(-1733.3, -1122.9) * mm, "end": v(-1726.46, -1109.98) * mm});
            skLineSegment(sketch, "E734", {"start": v(-1726.46, -1109.98) * mm, "end": v(-1719.6, -1097.48) * mm});
            skLineSegment(sketch, "E735", {"start": v(-1719.6, -1097.48) * mm, "end": v(-1712.76, -1085.42) * mm});
            skLineSegment(sketch, "E736", {"start": v(-1712.76, -1085.42) * mm, "end": v(-1705.93, -1073.79) * mm});
            skLineSegment(sketch, "E737", {"start": v(-1705.93, -1073.79) * mm, "end": v(-1699.13, -1062.58) * mm});
            skLineSegment(sketch, "E738", {"start": v(-1699.13, -1062.58) * mm, "end": v(-1692.37, -1051.8) * mm});
            skLineSegment(sketch, "E739", {"start": v(-1692.37, -1051.8) * mm, "end": v(-1685.66, -1041.42) * mm});
            skLineSegment(sketch, "E740", {"start": v(-1685.66, -1041.42) * mm, "end": v(-1679, -1031.47) * mm});
            skLineSegment(sketch, "E741", {"start": v(-1679, -1031.47) * mm, "end": v(-1672.43, -1021.93) * mm});
            skLineSegment(sketch, "E742", {"start": v(-1672.43, -1021.93) * mm, "end": v(-1665.93, -1012.8) * mm});
            skLineSegment(sketch, "E743", {"start": v(-1665.93, -1012.8) * mm, "end": v(-1659.53, -1004.06) * mm});
            skLineSegment(sketch, "E744", {"start": v(-1659.53, -1004.06) * mm, "end": v(-1653.23, -995.72) * mm});
            skLineSegment(sketch, "E745", {"start": v(-1653.23, -995.72) * mm, "end": v(-1647.04, -987.78) * mm});
            skLineSegment(sketch, "E746", {"start": v(-1647.04, -987.78) * mm, "end": v(-1640.98, -980.22) * mm});
            skLineSegment(sketch, "E747", {"start": v(-1640.98, -980.22) * mm, "end": v(-1635.04, -973.04) * mm});
            skLineSegment(sketch, "E748", {"start": v(-1635.04, -973.04) * mm, "end": v(-1629.25, -966.24) * mm});
            skLineSegment(sketch, "E749", {"start": v(-1629.25, -966.24) * mm, "end": v(-1623.62, -959.82) * mm});
            skLineSegment(sketch, "E750", {"start": v(-1623.62, -959.82) * mm, "end": v(-1618.14, -953.75) * mm});
            skLineSegment(sketch, "E751", {"start": v(-1618.14, -953.75) * mm, "end": v(-1612.84, -948.05) * mm});
            skLineSegment(sketch, "E752", {"start": v(-1612.84, -948.05) * mm, "end": v(-1607.71, -942.7) * mm});
            skLineSegment(sketch, "E753", {"start": v(-1607.71, -942.7) * mm, "end": v(-1602.78, -937.69) * mm});
            skLineSegment(sketch, "E754", {"start": v(-1602.78, -937.69) * mm, "end": v(-1598.04, -933.02) * mm});
            skLineSegment(sketch, "E755", {"start": v(-1598.04, -933.02) * mm, "end": v(-1593.51, -928.68) * mm});
            skLineSegment(sketch, "E756", {"start": v(-1593.51, -928.68) * mm, "end": v(-1589.2, -924.67) * mm});
            skLineSegment(sketch, "E757", {"start": v(-1589.2, -924.67) * mm, "end": v(-1585.11, -920.98) * mm});
            skLineSegment(sketch, "E758", {"start": v(-1585.11, -920.98) * mm, "end": v(-1581.25, -917.6) * mm});
            skLineSegment(sketch, "E759", {"start": v(-1581.25, -917.6) * mm, "end": v(-1577.64, -914.51) * mm});
            skLineSegment(sketch, "E760", {"start": v(-1577.64, -914.51) * mm, "end": v(-1578.69, -911.46) * mm});
            skLineSegment(sketch, "E761", {"start": v(-1578.69, -911.46) * mm, "end": v(-1626.01, -824.07) * mm});
            skLineSegment(sketch, "E762", {"start": v(-1626.01, -824.07) * mm, "end": v(-1628, -821.52) * mm});
            skLineSegment(sketch, "E763", {"start": v(-1628, -821.52) * mm, "end": v(-1632.56, -822.87) * mm});
            skLineSegment(sketch, "E764", {"start": v(-1632.56, -822.87) * mm, "end": v(-1637.5, -824.25) * mm});
            skLineSegment(sketch, "E765", {"start": v(-1637.5, -824.25) * mm, "end": v(-1642.82, -825.66) * mm});
            skLineSegment(sketch, "E766", {"start": v(-1642.82, -825.66) * mm, "end": v(-1648.54, -827.08) * mm});
            skLineSegment(sketch, "E767", {"start": v(-1648.54, -827.08) * mm, "end": v(-1654.65, -828.5) * mm});
            skLineSegment(sketch, "E768", {"start": v(-1654.65, -828.5) * mm, "end": v(-1661.14, -829.92) * mm});
            skLineSegment(sketch, "E769", {"start": v(-1661.14, -829.92) * mm, "end": v(-1668.03, -831.31) * mm});
            skLineSegment(sketch, "E770", {"start": v(-1668.03, -831.31) * mm, "end": v(-1675.32, -832.68) * mm});
            skLineSegment(sketch, "E771", {"start": v(-1675.32, -832.68) * mm, "end": v(-1683, -834) * mm});
            skLineSegment(sketch, "E772", {"start": v(-1683, -834) * mm, "end": v(-1691.06, -835.27) * mm});
            skLineSegment(sketch, "E773", {"start": v(-1691.06, -835.27) * mm, "end": v(-1699.53, -836.48) * mm});
            skLineSegment(sketch, "E774", {"start": v(-1699.53, -836.48) * mm, "end": v(-1708.39, -837.62) * mm});
            skLineSegment(sketch, "E775", {"start": v(-1708.39, -837.62) * mm, "end": v(-1717.64, -838.66) * mm});
            skLineSegment(sketch, "E776", {"start": v(-1717.64, -838.66) * mm, "end": v(-1727.28, -839.61) * mm});
            skLineSegment(sketch, "E777", {"start": v(-1727.28, -839.61) * mm, "end": v(-1737.32, -840.45) * mm});
            skLineSegment(sketch, "E778", {"start": v(-1737.32, -840.45) * mm, "end": v(-1747.74, -841.17) * mm});
            skLineSegment(sketch, "E779", {"start": v(-1747.74, -841.17) * mm, "end": v(-1758.55, -841.76) * mm});
            skLineSegment(sketch, "E780", {"start": v(-1758.55, -841.76) * mm, "end": v(-1769.76, -842.21) * mm});
            skLineSegment(sketch, "E781", {"start": v(-1769.76, -842.21) * mm, "end": v(-1781.34, -842.5) * mm});
            skLineSegment(sketch, "E782", {"start": v(-1781.34, -842.5) * mm, "end": v(-1793.31, -842.64) * mm});
            skLineSegment(sketch, "E783", {"start": v(-1793.31, -842.64) * mm, "end": v(-1805.66, -842.6) * mm});
            skLineSegment(sketch, "E784", {"start": v(-1805.66, -842.6) * mm, "end": v(-1818.39, -842.36) * mm});
            skLineSegment(sketch, "E785", {"start": v(-1818.39, -842.36) * mm, "end": v(-1831.5, -841.93) * mm});
            skLineSegment(sketch, "E786", {"start": v(-1831.5, -841.93) * mm, "end": v(-1844.97, -841.3) * mm});
            skLineSegment(sketch, "E787", {"start": v(-1844.97, -841.3) * mm, "end": v(-1858.81, -840.44) * mm});
            skLineSegment(sketch, "E788", {"start": v(-1858.81, -840.44) * mm, "end": v(-1873.02, -839.35) * mm});
            skLineSegment(sketch, "E789", {"start": v(-1873.02, -839.35) * mm, "end": v(-1887.59, -838.02) * mm});
            skLineSegment(sketch, "E790", {"start": v(-1887.59, -838.02) * mm, "end": v(-1902.52, -836.44) * mm});
            skLineSegment(sketch, "E791", {"start": v(-1902.52, -836.44) * mm, "end": v(-1917.8, -834.6) * mm});
            skLineSegment(sketch, "E792", {"start": v(-1917.8, -834.6) * mm, "end": v(-1933.42, -832.48) * mm});
            skLineSegment(sketch, "E793", {"start": v(-1933.42, -832.48) * mm, "end": v(-1949.4, -830.08) * mm});
            skLineSegment(sketch, "E794", {"start": v(-1949.4, -830.08) * mm, "end": v(-1965.7, -827.4) * mm});
            skLineSegment(sketch, "E795", {"start": v(-1965.7, -827.4) * mm, "end": v(-1982.35, -824.4) * mm});
            skLineSegment(sketch, "E796", {"start": v(-1982.35, -824.4) * mm, "end": v(-1999.32, -821.08) * mm});
            skLineSegment(sketch, "E797", {"start": v(-1999.32, -821.08) * mm, "end": v(-2016.6, -817.45) * mm});
            skLineSegment(sketch, "E798", {"start": v(-2016.6, -817.45) * mm, "end": v(-2028, -810.99) * mm});
            skLineSegment(sketch, "E799", {"start": v(-2028, -810.99) * mm, "end": v(-2051.37, -749.88) * mm});
            skLineSegment(sketch, "E800", {"start": v(-2051.37, -749.88) * mm, "end": v(-2047.2, -737.47) * mm});
            skLineSegment(sketch, "E801", {"start": v(-2047.2, -737.47) * mm, "end": v(-2036.76, -723.22) * mm});
            skLineSegment(sketch, "E802", {"start": v(-2036.76, -723.22) * mm, "end": v(-2026.34, -709.43) * mm});
            skLineSegment(sketch, "E803", {"start": v(-2026.34, -709.43) * mm, "end": v(-2015.94, -696.09) * mm});
            skLineSegment(sketch, "E804", {"start": v(-2015.94, -696.09) * mm, "end": v(-2005.6, -683.2) * mm});
            skLineSegment(sketch, "E805", {"start": v(-2005.6, -683.2) * mm, "end": v(-1995.3, -670.75) * mm});
            skLineSegment(sketch, "E806", {"start": v(-1995.3, -670.75) * mm, "end": v(-1985.08, -658.74) * mm});
            skLineSegment(sketch, "E807", {"start": v(-1985.08, -658.74) * mm, "end": v(-1974.94, -647.17) * mm});
            skLineSegment(sketch, "E808", {"start": v(-1974.94, -647.17) * mm, "end": v(-1964.88, -636.03) * mm});
            skLineSegment(sketch, "E809", {"start": v(-1964.88, -636.03) * mm, "end": v(-1954.91, -625.31) * mm});
            skLineSegment(sketch, "E810", {"start": v(-1954.91, -625.31) * mm, "end": v(-1945.06, -615.02) * mm});
            skLineSegment(sketch, "E811", {"start": v(-1945.06, -615.02) * mm, "end": v(-1935.33, -605.14) * mm});
            skLineSegment(sketch, "E812", {"start": v(-1935.33, -605.14) * mm, "end": v(-1925.72, -595.67) * mm});
            skLineSegment(sketch, "E813", {"start": v(-1925.72, -595.67) * mm, "end": v(-1916.25, -586.6) * mm});
            skLineSegment(sketch, "E814", {"start": v(-1916.25, -586.6) * mm, "end": v(-1906.92, -577.94) * mm});
            skLineSegment(sketch, "E815", {"start": v(-1906.92, -577.94) * mm, "end": v(-1897.76, -569.66) * mm});
            skLineSegment(sketch, "E816", {"start": v(-1897.76, -569.66) * mm, "end": v(-1888.76, -561.77) * mm});
            skLineSegment(sketch, "E817", {"start": v(-1888.76, -561.77) * mm, "end": v(-1879.94, -554.25) * mm});
            skLineSegment(sketch, "E818", {"start": v(-1879.94, -554.25) * mm, "end": v(-1871.3, -547.1) * mm});
            skLineSegment(sketch, "E819", {"start": v(-1871.3, -547.1) * mm, "end": v(-1862.85, -540.33) * mm});
            skLineSegment(sketch, "E820", {"start": v(-1862.85, -540.33) * mm, "end": v(-1854.6, -533.9) * mm});
            skLineSegment(sketch, "E821", {"start": v(-1854.6, -533.9) * mm, "end": v(-1846.57, -527.83) * mm});
            skLineSegment(sketch, "E822", {"start": v(-1846.57, -527.83) * mm, "end": v(-1838.76, -522.1) * mm});
            skLineSegment(sketch, "E823", {"start": v(-1838.76, -522.1) * mm, "end": v(-1831.17, -516.7) * mm});
            skLineSegment(sketch, "E824", {"start": v(-1831.17, -516.7) * mm, "end": v(-1823.82, -511.64) * mm});
            skLineSegment(sketch, "E825", {"start": v(-1823.82, -511.64) * mm, "end": v(-1816.71, -506.89) * mm});
            skLineSegment(sketch, "E826", {"start": v(-1816.71, -506.89) * mm, "end": v(-1809.85, -502.45) * mm});
            skLineSegment(sketch, "E827", {"start": v(-1809.85, -502.45) * mm, "end": v(-1803.25, -498.31) * mm});
            skLineSegment(sketch, "E828", {"start": v(-1803.25, -498.31) * mm, "end": v(-1796.92, -494.47) * mm});
            skLineSegment(sketch, "E829", {"start": v(-1796.92, -494.47) * mm, "end": v(-1790.86, -490.9) * mm});
            skLineSegment(sketch, "E830", {"start": v(-1790.86, -490.9) * mm, "end": v(-1785.07, -487.62) * mm});
            skLineSegment(sketch, "E831", {"start": v(-1785.07, -487.62) * mm, "end": v(-1779.58, -484.6) * mm});
            skLineSegment(sketch, "E832", {"start": v(-1779.58, -484.6) * mm, "end": v(-1774.37, -481.85) * mm});
            skLineSegment(sketch, "E833", {"start": v(-1774.37, -481.85) * mm, "end": v(-1769.47, -479.34) * mm});
            skLineSegment(sketch, "E834", {"start": v(-1769.47, -479.34) * mm, "end": v(-1764.87, -477.07) * mm});
            skLineSegment(sketch, "E835", {"start": v(-1764.87, -477.07) * mm, "end": v(-1760.58, -475.03) * mm});
            skLineSegment(sketch, "E836", {"start": v(-1760.58, -475.03) * mm, "end": v(-1760.8, -471.8) * mm});
            skLineSegment(sketch, "E837", {"start": v(-1760.8, -471.8) * mm, "end": v(-1783.9, -375.15) * mm});
            skLineSegment(sketch, "E838", {"start": v(-1783.9, -375.15) * mm, "end": v(-1785.15, -372.17) * mm});
            skLineSegment(sketch, "E839", {"start": v(-1785.15, -372.17) * mm, "end": v(-1789.9, -372.3) * mm});
            skLineSegment(sketch, "E840", {"start": v(-1789.9, -372.3) * mm, "end": v(-1795.03, -372.35) * mm});
            skLineSegment(sketch, "E841", {"start": v(-1795.03, -372.35) * mm, "end": v(-1800.54, -372.33) * mm});
            skLineSegment(sketch, "E842", {"start": v(-1800.54, -372.33) * mm, "end": v(-1806.43, -372.22) * mm});
            skLineSegment(sketch, "E843", {"start": v(-1806.43, -372.22) * mm, "end": v(-1812.7, -372.02) * mm});
            skLineSegment(sketch, "E844", {"start": v(-1812.7, -372.02) * mm, "end": v(-1819.34, -371.7) * mm});
            skLineSegment(sketch, "E845", {"start": v(-1819.34, -371.7) * mm, "end": v(-1826.36, -371.27) * mm});
            skLineSegment(sketch, "E846", {"start": v(-1826.36, -371.27) * mm, "end": v(-1833.74, -370.7) * mm});
            skLineSegment(sketch, "E847", {"start": v(-1833.74, -370.7) * mm, "end": v(-1841.5, -370) * mm});
            skLineSegment(sketch, "E848", {"start": v(-1841.5, -370) * mm, "end": v(-1849.63, -369.13) * mm});
            skLineSegment(sketch, "E849", {"start": v(-1849.63, -369.13) * mm, "end": v(-1858.12, -368.1) * mm});
            skLineSegment(sketch, "E850", {"start": v(-1858.12, -368.1) * mm, "end": v(-1866.96, -366.91) * mm});
            skLineSegment(sketch, "E851", {"start": v(-1866.96, -366.91) * mm, "end": v(-1876.17, -365.53) * mm});
            skLineSegment(sketch, "E852", {"start": v(-1876.17, -365.53) * mm, "end": v(-1885.73, -363.95) * mm});
            skLineSegment(sketch, "E853", {"start": v(-1885.73, -363.95) * mm, "end": v(-1895.64, -362.16) * mm});
            skLineSegment(sketch, "E854", {"start": v(-1895.64, -362.16) * mm, "end": v(-1905.9, -360.16) * mm});
            skLineSegment(sketch, "E855", {"start": v(-1905.9, -360.16) * mm, "end": v(-1916.5, -357.93) * mm});
            skLineSegment(sketch, "E856", {"start": v(-1916.5, -357.93) * mm, "end": v(-1927.43, -355.47) * mm});
            skLineSegment(sketch, "E857", {"start": v(-1927.43, -355.47) * mm, "end": v(-1938.7, -352.75) * mm});
            skLineSegment(sketch, "E858", {"start": v(-1938.7, -352.75) * mm, "end": v(-1950.3, -349.78) * mm});
            skLineSegment(sketch, "E859", {"start": v(-1950.3, -349.78) * mm, "end": v(-1962.21, -346.54) * mm});
            skLineSegment(sketch, "E860", {"start": v(-1962.21, -346.54) * mm, "end": v(-1974.45, -343.02) * mm});
            skLineSegment(sketch, "E861", {"start": v(-1974.45, -343.02) * mm, "end": v(-1987, -339.22) * mm});
            skLineSegment(sketch, "E862", {"start": v(-1987, -339.22) * mm, "end": v(-1999.84, -335.11) * mm});
            skLineSegment(sketch, "E863", {"start": v(-1999.84, -335.11) * mm, "end": v(-2013, -330.7) * mm});
            skLineSegment(sketch, "E864", {"start": v(-2013, -330.7) * mm, "end": v(-2026.44, -325.98) * mm});
            skLineSegment(sketch, "E865", {"start": v(-2026.44, -325.98) * mm, "end": v(-2040.17, -320.92) * mm});
            skLineSegment(sketch, "E866", {"start": v(-2040.17, -320.92) * mm, "end": v(-2054.18, -315.53) * mm});
            skLineSegment(sketch, "E867", {"start": v(-2054.18, -315.53) * mm, "end": v(-2068.46, -309.8) * mm});
            skLineSegment(sketch, "E868", {"start": v(-2068.46, -309.8) * mm, "end": v(-2083, -303.71) * mm});
            skLineSegment(sketch, "E869", {"start": v(-2083, -303.71) * mm, "end": v(-2097.81, -297.26) * mm});
            skLineSegment(sketch, "E870", {"start": v(-2097.81, -297.26) * mm, "end": v(-2112.87, -290.44) * mm});
            skLineSegment(sketch, "E871", {"start": v(-2112.87, -290.44) * mm, "end": v(-2128.17, -283.24) * mm});
            skLineSegment(sketch, "E872", {"start": v(-2128.17, -283.24) * mm, "end": v(-2143.7, -275.64) * mm});
            skLineSegment(sketch, "E873", {"start": v(-2143.7, -275.64) * mm, "end": v(-2159.46, -267.66) * mm});
            skLineSegment(sketch, "E874", {"start": v(-2159.46, -267.66) * mm, "end": v(-2168.79, -258.47) * mm});
            skLineSegment(sketch, "E875", {"start": v(-2168.79, -258.47) * mm, "end": v(-2175.56, -193.4) * mm});
            skLineSegment(sketch, "E876", {"start": v(-2175.56, -193.4) * mm, "end": v(-2168.32, -182.48) * mm});
            skLineSegment(sketch, "E877", {"start": v(-2168.32, -182.48) * mm, "end": v(-2154.54, -171.42) * mm});
            skLineSegment(sketch, "E878", {"start": v(-2154.54, -171.42) * mm, "end": v(-2140.9, -160.8) * mm});
            skLineSegment(sketch, "E879", {"start": v(-2140.9, -160.8) * mm, "end": v(-2127.41, -150.6) * mm});
            skLineSegment(sketch, "E880", {"start": v(-2127.41, -150.6) * mm, "end": v(-2114.08, -140.83) * mm});
            skLineSegment(sketch, "E881", {"start": v(-2114.08, -140.83) * mm, "end": v(-2100.92, -131.47) * mm});
            skLineSegment(sketch, "E882", {"start": v(-2100.92, -131.47) * mm, "end": v(-2087.94, -122.52) * mm});
            skLineSegment(sketch, "E883", {"start": v(-2087.94, -122.52) * mm, "end": v(-2075.14, -113.97) * mm});
            skLineSegment(sketch, "E884", {"start": v(-2075.14, -113.97) * mm, "end": v(-2062.54, -105.8) * mm});
            skLineSegment(sketch, "E885", {"start": v(-2062.54, -105.8) * mm, "end": v(-2050.15, -98.04) * mm});
            skLineSegment(sketch, "E886", {"start": v(-2050.15, -98.04) * mm, "end": v(-2037.96, -90.64) * mm});
            skLineSegment(sketch, "E887", {"start": v(-2037.96, -90.64) * mm, "end": v(-2026, -83.62) * mm});
            skLineSegment(sketch, "E888", {"start": v(-2026, -83.62) * mm, "end": v(-2014.27, -76.96) * mm});
            skLineSegment(sketch, "E889", {"start": v(-2014.27, -76.96) * mm, "end": v(-2002.78, -70.66) * mm});
            skLineSegment(sketch, "E890", {"start": v(-2002.78, -70.66) * mm, "end": v(-1991.53, -64.7) * mm});
            skLineSegment(sketch, "E891", {"start": v(-1991.53, -64.7) * mm, "end": v(-1980.53, -59.07) * mm});
            skLineSegment(sketch, "E892", {"start": v(-1980.53, -59.07) * mm, "end": v(-1969.8, -53.78) * mm});
            skLineSegment(sketch, "E893", {"start": v(-1969.8, -53.78) * mm, "end": v(-1959.33, -48.8) * mm});
            skLineSegment(sketch, "E894", {"start": v(-1959.33, -48.8) * mm, "end": v(-1949.14, -44.14) * mm});
            skLineSegment(sketch, "E895", {"start": v(-1949.14, -44.14) * mm, "end": v(-1939.22, -39.78) * mm});
            skLineSegment(sketch, "E896", {"start": v(-1939.22, -39.78) * mm, "end": v(-1929.6, -35.7) * mm});
            skLineSegment(sketch, "E897", {"start": v(-1929.6, -35.7) * mm, "end": v(-1920.27, -31.92) * mm});
            skLineSegment(sketch, "E898", {"start": v(-1920.27, -31.92) * mm, "end": v(-1911.24, -28.4) * mm});
            skLineSegment(sketch, "E899", {"start": v(-1911.24, -28.4) * mm, "end": v(-1902.51, -25.16) * mm});
            skLineSegment(sketch, "E900", {"start": v(-1902.51, -25.16) * mm, "end": v(-1894.1, -22.17) * mm});
            skLineSegment(sketch, "E901", {"start": v(-1894.1, -22.17) * mm, "end": v(-1886, -19.42) * mm});
            skLineSegment(sketch, "E902", {"start": v(-1886, -19.42) * mm, "end": v(-1878.23, -16.9) * mm});
            skLineSegment(sketch, "E903", {"start": v(-1878.23, -16.9) * mm, "end": v(-1870.78, -14.61) * mm});
            skLineSegment(sketch, "E904", {"start": v(-1870.78, -14.61) * mm, "end": v(-1863.67, -12.54) * mm});
            skLineSegment(sketch, "E905", {"start": v(-1863.67, -12.54) * mm, "end": v(-1856.9, -10.67) * mm});
            skLineSegment(sketch, "E906", {"start": v(-1856.9, -10.67) * mm, "end": v(-1850.46, -9) * mm});
            skLineSegment(sketch, "E907", {"start": v(-1850.46, -9) * mm, "end": v(-1844.36, -7.5) * mm});
            skLineSegment(sketch, "E908", {"start": v(-1844.36, -7.5) * mm, "end": v(-1838.62, -6.19) * mm});
            skLineSegment(sketch, "E909", {"start": v(-1838.62, -6.19) * mm, "end": v(-1833.24, -5.03) * mm});
            skLineSegment(sketch, "E910", {"start": v(-1833.24, -5.03) * mm, "end": v(-1828.2, -4.03) * mm});
            skLineSegment(sketch, "E911", {"start": v(-1828.2, -4.03) * mm, "end": v(-1823.53, -3.17) * mm});
            skLineSegment(sketch, "E912", {"start": v(-1823.53, -3.17) * mm, "end": v(-1822.91, 0) * mm});
            skLineSegment(sketch, "E913", {"start": v(-1822.91, 0) * mm, "end": v(-1820.2, 99.34) * mm});
            skLineSegment(sketch, "E914", {"start": v(-1820.2, 99.34) * mm, "end": v(-1820.65, 102.54) * mm});
            skLineSegment(sketch, "E915", {"start": v(-1820.65, 102.54) * mm, "end": v(-1825.27, 103.65) * mm});
            skLineSegment(sketch, "E916", {"start": v(-1825.27, 103.65) * mm, "end": v(-1830.24, 104.93) * mm});
            skLineSegment(sketch, "E917", {"start": v(-1830.24, 104.93) * mm, "end": v(-1835.55, 106.37) * mm});
            skLineSegment(sketch, "E918", {"start": v(-1835.55, 106.37) * mm, "end": v(-1841.22, 108) * mm});
            skLineSegment(sketch, "E919", {"start": v(-1841.22, 108) * mm, "end": v(-1847.22, 109.82) * mm});
            skLineSegment(sketch, "E920", {"start": v(-1847.22, 109.82) * mm, "end": v(-1853.55, 111.84) * mm});
            skLineSegment(sketch, "E921", {"start": v(-1853.55, 111.84) * mm, "end": v(-1860.22, 114.08) * mm});
            skLineSegment(sketch, "E922", {"start": v(-1860.22, 114.08) * mm, "end": v(-1867.2, 116.54) * mm});
            skLineSegment(sketch, "E923", {"start": v(-1867.2, 116.54) * mm, "end": v(-1874.52, 119.23) * mm});
            skLineSegment(sketch, "E924", {"start": v(-1874.52, 119.23) * mm, "end": v(-1882.14, 122.16) * mm});
            skLineSegment(sketch, "E925", {"start": v(-1882.14, 122.16) * mm, "end": v(-1890.08, 125.35) * mm});
            skLineSegment(sketch, "E926", {"start": v(-1890.08, 125.35) * mm, "end": v(-1898.31, 128.8) * mm});
            skLineSegment(sketch, "E927", {"start": v(-1898.31, 128.8) * mm, "end": v(-1906.85, 132.52) * mm});
            skLineSegment(sketch, "E928", {"start": v(-1906.85, 132.52) * mm, "end": v(-1915.67, 136.52) * mm});
            skLineSegment(sketch, "E929", {"start": v(-1915.67, 136.52) * mm, "end": v(-1924.79, 140.8) * mm});
            skLineSegment(sketch, "E930", {"start": v(-1924.79, 140.8) * mm, "end": v(-1934.17, 145.4) * mm});
            skLineSegment(sketch, "E931", {"start": v(-1934.17, 145.4) * mm, "end": v(-1943.83, 150.29) * mm});
            skLineSegment(sketch, "E932", {"start": v(-1943.83, 150.29) * mm, "end": v(-1953.76, 155.5) * mm});
            skLineSegment(sketch, "E933", {"start": v(-1953.76, 155.5) * mm, "end": v(-1963.94, 161.04) * mm});
            skLineSegment(sketch, "E934", {"start": v(-1963.94, 161.04) * mm, "end": v(-1974.37, 166.91) * mm});
            skLineSegment(sketch, "E935", {"start": v(-1974.37, 166.91) * mm, "end": v(-1985.04, 173.12) * mm});
            skLineSegment(sketch, "E936", {"start": v(-1985.04, 173.12) * mm, "end": v(-1995.95, 179.69) * mm});
            skLineSegment(sketch, "E937", {"start": v(-1995.95, 179.69) * mm, "end": v(-2007.08, 186.61) * mm});
            skLineSegment(sketch, "E938", {"start": v(-2007.08, 186.61) * mm, "end": v(-2018.44, 193.9) * mm});
            skLineSegment(sketch, "E939", {"start": v(-2018.44, 193.9) * mm, "end": v(-2030, 201.57) * mm});
            skLineSegment(sketch, "E940", {"start": v(-2030, 201.57) * mm, "end": v(-2041.76, 209.61) * mm});
            skLineSegment(sketch, "E941", {"start": v(-2041.76, 209.61) * mm, "end": v(-2053.71, 218.05) * mm});
            skLineSegment(sketch, "E942", {"start": v(-2053.71, 218.05) * mm, "end": v(-2065.85, 226.88) * mm});
            skLineSegment(sketch, "E943", {"start": v(-2065.85, 226.88) * mm, "end": v(-2078.16, 236.11) * mm});
            skLineSegment(sketch, "E944", {"start": v(-2078.16, 236.11) * mm, "end": v(-2090.63, 245.76) * mm});
            skLineSegment(sketch, "E945", {"start": v(-2090.63, 245.76) * mm, "end": v(-2103.27, 255.82) * mm});
            skLineSegment(sketch, "E946", {"start": v(-2103.27, 255.82) * mm, "end": v(-2116.04, 266.3) * mm});
            skLineSegment(sketch, "E947", {"start": v(-2116.04, 266.3) * mm, "end": v(-2128.96, 277.23) * mm});
            skLineSegment(sketch, "E948", {"start": v(-2128.96, 277.23) * mm, "end": v(-2142, 288.58) * mm});
            skLineSegment(sketch, "E949", {"start": v(-2142, 288.58) * mm, "end": v(-2155.16, 300.37) * mm});
            skLineSegment(sketch, "E950", {"start": v(-2155.16, 300.37) * mm, "end": v(-2161.79, 311.66) * mm});
            skLineSegment(sketch, "E951", {"start": v(-2161.79, 311.66) * mm, "end": v(-2151.48, 376.27) * mm});
            skLineSegment(sketch, "E952", {"start": v(-2151.48, 376.27) * mm, "end": v(-2141.67, 384.94) * mm});
            skLineSegment(sketch, "E953", {"start": v(-2141.67, 384.94) * mm, "end": v(-2125.5, 392.05) * mm});
            skLineSegment(sketch, "E954", {"start": v(-2125.5, 392.05) * mm, "end": v(-2109.57, 398.79) * mm});
            skLineSegment(sketch, "E955", {"start": v(-2109.57, 398.79) * mm, "end": v(-2093.9, 405.14) * mm});
            skLineSegment(sketch, "E956", {"start": v(-2093.9, 405.14) * mm, "end": v(-2078.5, 411.14) * mm});
            skLineSegment(sketch, "E957", {"start": v(-2078.5, 411.14) * mm, "end": v(-2063.36, 416.77) * mm});
            skLineSegment(sketch, "E958", {"start": v(-2063.36, 416.77) * mm, "end": v(-2048.5, 422.06) * mm});
            skLineSegment(sketch, "E959", {"start": v(-2048.5, 422.06) * mm, "end": v(-2033.93, 427) * mm});
            skLineSegment(sketch, "E960", {"start": v(-2033.93, 427) * mm, "end": v(-2019.65, 431.62) * mm});
            skLineSegment(sketch, "E961", {"start": v(-2019.65, 431.62) * mm, "end": v(-2005.66, 435.92) * mm});
            skLineSegment(sketch, "E962", {"start": v(-2005.66, 435.92) * mm, "end": v(-1991.98, 439.9) * mm});
            skLineSegment(sketch, "E963", {"start": v(-1991.98, 439.9) * mm, "end": v(-1978.61, 443.6) * mm});
            skLineSegment(sketch, "E964", {"start": v(-1978.61, 443.6) * mm, "end": v(-1965.56, 447) * mm});
            skLineSegment(sketch, "E965", {"start": v(-1965.56, 447) * mm, "end": v(-1952.82, 450.1) * mm});
            skLineSegment(sketch, "E966", {"start": v(-1952.82, 450.1) * mm, "end": v(-1940.41, 452.96) * mm});
            skLineSegment(sketch, "E967", {"start": v(-1940.41, 452.96) * mm, "end": v(-1928.34, 455.54) * mm});
            skLineSegment(sketch, "E968", {"start": v(-1928.34, 455.54) * mm, "end": v(-1916.6, 457.88) * mm});
            skLineSegment(sketch, "E969", {"start": v(-1916.6, 457.88) * mm, "end": v(-1905.2, 459.97) * mm});
            skLineSegment(sketch, "E970", {"start": v(-1905.2, 459.97) * mm, "end": v(-1894.14, 461.84) * mm});
            skLineSegment(sketch, "E971", {"start": v(-1894.14, 461.84) * mm, "end": v(-1883.44, 463.49) * mm});
            skLineSegment(sketch, "E972", {"start": v(-1883.44, 463.49) * mm, "end": v(-1873.1, 464.93) * mm});
            skLineSegment(sketch, "E973", {"start": v(-1873.1, 464.93) * mm, "end": v(-1863.1, 466.17) * mm});
            skLineSegment(sketch, "E974", {"start": v(-1863.1, 466.17) * mm, "end": v(-1853.46, 467.22) * mm});
            skLineSegment(sketch, "E975", {"start": v(-1853.46, 467.22) * mm, "end": v(-1844.2, 468.1) * mm});
            skLineSegment(sketch, "E976", {"start": v(-1844.2, 468.1) * mm, "end": v(-1835.3, 468.82) * mm});
            skLineSegment(sketch, "E977", {"start": v(-1835.3, 468.82) * mm, "end": v(-1826.76, 469.38) * mm});
            skLineSegment(sketch, "E978", {"start": v(-1826.76, 469.38) * mm, "end": v(-1818.6, 469.8) * mm});
            skLineSegment(sketch, "E979", {"start": v(-1818.6, 469.8) * mm, "end": v(-1810.82, 470.08) * mm});
            skLineSegment(sketch, "E980", {"start": v(-1810.82, 470.08) * mm, "end": v(-1803.41, 470.24) * mm});
            skLineSegment(sketch, "E981", {"start": v(-1803.41, 470.24) * mm, "end": v(-1796.38, 470.3) * mm});
            skLineSegment(sketch, "E982", {"start": v(-1796.38, 470.3) * mm, "end": v(-1789.73, 470.24) * mm});
            skLineSegment(sketch, "E983", {"start": v(-1789.73, 470.24) * mm, "end": v(-1783.46, 470.1) * mm});
            skLineSegment(sketch, "E984", {"start": v(-1783.46, 470.1) * mm, "end": v(-1777.58, 469.9) * mm});
            skLineSegment(sketch, "E985", {"start": v(-1777.58, 469.9) * mm, "end": v(-1772.07, 469.61) * mm});
            skLineSegment(sketch, "E986", {"start": v(-1772.07, 469.61) * mm, "end": v(-1766.95, 469.28) * mm});
            skLineSegment(sketch, "E987", {"start": v(-1766.95, 469.28) * mm, "end": v(-1762.22, 468.9) * mm});
            skLineSegment(sketch, "E988", {"start": v(-1762.22, 468.9) * mm, "end": v(-1760.8, 471.8) * mm});
            skLineSegment(sketch, "E989", {"start": v(-1760.8, 471.8) * mm, "end": v(-1732.47, 567.06) * mm});
            skLineSegment(sketch, "E990", {"start": v(-1732.47, 567.06) * mm, "end": v(-1732.07, 570.26) * mm});
            skLineSegment(sketch, "E991", {"start": v(-1732.07, 570.26) * mm, "end": v(-1736.25, 572.54) * mm});
            skLineSegment(sketch, "E992", {"start": v(-1736.25, 572.54) * mm, "end": v(-1740.72, 575.05) * mm});
            skLineSegment(sketch, "E993", {"start": v(-1740.72, 575.05) * mm, "end": v(-1745.48, 577.82) * mm});
            skLineSegment(sketch, "E994", {"start": v(-1745.48, 577.82) * mm, "end": v(-1750.52, 580.86) * mm});
            skLineSegment(sketch, "E995", {"start": v(-1750.52, 580.86) * mm, "end": v(-1755.85, 584.17) * mm});
            skLineSegment(sketch, "E996", {"start": v(-1755.85, 584.17) * mm, "end": v(-1761.44, 587.77) * mm});
            skLineSegment(sketch, "E997", {"start": v(-1761.44, 587.77) * mm, "end": v(-1767.3, 591.65) * mm});
            skLineSegment(sketch, "E998", {"start": v(-1767.3, 591.65) * mm, "end": v(-1773.42, 595.84) * mm});
            skLineSegment(sketch, "E999", {"start": v(-1773.42, 595.84) * mm, "end": v(-1779.78, 600.33) * mm});
            skLineSegment(sketch, "E1000", {"start": v(-1779.78, 600.33) * mm, "end": v(-1786.4, 605.13) * mm});
            skLineSegment(sketch, "E1001", {"start": v(-1786.4, 605.13) * mm, "end": v(-1793.23, 610.27) * mm});
            skLineSegment(sketch, "E1002", {"start": v(-1793.23, 610.27) * mm, "end": v(-1800.3, 615.73) * mm});
            skLineSegment(sketch, "E1003", {"start": v(-1800.3, 615.73) * mm, "end": v(-1807.58, 621.53) * mm});
            skLineSegment(sketch, "E1004", {"start": v(-1807.58, 621.53) * mm, "end": v(-1815.07, 627.68) * mm});
            skLineSegment(sketch, "E1005", {"start": v(-1815.07, 627.68) * mm, "end": v(-1822.76, 634.18) * mm});
            skLineSegment(sketch, "E1006", {"start": v(-1822.76, 634.18) * mm, "end": v(-1830.64, 641.04) * mm});
            skLineSegment(sketch, "E1007", {"start": v(-1830.64, 641.04) * mm, "end": v(-1838.7, 648.27) * mm});
            skLineSegment(sketch, "E1008", {"start": v(-1838.7, 648.27) * mm, "end": v(-1846.94, 655.87) * mm});
            skLineSegment(sketch, "E1009", {"start": v(-1846.94, 655.87) * mm, "end": v(-1855.34, 663.86) * mm});
            skLineSegment(sketch, "E1010", {"start": v(-1855.34, 663.86) * mm, "end": v(-1863.9, 672.23) * mm});
            skLineSegment(sketch, "E1011", {"start": v(-1863.9, 672.23) * mm, "end": v(-1872.6, 681) * mm});
            skLineSegment(sketch, "E1012", {"start": v(-1872.6, 681) * mm, "end": v(-1881.43, 690.16) * mm});
            skLineSegment(sketch, "E1013", {"start": v(-1881.43, 690.16) * mm, "end": v(-1890.4, 699.73) * mm});
            skLineSegment(sketch, "E1014", {"start": v(-1890.4, 699.73) * mm, "end": v(-1899.47, 709.7) * mm});
            skLineSegment(sketch, "E1015", {"start": v(-1899.47, 709.7) * mm, "end": v(-1908.66, 720.1) * mm});
            skLineSegment(sketch, "E1016", {"start": v(-1908.66, 720.1) * mm, "end": v(-1917.93, 730.91) * mm});
            skLineSegment(sketch, "E1017", {"start": v(-1917.93, 730.91) * mm, "end": v(-1927.3, 742.16) * mm});
            skLineSegment(sketch, "E1018", {"start": v(-1927.3, 742.16) * mm, "end": v(-1936.74, 753.83) * mm});
            skLineSegment(sketch, "E1019", {"start": v(-1936.74, 753.83) * mm, "end": v(-1946.24, 765.94) * mm});
            skLineSegment(sketch, "E1020", {"start": v(-1946.24, 765.94) * mm, "end": v(-1955.8, 778.48) * mm});
            skLineSegment(sketch, "E1021", {"start": v(-1955.8, 778.48) * mm, "end": v(-1965.39, 791.47) * mm});
            skLineSegment(sketch, "E1022", {"start": v(-1965.39, 791.47) * mm, "end": v(-1975.02, 804.9) * mm});
            skLineSegment(sketch, "E1023", {"start": v(-1975.02, 804.9) * mm, "end": v(-1984.66, 818.8) * mm});
            skLineSegment(sketch, "E1024", {"start": v(-1984.66, 818.8) * mm, "end": v(-1994.32, 833.14) * mm});
            skLineSegment(sketch, "E1025", {"start": v(-1994.32, 833.14) * mm, "end": v(-2003.98, 847.93) * mm});
            skLineSegment(sketch, "E1026", {"start": v(-2003.98, 847.93) * mm, "end": v(-2007.46, 860.55) * mm});
            skLineSegment(sketch, "E1027", {"start": v(-2007.46, 860.55) * mm, "end": v(-1980.78, 920.3) * mm});
            skLineSegment(sketch, "E1028", {"start": v(-1980.78, 920.3) * mm, "end": v(-1969.07, 926.12) * mm});
            skLineSegment(sketch, "E1029", {"start": v(-1969.07, 926.12) * mm, "end": v(-1951.6, 928.81) * mm});
            skLineSegment(sketch, "E1030", {"start": v(-1951.6, 928.81) * mm, "end": v(-1934.48, 931.2) * mm});
            skLineSegment(sketch, "E1031", {"start": v(-1934.48, 931.2) * mm, "end": v(-1917.7, 933.28) * mm});
            skLineSegment(sketch, "E1032", {"start": v(-1917.7, 933.28) * mm, "end": v(-1901.26, 935.08) * mm});
            skLineSegment(sketch, "E1033", {"start": v(-1901.26, 935.08) * mm, "end": v(-1885.19, 936.6) * mm});
            skLineSegment(sketch, "E1034", {"start": v(-1885.19, 936.6) * mm, "end": v(-1869.47, 937.87) * mm});
            skLineSegment(sketch, "E1035", {"start": v(-1869.47, 937.87) * mm, "end": v(-1854.1, 938.87) * mm});
            skLineSegment(sketch, "E1036", {"start": v(-1854.1, 938.87) * mm, "end": v(-1839.12, 939.64) * mm});
            skLineSegment(sketch, "E1037", {"start": v(-1839.12, 939.64) * mm, "end": v(-1824.5, 940.17) * mm});
            skLineSegment(sketch, "E1038", {"start": v(-1824.5, 940.17) * mm, "end": v(-1810.25, 940.48) * mm});
            skLineSegment(sketch, "E1039", {"start": v(-1810.25, 940.48) * mm, "end": v(-1796.38, 940.58) * mm});
            skLineSegment(sketch, "E1040", {"start": v(-1796.38, 940.58) * mm, "end": v(-1782.9, 940.48) * mm});
            skLineSegment(sketch, "E1041", {"start": v(-1782.9, 940.48) * mm, "end": v(-1769.78, 940.2) * mm});
            skLineSegment(sketch, "E1042", {"start": v(-1769.78, 940.2) * mm, "end": v(-1757.06, 939.74) * mm});
            skLineSegment(sketch, "E1043", {"start": v(-1757.06, 939.74) * mm, "end": v(-1744.73, 939.1) * mm});
            skLineSegment(sketch, "E1044", {"start": v(-1744.73, 939.1) * mm, "end": v(-1732.78, 938.33) * mm});
            skLineSegment(sketch, "E1045", {"start": v(-1732.78, 938.33) * mm, "end": v(-1721.23, 937.4) * mm});
            skLineSegment(sketch, "E1046", {"start": v(-1721.23, 937.4) * mm, "end": v(-1710.07, 936.34) * mm});
            skLineSegment(sketch, "E1047", {"start": v(-1710.07, 936.34) * mm, "end": v(-1699.3, 935.16) * mm});
            skLineSegment(sketch, "E1048", {"start": v(-1699.3, 935.16) * mm, "end": v(-1688.93, 933.88) * mm});
            skLineSegment(sketch, "E1049", {"start": v(-1688.93, 933.88) * mm, "end": v(-1678.96, 932.5) * mm});
            skLineSegment(sketch, "E1050", {"start": v(-1678.96, 932.5) * mm, "end": v(-1669.38, 931.02) * mm});
            skLineSegment(sketch, "E1051", {"start": v(-1669.38, 931.02) * mm, "end": v(-1660.2, 929.47) * mm});
            skLineSegment(sketch, "E1052", {"start": v(-1660.2, 929.47) * mm, "end": v(-1651.42, 927.85) * mm});
            skLineSegment(sketch, "E1053", {"start": v(-1651.42, 927.85) * mm, "end": v(-1643.03, 926.18) * mm});
            skLineSegment(sketch, "E1054", {"start": v(-1643.03, 926.18) * mm, "end": v(-1635.04, 924.48) * mm});
            skLineSegment(sketch, "E1055", {"start": v(-1635.04, 924.48) * mm, "end": v(-1627.45, 922.73) * mm});
            skLineSegment(sketch, "E1056", {"start": v(-1627.45, 922.73) * mm, "end": v(-1620.25, 920.97) * mm});
            skLineSegment(sketch, "E1057", {"start": v(-1620.25, 920.97) * mm, "end": v(-1613.45, 919.2) * mm});
            skLineSegment(sketch, "E1058", {"start": v(-1613.45, 919.2) * mm, "end": v(-1607.04, 917.44) * mm});
            skLineSegment(sketch, "E1059", {"start": v(-1607.04, 917.44) * mm, "end": v(-1601.02, 915.68) * mm});
            skLineSegment(sketch, "E1060", {"start": v(-1601.02, 915.68) * mm, "end": v(-1595.39, 913.95) * mm});
            skLineSegment(sketch, "E1061", {"start": v(-1595.39, 913.95) * mm, "end": v(-1590.15, 912.26) * mm});
            skLineSegment(sketch, "E1062", {"start": v(-1590.15, 912.26) * mm, "end": v(-1585.29, 910.6) * mm});
            skLineSegment(sketch, "E1063", {"start": v(-1585.29, 910.6) * mm, "end": v(-1580.81, 909.02) * mm});
            skLineSegment(sketch, "E1064", {"start": v(-1580.81, 909.02) * mm, "end": v(-1578.69, 911.46) * mm});
            skLineSegment(sketch, "E1065", {"start": v(-1578.69, 911.46) * mm, "end": v(-1526.67, 996.13) * mm});
            skLineSegment(sketch, "E1066", {"start": v(-1526.67, 996.13) * mm, "end": v(-1525.46, 999.13) * mm});
            skLineSegment(sketch, "E1067", {"start": v(-1525.46, 999.13) * mm, "end": v(-1528.9, 1002.4) * mm});
            skLineSegment(sketch, "E1068", {"start": v(-1528.9, 1002.4) * mm, "end": v(-1532.57, 1005.99) * mm});
            skLineSegment(sketch, "E1069", {"start": v(-1532.57, 1005.99) * mm, "end": v(-1536.45, 1009.9) * mm});
            skLineSegment(sketch, "E1070", {"start": v(-1536.45, 1009.9) * mm, "end": v(-1540.54, 1014.14) * mm});
            skLineSegment(sketch, "E1071", {"start": v(-1540.54, 1014.14) * mm, "end": v(-1544.82, 1018.72) * mm});
            skLineSegment(sketch, "E1072", {"start": v(-1544.82, 1018.72) * mm, "end": v(-1549.3, 1023.63) * mm});
            skLineSegment(sketch, "E1073", {"start": v(-1549.3, 1023.63) * mm, "end": v(-1553.95, 1028.9) * mm});
            skLineSegment(sketch, "E1074", {"start": v(-1553.95, 1028.9) * mm, "end": v(-1558.78, 1034.53) * mm});
            skLineSegment(sketch, "E1075", {"start": v(-1558.78, 1034.53) * mm, "end": v(-1563.76, 1040.51) * mm});
            skLineSegment(sketch, "E1076", {"start": v(-1563.76, 1040.51) * mm, "end": v(-1568.9, 1046.87) * mm});
            skLineSegment(sketch, "E1077", {"start": v(-1568.9, 1046.87) * mm, "end": v(-1574.18, 1053.6) * mm});
            skLineSegment(sketch, "E1078", {"start": v(-1574.18, 1053.6) * mm, "end": v(-1579.59, 1060.7) * mm});
            skLineSegment(sketch, "E1079", {"start": v(-1579.59, 1060.7) * mm, "end": v(-1585.12, 1068.19) * mm});
            skLineSegment(sketch, "E1080", {"start": v(-1585.12, 1068.19) * mm, "end": v(-1590.76, 1076.06) * mm});
            skLineSegment(sketch, "E1081", {"start": v(-1590.76, 1076.06) * mm, "end": v(-1596.51, 1084.33) * mm});
            skLineSegment(sketch, "E1082", {"start": v(-1596.51, 1084.33) * mm, "end": v(-1602.35, 1093) * mm});
            skLineSegment(sketch, "E1083", {"start": v(-1602.35, 1093) * mm, "end": v(-1608.27, 1102.07) * mm});
            skLineSegment(sketch, "E1084", {"start": v(-1608.27, 1102.07) * mm, "end": v(-1614.25, 1111.55) * mm});
            skLineSegment(sketch, "E1085", {"start": v(-1614.25, 1111.55) * mm, "end": v(-1620.3, 1121.43) * mm});
            skLineSegment(sketch, "E1086", {"start": v(-1620.3, 1121.43) * mm, "end": v(-1626.4, 1131.73) * mm});
            skLineSegment(sketch, "E1087", {"start": v(-1626.4, 1131.73) * mm, "end": v(-1632.54, 1142.45) * mm});
            skLineSegment(sketch, "E1088", {"start": v(-1632.54, 1142.45) * mm, "end": v(-1638.7, 1153.6) * mm});
            skLineSegment(sketch, "E1089", {"start": v(-1638.7, 1153.6) * mm, "end": v(-1644.88, 1165.15) * mm});
            skLineSegment(sketch, "E1090", {"start": v(-1644.88, 1165.15) * mm, "end": v(-1651.07, 1177.14) * mm});
            skLineSegment(sketch, "E1091", {"start": v(-1651.07, 1177.14) * mm, "end": v(-1657.24, 1189.56) * mm});
            skLineSegment(sketch, "E1092", {"start": v(-1657.24, 1189.56) * mm, "end": v(-1663.4, 1202.4) * mm});
            skLineSegment(sketch, "E1093", {"start": v(-1663.4, 1202.4) * mm, "end": v(-1669.54, 1215.69) * mm});
            skLineSegment(sketch, "E1094", {"start": v(-1669.54, 1215.69) * mm, "end": v(-1675.64, 1229.4) * mm});
            skLineSegment(sketch, "E1095", {"start": v(-1675.64, 1229.4) * mm, "end": v(-1681.68, 1243.56) * mm});
            skLineSegment(sketch, "E1096", {"start": v(-1681.68, 1243.56) * mm, "end": v(-1687.66, 1258.15) * mm});
            skLineSegment(sketch, "E1097", {"start": v(-1687.66, 1258.15) * mm, "end": v(-1693.57, 1273.18) * mm});
            skLineSegment(sketch, "E1098", {"start": v(-1693.57, 1273.18) * mm, "end": v(-1699.4, 1288.65) * mm});
            skLineSegment(sketch, "E1099", {"start": v(-1699.4, 1288.65) * mm, "end": v(-1705.12, 1304.56) * mm});
            skLineSegment(sketch, "E1100", {"start": v(-1705.12, 1304.56) * mm, "end": v(-1710.74, 1320.92) * mm});
            skLineSegment(sketch, "E1101", {"start": v(-1710.74, 1320.92) * mm, "end": v(-1716.23, 1337.7) * mm});
            skLineSegment(sketch, "E1102", {"start": v(-1716.23, 1337.7) * mm, "end": v(-1716.33, 1350.8) * mm});
            skLineSegment(sketch, "E1103", {"start": v(-1716.33, 1350.8) * mm, "end": v(-1675.1, 1401.6) * mm});
            skLineSegment(sketch, "E1104", {"start": v(-1675.1, 1401.6) * mm, "end": v(-1662.27, 1404.2) * mm});
            skLineSegment(sketch, "E1105", {"start": v(-1662.27, 1404.2) * mm, "end": v(-1644.7, 1402.28) * mm});
            skLineSegment(sketch, "E1106", {"start": v(-1644.7, 1402.28) * mm, "end": v(-1627.55, 1400.14) * mm});
            skLineSegment(sketch, "E1107", {"start": v(-1627.55, 1400.14) * mm, "end": v(-1610.8, 1397.82) * mm});
            skLineSegment(sketch, "E1108", {"start": v(-1610.8, 1397.82) * mm, "end": v(-1594.46, 1395.3) * mm});
            skLineSegment(sketch, "E1109", {"start": v(-1594.46, 1395.3) * mm, "end": v(-1578.54, 1392.61) * mm});
            skLineSegment(sketch, "E1110", {"start": v(-1578.54, 1392.61) * mm, "end": v(-1563.03, 1389.76) * mm});
            skLineSegment(sketch, "E1111", {"start": v(-1563.03, 1389.76) * mm, "end": v(-1547.93, 1386.76) * mm});
            skLineSegment(sketch, "E1112", {"start": v(-1547.93, 1386.76) * mm, "end": v(-1533.25, 1383.62) * mm});
            skLineSegment(sketch, "E1113", {"start": v(-1533.25, 1383.62) * mm, "end": v(-1519, 1380.35) * mm});
            skLineSegment(sketch, "E1114", {"start": v(-1519, 1380.35) * mm, "end": v(-1505.15, 1376.96) * mm});
            skLineSegment(sketch, "E1115", {"start": v(-1505.15, 1376.96) * mm, "end": v(-1491.73, 1373.47) * mm});
            skLineSegment(sketch, "E1116", {"start": v(-1491.73, 1373.47) * mm, "end": v(-1478.72, 1369.89) * mm});
            skLineSegment(sketch, "E1117", {"start": v(-1478.72, 1369.89) * mm, "end": v(-1466.14, 1366.22) * mm});
            skLineSegment(sketch, "E1118", {"start": v(-1466.14, 1366.22) * mm, "end": v(-1453.97, 1362.48) * mm});
            skLineSegment(sketch, "E1119", {"start": v(-1453.97, 1362.48) * mm, "end": v(-1442.22, 1358.68) * mm});
            skLineSegment(sketch, "E1120", {"start": v(-1442.22, 1358.68) * mm, "end": v(-1430.88, 1354.83) * mm});
            skLineSegment(sketch, "E1121", {"start": v(-1430.88, 1354.83) * mm, "end": v(-1419.96, 1350.95) * mm});
            skLineSegment(sketch, "E1122", {"start": v(-1419.96, 1350.95) * mm, "end": v(-1409.46, 1347.04) * mm});
            skLineSegment(sketch, "E1123", {"start": v(-1409.46, 1347.04) * mm, "end": v(-1399.36, 1343.11) * mm});
            skLineSegment(sketch, "E1124", {"start": v(-1399.36, 1343.11) * mm, "end": v(-1389.68, 1339.18) * mm});
            skLineSegment(sketch, "E1125", {"start": v(-1389.68, 1339.18) * mm, "end": v(-1380.4, 1335.26) * mm});
            skLineSegment(sketch, "E1126", {"start": v(-1380.4, 1335.26) * mm, "end": v(-1371.53, 1331.36) * mm});
            skLineSegment(sketch, "E1127", {"start": v(-1371.53, 1331.36) * mm, "end": v(-1363.07, 1327.49) * mm});
            skLineSegment(sketch, "E1128", {"start": v(-1363.07, 1327.49) * mm, "end": v(-1355, 1323.66) * mm});
            skLineSegment(sketch, "E1129", {"start": v(-1355, 1323.66) * mm, "end": v(-1347.33, 1319.87) * mm});
            skLineSegment(sketch, "E1130", {"start": v(-1347.33, 1319.87) * mm, "end": v(-1340.06, 1316.16) * mm});
            skLineSegment(sketch, "E1131", {"start": v(-1340.06, 1316.16) * mm, "end": v(-1333.18, 1312.5) * mm});
            skLineSegment(sketch, "E1132", {"start": v(-1333.18, 1312.5) * mm, "end": v(-1326.68, 1308.94) * mm});
            skLineSegment(sketch, "E1133", {"start": v(-1326.68, 1308.94) * mm, "end": v(-1320.57, 1305.47) * mm});
            skLineSegment(sketch, "E1134", {"start": v(-1320.57, 1305.47) * mm, "end": v(-1314.83, 1302.1) * mm});
            skLineSegment(sketch, "E1135", {"start": v(-1314.83, 1302.1) * mm, "end": v(-1309.47, 1298.86) * mm});
            skLineSegment(sketch, "E1136", {"start": v(-1309.47, 1298.86) * mm, "end": v(-1304.48, 1295.73) * mm});
            skLineSegment(sketch, "E1137", {"start": v(-1304.48, 1295.73) * mm, "end": v(-1299.85, 1292.73) * mm});
            skLineSegment(sketch, "E1138", {"start": v(-1299.85, 1292.73) * mm, "end": v(-1295.59, 1289.88) * mm});
            skLineSegment(sketch, "E1139", {"start": v(-1295.59, 1289.88) * mm, "end": v(-1291.68, 1287.19) * mm});
            skLineSegment(sketch, "E1140", {"start": v(-1291.68, 1287.19) * mm, "end": v(-1289, 1289) * mm});
            skLineSegment(sketch, "E1141", {"start": v(-1289, 1289) * mm, "end": v(-1216.84, 1357.32) * mm});
            skLineSegment(sketch, "E1142", {"start": v(-1216.84, 1357.32) * mm, "end": v(-1214.89, 1359.9) * mm});
            skLineSegment(sketch, "E1143", {"start": v(-1214.89, 1359.9) * mm, "end": v(-1217.37, 1363.95) * mm});
            skLineSegment(sketch, "E1144", {"start": v(-1217.37, 1363.95) * mm, "end": v(-1219.98, 1368.37) * mm});
            skLineSegment(sketch, "E1145", {"start": v(-1219.98, 1368.37) * mm, "end": v(-1222.72, 1373.15) * mm});
            skLineSegment(sketch, "E1146", {"start": v(-1222.72, 1373.15) * mm, "end": v(-1225.57, 1378.3) * mm});
            skLineSegment(sketch, "E1147", {"start": v(-1225.57, 1378.3) * mm, "end": v(-1228.52, 1383.83) * mm});
            skLineSegment(sketch, "E1148", {"start": v(-1228.52, 1383.83) * mm, "end": v(-1231.57, 1389.74) * mm});
            skLineSegment(sketch, "E1149", {"start": v(-1231.57, 1389.74) * mm, "end": v(-1234.7, 1396.04) * mm});
            skLineSegment(sketch, "E1150", {"start": v(-1234.7, 1396.04) * mm, "end": v(-1237.9, 1402.72) * mm});
            skLineSegment(sketch, "E1151", {"start": v(-1237.9, 1402.72) * mm, "end": v(-1241.17, 1409.8) * mm});
            skLineSegment(sketch, "E1152", {"start": v(-1241.17, 1409.8) * mm, "end": v(-1244.5, 1417.26) * mm});
            skLineSegment(sketch, "E1153", {"start": v(-1244.5, 1417.26) * mm, "end": v(-1247.85, 1425.12) * mm});
            skLineSegment(sketch, "E1154", {"start": v(-1247.85, 1425.12) * mm, "end": v(-1251.24, 1433.38) * mm});
            skLineSegment(sketch, "E1155", {"start": v(-1251.24, 1433.38) * mm, "end": v(-1254.64, 1442.05) * mm});
            skLineSegment(sketch, "E1156", {"start": v(-1254.64, 1442.05) * mm, "end": v(-1258.06, 1451.12) * mm});
            skLineSegment(sketch, "E1157", {"start": v(-1258.06, 1451.12) * mm, "end": v(-1261.47, 1460.6) * mm});
            skLineSegment(sketch, "E1158", {"start": v(-1261.47, 1460.6) * mm, "end": v(-1264.86, 1470.48) * mm});
            skLineSegment(sketch, "E1159", {"start": v(-1264.86, 1470.48) * mm, "end": v(-1268.23, 1480.77) * mm});
            skLineSegment(sketch, "E1160", {"start": v(-1268.23, 1480.77) * mm, "end": v(-1271.56, 1491.47) * mm});
            skLineSegment(sketch, "E1161", {"start": v(-1271.56, 1491.47) * mm, "end": v(-1274.84, 1502.59) * mm});
            skLineSegment(sketch, "E1162", {"start": v(-1274.84, 1502.59) * mm, "end": v(-1278.07, 1514.11) * mm});
            skLineSegment(sketch, "E1163", {"start": v(-1278.07, 1514.11) * mm, "end": v(-1281.22, 1526.06) * mm});
            skLineSegment(sketch, "E1164", {"start": v(-1281.22, 1526.06) * mm, "end": v(-1284.3, 1538.41) * mm});
            skLineSegment(sketch, "E1165", {"start": v(-1284.3, 1538.41) * mm, "end": v(-1287.27, 1551.18) * mm});
            skLineSegment(sketch, "E1166", {"start": v(-1287.27, 1551.18) * mm, "end": v(-1290.14, 1564.36) * mm});
            skLineSegment(sketch, "E1167", {"start": v(-1290.14, 1564.36) * mm, "end": v(-1292.9, 1577.95) * mm});
            skLineSegment(sketch, "E1168", {"start": v(-1292.9, 1577.95) * mm, "end": v(-1295.52, 1591.96) * mm});
            skLineSegment(sketch, "E1169", {"start": v(-1295.52, 1591.96) * mm, "end": v(-1298.01, 1606.38) * mm});
            skLineSegment(sketch, "E1170", {"start": v(-1298.01, 1606.38) * mm, "end": v(-1300.35, 1621.2) * mm});
            skLineSegment(sketch, "E1171", {"start": v(-1300.35, 1621.2) * mm, "end": v(-1302.52, 1636.44) * mm});
            skLineSegment(sketch, "E1172", {"start": v(-1302.52, 1636.44) * mm, "end": v(-1304.52, 1652.08) * mm});
            skLineSegment(sketch, "E1173", {"start": v(-1304.52, 1652.08) * mm, "end": v(-1306.34, 1668.13) * mm});
            skLineSegment(sketch, "E1174", {"start": v(-1306.34, 1668.13) * mm, "end": v(-1307.96, 1684.58) * mm});
            skLineSegment(sketch, "E1175", {"start": v(-1307.96, 1684.58) * mm, "end": v(-1309.37, 1701.43) * mm});
            skLineSegment(sketch, "E1176", {"start": v(-1309.37, 1701.43) * mm, "end": v(-1310.57, 1718.68) * mm});
            skLineSegment(sketch, "E1177", {"start": v(-1310.57, 1718.68) * mm, "end": v(-1311.53, 1736.32) * mm});
            skLineSegment(sketch, "E1178", {"start": v(-1311.53, 1736.32) * mm, "end": v(-1308.24, 1748.99) * mm});
            skLineSegment(sketch, "E1179", {"start": v(-1308.24, 1748.99) * mm, "end": v(-1255.26, 1787.4) * mm});
            skLineSegment(sketch, "E1180", {"start": v(-1255.26, 1787.4) * mm, "end": v(-1242.2, 1786.58) * mm});
            skLineSegment(sketch, "E1181", {"start": v(-1242.2, 1786.58) * mm, "end": v(-1225.73, 1780.18) * mm});
            skLineSegment(sketch, "E1182", {"start": v(-1225.73, 1780.18) * mm, "end": v(-1209.7, 1773.68) * mm});
            skLineSegment(sketch, "E1183", {"start": v(-1209.7, 1773.68) * mm, "end": v(-1194.13, 1767.1) * mm});
            skLineSegment(sketch, "E1184", {"start": v(-1194.13, 1767.1) * mm, "end": v(-1179, 1760.44) * mm});
            skLineSegment(sketch, "E1185", {"start": v(-1179, 1760.44) * mm, "end": v(-1164.31, 1753.72) * mm});
            skLineSegment(sketch, "E1186", {"start": v(-1164.31, 1753.72) * mm, "end": v(-1150.07, 1746.95) * mm});
            skLineSegment(sketch, "E1187", {"start": v(-1150.07, 1746.95) * mm, "end": v(-1136.27, 1740.14) * mm});
            skLineSegment(sketch, "E1188", {"start": v(-1136.27, 1740.14) * mm, "end": v(-1122.9, 1733.3) * mm});
            skLineSegment(sketch, "E1189", {"start": v(-1122.9, 1733.3) * mm, "end": v(-1109.98, 1726.46) * mm});
            skLineSegment(sketch, "E1190", {"start": v(-1109.98, 1726.46) * mm, "end": v(-1097.48, 1719.6) * mm});
            skLineSegment(sketch, "E1191", {"start": v(-1097.48, 1719.6) * mm, "end": v(-1085.42, 1712.76) * mm});
            skLineSegment(sketch, "E1192", {"start": v(-1085.42, 1712.76) * mm, "end": v(-1073.79, 1705.93) * mm});
            skLineSegment(sketch, "E1193", {"start": v(-1073.79, 1705.93) * mm, "end": v(-1062.58, 1699.13) * mm});
            skLineSegment(sketch, "E1194", {"start": v(-1062.58, 1699.13) * mm, "end": v(-1051.8, 1692.37) * mm});
            skLineSegment(sketch, "E1195", {"start": v(-1051.8, 1692.37) * mm, "end": v(-1041.42, 1685.66) * mm});
            skLineSegment(sketch, "E1196", {"start": v(-1041.42, 1685.66) * mm, "end": v(-1031.47, 1679) * mm});
            skLineSegment(sketch, "E1197", {"start": v(-1031.47, 1679) * mm, "end": v(-1021.93, 1672.43) * mm});
            skLineSegment(sketch, "E1198", {"start": v(-1021.93, 1672.43) * mm, "end": v(-1012.8, 1665.93) * mm});
            skLineSegment(sketch, "E1199", {"start": v(-1012.8, 1665.93) * mm, "end": v(-1004.06, 1659.53) * mm});
            skLineSegment(sketch, "E1200", {"start": v(-1004.06, 1659.53) * mm, "end": v(-995.72, 1653.23) * mm});
            skLineSegment(sketch, "E1201", {"start": v(-995.72, 1653.23) * mm, "end": v(-987.78, 1647.04) * mm});
            skLineSegment(sketch, "E1202", {"start": v(-987.78, 1647.04) * mm, "end": v(-980.22, 1640.98) * mm});
            skLineSegment(sketch, "E1203", {"start": v(-980.22, 1640.98) * mm, "end": v(-973.04, 1635.04) * mm});
            skLineSegment(sketch, "E1204", {"start": v(-973.04, 1635.04) * mm, "end": v(-966.24, 1629.25) * mm});
            skLineSegment(sketch, "E1205", {"start": v(-966.24, 1629.25) * mm, "end": v(-959.82, 1623.62) * mm});
            skLineSegment(sketch, "E1206", {"start": v(-959.82, 1623.62) * mm, "end": v(-953.75, 1618.14) * mm});
            skLineSegment(sketch, "E1207", {"start": v(-953.75, 1618.14) * mm, "end": v(-948.05, 1612.84) * mm});
            skLineSegment(sketch, "E1208", {"start": v(-948.05, 1612.84) * mm, "end": v(-942.7, 1607.71) * mm});
            skLineSegment(sketch, "E1209", {"start": v(-942.7, 1607.71) * mm, "end": v(-937.69, 1602.78) * mm});
            skLineSegment(sketch, "E1210", {"start": v(-937.69, 1602.78) * mm, "end": v(-933.02, 1598.04) * mm});
            skLineSegment(sketch, "E1211", {"start": v(-933.02, 1598.04) * mm, "end": v(-928.68, 1593.51) * mm});
            skLineSegment(sketch, "E1212", {"start": v(-928.68, 1593.51) * mm, "end": v(-924.67, 1589.2) * mm});
            skLineSegment(sketch, "E1213", {"start": v(-924.67, 1589.2) * mm, "end": v(-920.98, 1585.11) * mm});
            skLineSegment(sketch, "E1214", {"start": v(-920.98, 1585.11) * mm, "end": v(-917.6, 1581.25) * mm});
            skLineSegment(sketch, "E1215", {"start": v(-917.6, 1581.25) * mm, "end": v(-914.51, 1577.64) * mm});
            skLineSegment(sketch, "E1216", {"start": v(-914.51, 1577.64) * mm, "end": v(-911.46, 1578.69) * mm});
            skLineSegment(sketch, "E1217", {"start": v(-911.46, 1578.69) * mm, "end": v(-824.07, 1626.01) * mm});
            skLineSegment(sketch, "E1218", {"start": v(-824.07, 1626.01) * mm, "end": v(-821.52, 1628) * mm});
            skLineSegment(sketch, "E1219", {"start": v(-821.52, 1628) * mm, "end": v(-822.87, 1632.56) * mm});
            skLineSegment(sketch, "E1220", {"start": v(-822.87, 1632.56) * mm, "end": v(-824.25, 1637.5) * mm});
            skLineSegment(sketch, "E1221", {"start": v(-824.25, 1637.5) * mm, "end": v(-825.66, 1642.82) * mm});
            skLineSegment(sketch, "E1222", {"start": v(-825.66, 1642.82) * mm, "end": v(-827.08, 1648.54) * mm});
            skLineSegment(sketch, "E1223", {"start": v(-827.08, 1648.54) * mm, "end": v(-828.5, 1654.65) * mm});
            skLineSegment(sketch, "E1224", {"start": v(-828.5, 1654.65) * mm, "end": v(-829.92, 1661.14) * mm});
            skLineSegment(sketch, "E1225", {"start": v(-829.92, 1661.14) * mm, "end": v(-831.31, 1668.03) * mm});
            skLineSegment(sketch, "E1226", {"start": v(-831.31, 1668.03) * mm, "end": v(-832.68, 1675.32) * mm});
            skLineSegment(sketch, "E1227", {"start": v(-832.68, 1675.32) * mm, "end": v(-834, 1683) * mm});
            skLineSegment(sketch, "E1228", {"start": v(-834, 1683) * mm, "end": v(-835.27, 1691.06) * mm});
            skLineSegment(sketch, "E1229", {"start": v(-835.27, 1691.06) * mm, "end": v(-836.48, 1699.53) * mm});
            skLineSegment(sketch, "E1230", {"start": v(-836.48, 1699.53) * mm, "end": v(-837.62, 1708.39) * mm});
            skLineSegment(sketch, "E1231", {"start": v(-837.62, 1708.39) * mm, "end": v(-838.66, 1717.64) * mm});
            skLineSegment(sketch, "E1232", {"start": v(-838.66, 1717.64) * mm, "end": v(-839.61, 1727.28) * mm});
            skLineSegment(sketch, "E1233", {"start": v(-839.61, 1727.28) * mm, "end": v(-840.45, 1737.32) * mm});
            skLineSegment(sketch, "E1234", {"start": v(-840.45, 1737.32) * mm, "end": v(-841.17, 1747.74) * mm});
            skLineSegment(sketch, "E1235", {"start": v(-841.17, 1747.74) * mm, "end": v(-841.76, 1758.55) * mm});
            skLineSegment(sketch, "E1236", {"start": v(-841.76, 1758.55) * mm, "end": v(-842.21, 1769.76) * mm});
            skLineSegment(sketch, "E1237", {"start": v(-842.21, 1769.76) * mm, "end": v(-842.5, 1781.34) * mm});
            skLineSegment(sketch, "E1238", {"start": v(-842.5, 1781.34) * mm, "end": v(-842.64, 1793.31) * mm});
            skLineSegment(sketch, "E1239", {"start": v(-842.64, 1793.31) * mm, "end": v(-842.6, 1805.66) * mm});
            skLineSegment(sketch, "E1240", {"start": v(-842.6, 1805.66) * mm, "end": v(-842.36, 1818.39) * mm});
            skLineSegment(sketch, "E1241", {"start": v(-842.36, 1818.39) * mm, "end": v(-841.93, 1831.5) * mm});
            skLineSegment(sketch, "E1242", {"start": v(-841.93, 1831.5) * mm, "end": v(-841.3, 1844.97) * mm});
            skLineSegment(sketch, "E1243", {"start": v(-841.3, 1844.97) * mm, "end": v(-840.44, 1858.81) * mm});
            skLineSegment(sketch, "E1244", {"start": v(-840.44, 1858.81) * mm, "end": v(-839.35, 1873.02) * mm});
            skLineSegment(sketch, "E1245", {"start": v(-839.35, 1873.02) * mm, "end": v(-838.02, 1887.59) * mm});
            skLineSegment(sketch, "E1246", {"start": v(-838.02, 1887.59) * mm, "end": v(-836.44, 1902.52) * mm});
            skLineSegment(sketch, "E1247", {"start": v(-836.44, 1902.52) * mm, "end": v(-834.6, 1917.8) * mm});
            skLineSegment(sketch, "E1248", {"start": v(-834.6, 1917.8) * mm, "end": v(-832.48, 1933.42) * mm});
            skLineSegment(sketch, "E1249", {"start": v(-832.48, 1933.42) * mm, "end": v(-830.08, 1949.4) * mm});
            skLineSegment(sketch, "E1250", {"start": v(-830.08, 1949.4) * mm, "end": v(-827.4, 1965.7) * mm});
            skLineSegment(sketch, "E1251", {"start": v(-827.4, 1965.7) * mm, "end": v(-824.4, 1982.35) * mm});
            skLineSegment(sketch, "E1252", {"start": v(-824.4, 1982.35) * mm, "end": v(-821.08, 1999.32) * mm});
            skLineSegment(sketch, "E1253", {"start": v(-821.08, 1999.32) * mm, "end": v(-817.45, 2016.6) * mm});
            skLineSegment(sketch, "E1254", {"start": v(-817.45, 2016.6) * mm, "end": v(-810.99, 2028) * mm});
            skLineSegment(sketch, "E1255", {"start": v(-810.99, 2028) * mm, "end": v(-749.88, 2051.37) * mm});
            skLineSegment(sketch, "E1256", {"start": v(-749.88, 2051.37) * mm, "end": v(-737.47, 2047.2) * mm});
            skLineSegment(sketch, "E1257", {"start": v(-737.47, 2047.2) * mm, "end": v(-723.22, 2036.76) * mm});
            skLineSegment(sketch, "E1258", {"start": v(-723.22, 2036.76) * mm, "end": v(-709.43, 2026.34) * mm});
            skLineSegment(sketch, "E1259", {"start": v(-709.43, 2026.34) * mm, "end": v(-696.09, 2015.94) * mm});
            skLineSegment(sketch, "E1260", {"start": v(-696.09, 2015.94) * mm, "end": v(-683.2, 2005.6) * mm});
            skLineSegment(sketch, "E1261", {"start": v(-683.2, 2005.6) * mm, "end": v(-670.75, 1995.3) * mm});
            skLineSegment(sketch, "E1262", {"start": v(-670.75, 1995.3) * mm, "end": v(-658.74, 1985.08) * mm});
            skLineSegment(sketch, "E1263", {"start": v(-658.74, 1985.08) * mm, "end": v(-647.17, 1974.94) * mm});
            skLineSegment(sketch, "E1264", {"start": v(-647.17, 1974.94) * mm, "end": v(-636.03, 1964.88) * mm});
            skLineSegment(sketch, "E1265", {"start": v(-636.03, 1964.88) * mm, "end": v(-625.31, 1954.91) * mm});
            skLineSegment(sketch, "E1266", {"start": v(-625.31, 1954.91) * mm, "end": v(-615.02, 1945.06) * mm});
            skLineSegment(sketch, "E1267", {"start": v(-615.02, 1945.06) * mm, "end": v(-605.14, 1935.33) * mm});
            skLineSegment(sketch, "E1268", {"start": v(-605.14, 1935.33) * mm, "end": v(-595.67, 1925.72) * mm});
            skLineSegment(sketch, "E1269", {"start": v(-595.67, 1925.72) * mm, "end": v(-586.6, 1916.25) * mm});
            skLineSegment(sketch, "E1270", {"start": v(-586.6, 1916.25) * mm, "end": v(-577.94, 1906.92) * mm});
            skLineSegment(sketch, "E1271", {"start": v(-577.94, 1906.92) * mm, "end": v(-569.66, 1897.76) * mm});
            skLineSegment(sketch, "E1272", {"start": v(-569.66, 1897.76) * mm, "end": v(-561.77, 1888.76) * mm});
            skLineSegment(sketch, "E1273", {"start": v(-561.77, 1888.76) * mm, "end": v(-554.25, 1879.94) * mm});
            skLineSegment(sketch, "E1274", {"start": v(-554.25, 1879.94) * mm, "end": v(-547.1, 1871.3) * mm});
            skLineSegment(sketch, "E1275", {"start": v(-547.1, 1871.3) * mm, "end": v(-540.33, 1862.85) * mm});
            skLineSegment(sketch, "E1276", {"start": v(-540.33, 1862.85) * mm, "end": v(-533.9, 1854.6) * mm});
            skLineSegment(sketch, "E1277", {"start": v(-533.9, 1854.6) * mm, "end": v(-527.83, 1846.57) * mm});
            skLineSegment(sketch, "E1278", {"start": v(-527.83, 1846.57) * mm, "end": v(-522.1, 1838.76) * mm});
            skLineSegment(sketch, "E1279", {"start": v(-522.1, 1838.76) * mm, "end": v(-516.7, 1831.17) * mm});
            skLineSegment(sketch, "E1280", {"start": v(-516.7, 1831.17) * mm, "end": v(-511.64, 1823.82) * mm});
            skLineSegment(sketch, "E1281", {"start": v(-511.64, 1823.82) * mm, "end": v(-506.89, 1816.71) * mm});
            skLineSegment(sketch, "E1282", {"start": v(-506.89, 1816.71) * mm, "end": v(-502.45, 1809.85) * mm});
            skLineSegment(sketch, "E1283", {"start": v(-502.45, 1809.85) * mm, "end": v(-498.31, 1803.25) * mm});
            skLineSegment(sketch, "E1284", {"start": v(-498.31, 1803.25) * mm, "end": v(-494.47, 1796.92) * mm});
            skLineSegment(sketch, "E1285", {"start": v(-494.47, 1796.92) * mm, "end": v(-490.9, 1790.86) * mm});
            skLineSegment(sketch, "E1286", {"start": v(-490.9, 1790.86) * mm, "end": v(-487.62, 1785.07) * mm});
            skLineSegment(sketch, "E1287", {"start": v(-487.62, 1785.07) * mm, "end": v(-484.6, 1779.58) * mm});
            skLineSegment(sketch, "E1288", {"start": v(-484.6, 1779.58) * mm, "end": v(-481.85, 1774.37) * mm});
            skLineSegment(sketch, "E1289", {"start": v(-481.85, 1774.37) * mm, "end": v(-479.34, 1769.47) * mm});
            skLineSegment(sketch, "E1290", {"start": v(-479.34, 1769.47) * mm, "end": v(-477.07, 1764.87) * mm});
            skLineSegment(sketch, "E1291", {"start": v(-477.07, 1764.87) * mm, "end": v(-475.03, 1760.58) * mm});
            skLineSegment(sketch, "E1292", {"start": v(-475.03, 1760.58) * mm, "end": v(-471.8, 1760.8) * mm});
            skLineSegment(sketch, "E1293", {"start": v(-471.8, 1760.8) * mm, "end": v(-375.15, 1783.9) * mm});
            skLineSegment(sketch, "E1294", {"start": v(-375.15, 1783.9) * mm, "end": v(-372.17, 1785.15) * mm});
            skLineSegment(sketch, "E1295", {"start": v(-372.17, 1785.15) * mm, "end": v(-372.3, 1789.9) * mm});
            skLineSegment(sketch, "E1296", {"start": v(-372.3, 1789.9) * mm, "end": v(-372.35, 1795.03) * mm});
            skLineSegment(sketch, "E1297", {"start": v(-372.35, 1795.03) * mm, "end": v(-372.33, 1800.54) * mm});
            skLineSegment(sketch, "E1298", {"start": v(-372.33, 1800.54) * mm, "end": v(-372.22, 1806.43) * mm});
            skLineSegment(sketch, "E1299", {"start": v(-372.22, 1806.43) * mm, "end": v(-372.02, 1812.7) * mm});
            skLineSegment(sketch, "E1300", {"start": v(-372.02, 1812.7) * mm, "end": v(-371.7, 1819.34) * mm});
            skLineSegment(sketch, "E1301", {"start": v(-371.7, 1819.34) * mm, "end": v(-371.27, 1826.36) * mm});
            skLineSegment(sketch, "E1302", {"start": v(-371.27, 1826.36) * mm, "end": v(-370.7, 1833.74) * mm});
            skLineSegment(sketch, "E1303", {"start": v(-370.7, 1833.74) * mm, "end": v(-370, 1841.5) * mm});
            skLineSegment(sketch, "E1304", {"start": v(-370, 1841.5) * mm, "end": v(-369.13, 1849.63) * mm});
            skLineSegment(sketch, "E1305", {"start": v(-369.13, 1849.63) * mm, "end": v(-368.1, 1858.12) * mm});
            skLineSegment(sketch, "E1306", {"start": v(-368.1, 1858.12) * mm, "end": v(-366.91, 1866.96) * mm});
            skLineSegment(sketch, "E1307", {"start": v(-366.91, 1866.96) * mm, "end": v(-365.53, 1876.17) * mm});
            skLineSegment(sketch, "E1308", {"start": v(-365.53, 1876.17) * mm, "end": v(-363.95, 1885.73) * mm});
            skLineSegment(sketch, "E1309", {"start": v(-363.95, 1885.73) * mm, "end": v(-362.16, 1895.64) * mm});
            skLineSegment(sketch, "E1310", {"start": v(-362.16, 1895.64) * mm, "end": v(-360.16, 1905.9) * mm});
            skLineSegment(sketch, "E1311", {"start": v(-360.16, 1905.9) * mm, "end": v(-357.93, 1916.5) * mm});
            skLineSegment(sketch, "E1312", {"start": v(-357.93, 1916.5) * mm, "end": v(-355.47, 1927.43) * mm});
            skLineSegment(sketch, "E1313", {"start": v(-355.47, 1927.43) * mm, "end": v(-352.75, 1938.7) * mm});
            skLineSegment(sketch, "E1314", {"start": v(-352.75, 1938.7) * mm, "end": v(-349.78, 1950.3) * mm});
            skLineSegment(sketch, "E1315", {"start": v(-349.78, 1950.3) * mm, "end": v(-346.54, 1962.21) * mm});
            skLineSegment(sketch, "E1316", {"start": v(-346.54, 1962.21) * mm, "end": v(-343.02, 1974.45) * mm});
            skLineSegment(sketch, "E1317", {"start": v(-343.02, 1974.45) * mm, "end": v(-339.22, 1987) * mm});
            skLineSegment(sketch, "E1318", {"start": v(-339.22, 1987) * mm, "end": v(-335.11, 1999.84) * mm});
            skLineSegment(sketch, "E1319", {"start": v(-335.11, 1999.84) * mm, "end": v(-330.7, 2013) * mm});
            skLineSegment(sketch, "E1320", {"start": v(-330.7, 2013) * mm, "end": v(-325.98, 2026.44) * mm});
            skLineSegment(sketch, "E1321", {"start": v(-325.98, 2026.44) * mm, "end": v(-320.92, 2040.17) * mm});
            skLineSegment(sketch, "E1322", {"start": v(-320.92, 2040.17) * mm, "end": v(-315.53, 2054.18) * mm});
            skLineSegment(sketch, "E1323", {"start": v(-315.53, 2054.18) * mm, "end": v(-309.8, 2068.46) * mm});
            skLineSegment(sketch, "E1324", {"start": v(-309.8, 2068.46) * mm, "end": v(-303.71, 2083) * mm});
            skLineSegment(sketch, "E1325", {"start": v(-303.71, 2083) * mm, "end": v(-297.26, 2097.81) * mm});
            skLineSegment(sketch, "E1326", {"start": v(-297.26, 2097.81) * mm, "end": v(-290.44, 2112.87) * mm});
            skLineSegment(sketch, "E1327", {"start": v(-290.44, 2112.87) * mm, "end": v(-283.24, 2128.17) * mm});
            skLineSegment(sketch, "E1328", {"start": v(-283.24, 2128.17) * mm, "end": v(-275.64, 2143.7) * mm});
            skLineSegment(sketch, "E1329", {"start": v(-275.64, 2143.7) * mm, "end": v(-267.66, 2159.46) * mm});
            skLineSegment(sketch, "E1330", {"start": v(-267.66, 2159.46) * mm, "end": v(-258.47, 2168.79) * mm});
            skLineSegment(sketch, "E1331", {"start": v(-258.47, 2168.79) * mm, "end": v(-193.4, 2175.56) * mm});
            skLineSegment(sketch, "E1332", {"start": v(-193.4, 2175.56) * mm, "end": v(-182.48, 2168.32) * mm});
            skLineSegment(sketch, "E1333", {"start": v(-182.48, 2168.32) * mm, "end": v(-171.42, 2154.54) * mm});
            skLineSegment(sketch, "E1334", {"start": v(-171.42, 2154.54) * mm, "end": v(-160.8, 2140.9) * mm});
            skLineSegment(sketch, "E1335", {"start": v(-160.8, 2140.9) * mm, "end": v(-150.6, 2127.41) * mm});
            skLineSegment(sketch, "E1336", {"start": v(-150.6, 2127.41) * mm, "end": v(-140.83, 2114.08) * mm});
            skLineSegment(sketch, "E1337", {"start": v(-140.83, 2114.08) * mm, "end": v(-131.47, 2100.92) * mm});
            skLineSegment(sketch, "E1338", {"start": v(-131.47, 2100.92) * mm, "end": v(-122.52, 2087.94) * mm});
            skLineSegment(sketch, "E1339", {"start": v(-122.52, 2087.94) * mm, "end": v(-113.97, 2075.14) * mm});
            skLineSegment(sketch, "E1340", {"start": v(-113.97, 2075.14) * mm, "end": v(-105.8, 2062.54) * mm});
            skLineSegment(sketch, "E1341", {"start": v(-105.8, 2062.54) * mm, "end": v(-98.04, 2050.15) * mm});
            skLineSegment(sketch, "E1342", {"start": v(-98.04, 2050.15) * mm, "end": v(-90.64, 2037.96) * mm});
            skLineSegment(sketch, "E1343", {"start": v(-90.64, 2037.96) * mm, "end": v(-83.62, 2026) * mm});
            skLineSegment(sketch, "E1344", {"start": v(-83.62, 2026) * mm, "end": v(-76.96, 2014.27) * mm});
            skLineSegment(sketch, "E1345", {"start": v(-76.96, 2014.27) * mm, "end": v(-70.66, 2002.78) * mm});
            skLineSegment(sketch, "E1346", {"start": v(-70.66, 2002.78) * mm, "end": v(-64.7, 1991.53) * mm});
            skLineSegment(sketch, "E1347", {"start": v(-64.7, 1991.53) * mm, "end": v(-59.07, 1980.53) * mm});
            skLineSegment(sketch, "E1348", {"start": v(-59.07, 1980.53) * mm, "end": v(-53.78, 1969.8) * mm});
            skLineSegment(sketch, "E1349", {"start": v(-53.78, 1969.8) * mm, "end": v(-48.8, 1959.33) * mm});
            skLineSegment(sketch, "E1350", {"start": v(-48.8, 1959.33) * mm, "end": v(-44.14, 1949.14) * mm});
            skLineSegment(sketch, "E1351", {"start": v(-44.14, 1949.14) * mm, "end": v(-39.78, 1939.22) * mm});
            skLineSegment(sketch, "E1352", {"start": v(-39.78, 1939.22) * mm, "end": v(-35.7, 1929.6) * mm});
            skLineSegment(sketch, "E1353", {"start": v(-35.7, 1929.6) * mm, "end": v(-31.92, 1920.27) * mm});
            skLineSegment(sketch, "E1354", {"start": v(-31.92, 1920.27) * mm, "end": v(-28.4, 1911.24) * mm});
            skLineSegment(sketch, "E1355", {"start": v(-28.4, 1911.24) * mm, "end": v(-25.16, 1902.51) * mm});
            skLineSegment(sketch, "E1356", {"start": v(-25.16, 1902.51) * mm, "end": v(-22.17, 1894.1) * mm});
            skLineSegment(sketch, "E1357", {"start": v(-22.17, 1894.1) * mm, "end": v(-19.42, 1886) * mm});
            skLineSegment(sketch, "E1358", {"start": v(-19.42, 1886) * mm, "end": v(-16.9, 1878.23) * mm});
            skLineSegment(sketch, "E1359", {"start": v(-16.9, 1878.23) * mm, "end": v(-14.61, 1870.78) * mm});
            skLineSegment(sketch, "E1360", {"start": v(-14.61, 1870.78) * mm, "end": v(-12.54, 1863.67) * mm});
            skLineSegment(sketch, "E1361", {"start": v(-12.54, 1863.67) * mm, "end": v(-10.67, 1856.9) * mm});
            skLineSegment(sketch, "E1362", {"start": v(-10.67, 1856.9) * mm, "end": v(-9, 1850.46) * mm});
            skLineSegment(sketch, "E1363", {"start": v(-9, 1850.46) * mm, "end": v(-7.5, 1844.36) * mm});
            skLineSegment(sketch, "E1364", {"start": v(-7.5, 1844.36) * mm, "end": v(-6.19, 1838.62) * mm});
            skLineSegment(sketch, "E1365", {"start": v(-6.19, 1838.62) * mm, "end": v(-5.03, 1833.24) * mm});
            skLineSegment(sketch, "E1366", {"start": v(-5.03, 1833.24) * mm, "end": v(-4.03, 1828.2) * mm});
            skLineSegment(sketch, "E1367", {"start": v(-4.03, 1828.2) * mm, "end": v(-3.17, 1823.53) * mm});
            skLineSegment(sketch, "E1368", {"start": v(-3.17, 1823.53) * mm, "end": v(0, 1822.91) * mm});
            skLineSegment(sketch, "E1369", {"start": v(0, 1822.91) * mm, "end": v(99.34, 1820.2) * mm});
            skLineSegment(sketch, "E1370", {"start": v(99.34, 1820.2) * mm, "end": v(102.54, 1820.65) * mm});
            skLineSegment(sketch, "E1371", {"start": v(102.54, 1820.65) * mm, "end": v(103.65, 1825.27) * mm});
            skLineSegment(sketch, "E1372", {"start": v(103.65, 1825.27) * mm, "end": v(104.93, 1830.24) * mm});
            skLineSegment(sketch, "E1373", {"start": v(104.93, 1830.24) * mm, "end": v(106.37, 1835.55) * mm});
            skLineSegment(sketch, "E1374", {"start": v(106.37, 1835.55) * mm, "end": v(108, 1841.22) * mm});
            skLineSegment(sketch, "E1375", {"start": v(108, 1841.22) * mm, "end": v(109.82, 1847.22) * mm});
            skLineSegment(sketch, "E1376", {"start": v(109.82, 1847.22) * mm, "end": v(111.84, 1853.55) * mm});
            skLineSegment(sketch, "E1377", {"start": v(111.84, 1853.55) * mm, "end": v(114.08, 1860.22) * mm});
            skLineSegment(sketch, "E1378", {"start": v(114.08, 1860.22) * mm, "end": v(116.54, 1867.2) * mm});
            skLineSegment(sketch, "E1379", {"start": v(116.54, 1867.2) * mm, "end": v(119.23, 1874.52) * mm});
            skLineSegment(sketch, "E1380", {"start": v(119.23, 1874.52) * mm, "end": v(122.16, 1882.14) * mm});
            skLineSegment(sketch, "E1381", {"start": v(122.16, 1882.14) * mm, "end": v(125.35, 1890.08) * mm});
            skLineSegment(sketch, "E1382", {"start": v(125.35, 1890.08) * mm, "end": v(128.8, 1898.31) * mm});
            skLineSegment(sketch, "E1383", {"start": v(128.8, 1898.31) * mm, "end": v(132.52, 1906.85) * mm});
            skLineSegment(sketch, "E1384", {"start": v(132.52, 1906.85) * mm, "end": v(136.52, 1915.67) * mm});
            skLineSegment(sketch, "E1385", {"start": v(136.52, 1915.67) * mm, "end": v(140.8, 1924.79) * mm});
            skLineSegment(sketch, "E1386", {"start": v(140.8, 1924.79) * mm, "end": v(145.4, 1934.17) * mm});
            skLineSegment(sketch, "E1387", {"start": v(145.4, 1934.17) * mm, "end": v(150.29, 1943.83) * mm});
            skLineSegment(sketch, "E1388", {"start": v(150.29, 1943.83) * mm, "end": v(155.5, 1953.76) * mm});
            skLineSegment(sketch, "E1389", {"start": v(155.5, 1953.76) * mm, "end": v(161.04, 1963.94) * mm});
            skLineSegment(sketch, "E1390", {"start": v(161.04, 1963.94) * mm, "end": v(166.91, 1974.37) * mm});
            skLineSegment(sketch, "E1391", {"start": v(166.91, 1974.37) * mm, "end": v(173.12, 1985.04) * mm});
            skLineSegment(sketch, "E1392", {"start": v(173.12, 1985.04) * mm, "end": v(179.69, 1995.95) * mm});
            skLineSegment(sketch, "E1393", {"start": v(179.69, 1995.95) * mm, "end": v(186.61, 2007.08) * mm});
            skLineSegment(sketch, "E1394", {"start": v(186.61, 2007.08) * mm, "end": v(193.9, 2018.44) * mm});
            skLineSegment(sketch, "E1395", {"start": v(193.9, 2018.44) * mm, "end": v(201.57, 2030) * mm});
            skLineSegment(sketch, "E1396", {"start": v(201.57, 2030) * mm, "end": v(209.61, 2041.76) * mm});
            skLineSegment(sketch, "E1397", {"start": v(209.61, 2041.76) * mm, "end": v(218.05, 2053.71) * mm});
            skLineSegment(sketch, "E1398", {"start": v(218.05, 2053.71) * mm, "end": v(226.88, 2065.85) * mm});
            skLineSegment(sketch, "E1399", {"start": v(226.88, 2065.85) * mm, "end": v(236.11, 2078.16) * mm});
            skLineSegment(sketch, "E1400", {"start": v(236.11, 2078.16) * mm, "end": v(245.76, 2090.63) * mm});
            skLineSegment(sketch, "E1401", {"start": v(245.76, 2090.63) * mm, "end": v(255.82, 2103.27) * mm});
            skLineSegment(sketch, "E1402", {"start": v(255.82, 2103.27) * mm, "end": v(266.3, 2116.04) * mm});
            skLineSegment(sketch, "E1403", {"start": v(266.3, 2116.04) * mm, "end": v(277.23, 2128.96) * mm});
            skLineSegment(sketch, "E1404", {"start": v(277.23, 2128.96) * mm, "end": v(288.58, 2142) * mm});
            skLineSegment(sketch, "E1405", {"start": v(288.58, 2142) * mm, "end": v(300.37, 2155.16) * mm});
            skLineSegment(sketch, "E1406", {"start": v(300.37, 2155.16) * mm, "end": v(311.66, 2161.79) * mm});
            skLineSegment(sketch, "E1407", {"start": v(311.66, 2161.79) * mm, "end": v(376.27, 2151.48) * mm});
            skLineSegment(sketch, "E1408", {"start": v(376.27, 2151.48) * mm, "end": v(384.94, 2141.67) * mm});
            skLineSegment(sketch, "E1409", {"start": v(384.94, 2141.67) * mm, "end": v(392.05, 2125.5) * mm});
            skLineSegment(sketch, "E1410", {"start": v(392.05, 2125.5) * mm, "end": v(398.79, 2109.57) * mm});
            skLineSegment(sketch, "E1411", {"start": v(398.79, 2109.57) * mm, "end": v(405.14, 2093.9) * mm});
            skLineSegment(sketch, "E1412", {"start": v(405.14, 2093.9) * mm, "end": v(411.14, 2078.5) * mm});
            skLineSegment(sketch, "E1413", {"start": v(411.14, 2078.5) * mm, "end": v(416.77, 2063.36) * mm});
            skLineSegment(sketch, "E1414", {"start": v(416.77, 2063.36) * mm, "end": v(422.06, 2048.5) * mm});
            skLineSegment(sketch, "E1415", {"start": v(422.06, 2048.5) * mm, "end": v(427, 2033.93) * mm});
            skLineSegment(sketch, "E1416", {"start": v(427, 2033.93) * mm, "end": v(431.62, 2019.65) * mm});
            skLineSegment(sketch, "E1417", {"start": v(431.62, 2019.65) * mm, "end": v(435.92, 2005.66) * mm});
            skLineSegment(sketch, "E1418", {"start": v(435.92, 2005.66) * mm, "end": v(439.9, 1991.98) * mm});
            skLineSegment(sketch, "E1419", {"start": v(439.9, 1991.98) * mm, "end": v(443.6, 1978.61) * mm});
            skLineSegment(sketch, "E1420", {"start": v(443.6, 1978.61) * mm, "end": v(447, 1965.56) * mm});
            skLineSegment(sketch, "E1421", {"start": v(447, 1965.56) * mm, "end": v(450.1, 1952.82) * mm});
            skLineSegment(sketch, "E1422", {"start": v(450.1, 1952.82) * mm, "end": v(452.96, 1940.41) * mm});
            skLineSegment(sketch, "E1423", {"start": v(452.96, 1940.41) * mm, "end": v(455.54, 1928.34) * mm});
            skLineSegment(sketch, "E1424", {"start": v(455.54, 1928.34) * mm, "end": v(457.88, 1916.6) * mm});
            skLineSegment(sketch, "E1425", {"start": v(457.88, 1916.6) * mm, "end": v(459.97, 1905.2) * mm});
            skLineSegment(sketch, "E1426", {"start": v(459.97, 1905.2) * mm, "end": v(461.84, 1894.14) * mm});
            skLineSegment(sketch, "E1427", {"start": v(461.84, 1894.14) * mm, "end": v(463.49, 1883.44) * mm});
            skLineSegment(sketch, "E1428", {"start": v(463.49, 1883.44) * mm, "end": v(464.93, 1873.1) * mm});
            skLineSegment(sketch, "E1429", {"start": v(464.93, 1873.1) * mm, "end": v(466.17, 1863.1) * mm});
            skLineSegment(sketch, "E1430", {"start": v(466.17, 1863.1) * mm, "end": v(467.22, 1853.46) * mm});
            skLineSegment(sketch, "E1431", {"start": v(467.22, 1853.46) * mm, "end": v(468.1, 1844.2) * mm});
            skLineSegment(sketch, "E1432", {"start": v(468.1, 1844.2) * mm, "end": v(468.82, 1835.3) * mm});
            skLineSegment(sketch, "E1433", {"start": v(468.82, 1835.3) * mm, "end": v(469.38, 1826.76) * mm});
            skLineSegment(sketch, "E1434", {"start": v(469.38, 1826.76) * mm, "end": v(469.8, 1818.6) * mm});
            skLineSegment(sketch, "E1435", {"start": v(469.8, 1818.6) * mm, "end": v(470.08, 1810.82) * mm});
            skLineSegment(sketch, "E1436", {"start": v(470.08, 1810.82) * mm, "end": v(470.24, 1803.41) * mm});
            skLineSegment(sketch, "E1437", {"start": v(470.24, 1803.41) * mm, "end": v(470.3, 1796.38) * mm});
            skLineSegment(sketch, "E1438", {"start": v(470.3, 1796.38) * mm, "end": v(470.24, 1789.73) * mm});
            skLineSegment(sketch, "E1439", {"start": v(470.24, 1789.73) * mm, "end": v(470.1, 1783.46) * mm});
            skLineSegment(sketch, "E1440", {"start": v(470.1, 1783.46) * mm, "end": v(469.9, 1777.58) * mm});
            skLineSegment(sketch, "E1441", {"start": v(469.9, 1777.58) * mm, "end": v(469.61, 1772.07) * mm});
            skLineSegment(sketch, "E1442", {"start": v(469.61, 1772.07) * mm, "end": v(469.28, 1766.95) * mm});
            skLineSegment(sketch, "E1443", {"start": v(469.28, 1766.95) * mm, "end": v(468.9, 1762.22) * mm});
            skLineSegment(sketch, "E1444", {"start": v(468.9, 1762.22) * mm, "end": v(471.8, 1760.8) * mm});
            skLineSegment(sketch, "E1445", {"start": v(471.8, 1760.8) * mm, "end": v(567.06, 1732.47) * mm});
            skLineSegment(sketch, "E1446", {"start": v(567.06, 1732.47) * mm, "end": v(570.26, 1732.07) * mm});
            skLineSegment(sketch, "E1447", {"start": v(570.26, 1732.07) * mm, "end": v(572.54, 1736.25) * mm});
            skLineSegment(sketch, "E1448", {"start": v(572.54, 1736.25) * mm, "end": v(575.05, 1740.72) * mm});
            skLineSegment(sketch, "E1449", {"start": v(575.05, 1740.72) * mm, "end": v(577.82, 1745.48) * mm});
            skLineSegment(sketch, "E1450", {"start": v(577.82, 1745.48) * mm, "end": v(580.86, 1750.52) * mm});
            skLineSegment(sketch, "E1451", {"start": v(580.86, 1750.52) * mm, "end": v(584.17, 1755.85) * mm});
            skLineSegment(sketch, "E1452", {"start": v(584.17, 1755.85) * mm, "end": v(587.77, 1761.44) * mm});
            skLineSegment(sketch, "E1453", {"start": v(587.77, 1761.44) * mm, "end": v(591.65, 1767.3) * mm});
            skLineSegment(sketch, "E1454", {"start": v(591.65, 1767.3) * mm, "end": v(595.84, 1773.42) * mm});
            skLineSegment(sketch, "E1455", {"start": v(595.84, 1773.42) * mm, "end": v(600.33, 1779.78) * mm});
            skLineSegment(sketch, "E1456", {"start": v(600.33, 1779.78) * mm, "end": v(605.13, 1786.4) * mm});
            skLineSegment(sketch, "E1457", {"start": v(605.13, 1786.4) * mm, "end": v(610.27, 1793.23) * mm});
            skLineSegment(sketch, "E1458", {"start": v(610.27, 1793.23) * mm, "end": v(615.73, 1800.3) * mm});
            skLineSegment(sketch, "E1459", {"start": v(615.73, 1800.3) * mm, "end": v(621.53, 1807.58) * mm});
            skLineSegment(sketch, "E1460", {"start": v(621.53, 1807.58) * mm, "end": v(627.68, 1815.07) * mm});
            skLineSegment(sketch, "E1461", {"start": v(627.68, 1815.07) * mm, "end": v(634.18, 1822.76) * mm});
            skLineSegment(sketch, "E1462", {"start": v(634.18, 1822.76) * mm, "end": v(641.04, 1830.64) * mm});
            skLineSegment(sketch, "E1463", {"start": v(641.04, 1830.64) * mm, "end": v(648.27, 1838.7) * mm});
            skLineSegment(sketch, "E1464", {"start": v(648.27, 1838.7) * mm, "end": v(655.87, 1846.94) * mm});
            skLineSegment(sketch, "E1465", {"start": v(655.87, 1846.94) * mm, "end": v(663.86, 1855.34) * mm});
            skLineSegment(sketch, "E1466", {"start": v(663.86, 1855.34) * mm, "end": v(672.23, 1863.9) * mm});
            skLineSegment(sketch, "E1467", {"start": v(672.23, 1863.9) * mm, "end": v(681, 1872.6) * mm});
            skLineSegment(sketch, "E1468", {"start": v(681, 1872.6) * mm, "end": v(690.16, 1881.43) * mm});
            skLineSegment(sketch, "E1469", {"start": v(690.16, 1881.43) * mm, "end": v(699.73, 1890.4) * mm});
            skLineSegment(sketch, "E1470", {"start": v(699.73, 1890.4) * mm, "end": v(709.7, 1899.47) * mm});
            skLineSegment(sketch, "E1471", {"start": v(709.7, 1899.47) * mm, "end": v(720.1, 1908.66) * mm});
            skLineSegment(sketch, "E1472", {"start": v(720.1, 1908.66) * mm, "end": v(730.91, 1917.93) * mm});
            skLineSegment(sketch, "E1473", {"start": v(730.91, 1917.93) * mm, "end": v(742.16, 1927.3) * mm});
            skLineSegment(sketch, "E1474", {"start": v(742.16, 1927.3) * mm, "end": v(753.83, 1936.74) * mm});
            skLineSegment(sketch, "E1475", {"start": v(753.83, 1936.74) * mm, "end": v(765.94, 1946.24) * mm});
            skLineSegment(sketch, "E1476", {"start": v(765.94, 1946.24) * mm, "end": v(778.48, 1955.8) * mm});
            skLineSegment(sketch, "E1477", {"start": v(778.48, 1955.8) * mm, "end": v(791.47, 1965.39) * mm});
            skLineSegment(sketch, "E1478", {"start": v(791.47, 1965.39) * mm, "end": v(804.9, 1975.02) * mm});
            skLineSegment(sketch, "E1479", {"start": v(804.9, 1975.02) * mm, "end": v(818.8, 1984.66) * mm});
            skLineSegment(sketch, "E1480", {"start": v(818.8, 1984.66) * mm, "end": v(833.14, 1994.32) * mm});
            skLineSegment(sketch, "E1481", {"start": v(833.14, 1994.32) * mm, "end": v(847.93, 2003.98) * mm});
            skLineSegment(sketch, "E1482", {"start": v(847.93, 2003.98) * mm, "end": v(860.55, 2007.46) * mm});
            skLineSegment(sketch, "E1483", {"start": v(860.55, 2007.46) * mm, "end": v(920.3, 1980.78) * mm});
            skLineSegment(sketch, "E1484", {"start": v(920.3, 1980.78) * mm, "end": v(926.12, 1969.07) * mm});
            skLineSegment(sketch, "E1485", {"start": v(926.12, 1969.07) * mm, "end": v(928.81, 1951.6) * mm});
            skLineSegment(sketch, "E1486", {"start": v(928.81, 1951.6) * mm, "end": v(931.2, 1934.48) * mm});
            skLineSegment(sketch, "E1487", {"start": v(931.2, 1934.48) * mm, "end": v(933.28, 1917.7) * mm});
            skLineSegment(sketch, "E1488", {"start": v(933.28, 1917.7) * mm, "end": v(935.08, 1901.26) * mm});
            skLineSegment(sketch, "E1489", {"start": v(935.08, 1901.26) * mm, "end": v(936.6, 1885.19) * mm});
            skLineSegment(sketch, "E1490", {"start": v(936.6, 1885.19) * mm, "end": v(937.87, 1869.47) * mm});
            skLineSegment(sketch, "E1491", {"start": v(937.87, 1869.47) * mm, "end": v(938.87, 1854.1) * mm});
            skLineSegment(sketch, "E1492", {"start": v(938.87, 1854.1) * mm, "end": v(939.64, 1839.12) * mm});
            skLineSegment(sketch, "E1493", {"start": v(939.64, 1839.12) * mm, "end": v(940.17, 1824.5) * mm});
            skLineSegment(sketch, "E1494", {"start": v(940.17, 1824.5) * mm, "end": v(940.48, 1810.25) * mm});
            skLineSegment(sketch, "E1495", {"start": v(940.48, 1810.25) * mm, "end": v(940.58, 1796.38) * mm});
            skLineSegment(sketch, "E1496", {"start": v(940.58, 1796.38) * mm, "end": v(940.48, 1782.9) * mm});
            skLineSegment(sketch, "E1497", {"start": v(940.48, 1782.9) * mm, "end": v(940.2, 1769.78) * mm});
            skLineSegment(sketch, "E1498", {"start": v(940.2, 1769.78) * mm, "end": v(939.74, 1757.06) * mm});
            skLineSegment(sketch, "E1499", {"start": v(939.74, 1757.06) * mm, "end": v(939.1, 1744.73) * mm});
            skLineSegment(sketch, "E1500", {"start": v(939.1, 1744.73) * mm, "end": v(938.33, 1732.78) * mm});
            skLineSegment(sketch, "E1501", {"start": v(938.33, 1732.78) * mm, "end": v(937.4, 1721.23) * mm});
            skLineSegment(sketch, "E1502", {"start": v(937.4, 1721.23) * mm, "end": v(936.34, 1710.07) * mm});
            skLineSegment(sketch, "E1503", {"start": v(936.34, 1710.07) * mm, "end": v(935.16, 1699.3) * mm});
            skLineSegment(sketch, "E1504", {"start": v(935.16, 1699.3) * mm, "end": v(933.88, 1688.93) * mm});
            skLineSegment(sketch, "E1505", {"start": v(933.88, 1688.93) * mm, "end": v(932.5, 1678.96) * mm});
            skLineSegment(sketch, "E1506", {"start": v(932.5, 1678.96) * mm, "end": v(931.02, 1669.38) * mm});
            skLineSegment(sketch, "E1507", {"start": v(931.02, 1669.38) * mm, "end": v(929.47, 1660.2) * mm});
            skLineSegment(sketch, "E1508", {"start": v(929.47, 1660.2) * mm, "end": v(927.85, 1651.42) * mm});
            skLineSegment(sketch, "E1509", {"start": v(927.85, 1651.42) * mm, "end": v(926.18, 1643.03) * mm});
            skLineSegment(sketch, "E1510", {"start": v(926.18, 1643.03) * mm, "end": v(924.48, 1635.04) * mm});
            skLineSegment(sketch, "E1511", {"start": v(924.48, 1635.04) * mm, "end": v(922.73, 1627.45) * mm});
            skLineSegment(sketch, "E1512", {"start": v(922.73, 1627.45) * mm, "end": v(920.97, 1620.25) * mm});
            skLineSegment(sketch, "E1513", {"start": v(920.97, 1620.25) * mm, "end": v(919.2, 1613.45) * mm});
            skLineSegment(sketch, "E1514", {"start": v(919.2, 1613.45) * mm, "end": v(917.44, 1607.04) * mm});
            skLineSegment(sketch, "E1515", {"start": v(917.44, 1607.04) * mm, "end": v(915.68, 1601.02) * mm});
            skLineSegment(sketch, "E1516", {"start": v(915.68, 1601.02) * mm, "end": v(913.95, 1595.39) * mm});
            skLineSegment(sketch, "E1517", {"start": v(913.95, 1595.39) * mm, "end": v(912.26, 1590.15) * mm});
            skLineSegment(sketch, "E1518", {"start": v(912.26, 1590.15) * mm, "end": v(910.6, 1585.29) * mm});
            skLineSegment(sketch, "E1519", {"start": v(910.6, 1585.29) * mm, "end": v(909.02, 1580.81) * mm});
            skLineSegment(sketch, "E1520", {"start": v(909.02, 1580.81) * mm, "end": v(911.46, 1578.69) * mm});
            skLineSegment(sketch, "E1521", {"start": v(911.46, 1578.69) * mm, "end": v(996.13, 1526.67) * mm});
            skLineSegment(sketch, "E1522", {"start": v(996.13, 1526.67) * mm, "end": v(999.13, 1525.46) * mm});
            skLineSegment(sketch, "E1523", {"start": v(999.13, 1525.46) * mm, "end": v(1002.4, 1528.9) * mm});
            skLineSegment(sketch, "E1524", {"start": v(1002.4, 1528.9) * mm, "end": v(1005.99, 1532.57) * mm});
            skLineSegment(sketch, "E1525", {"start": v(1005.99, 1532.57) * mm, "end": v(1009.9, 1536.45) * mm});
            skLineSegment(sketch, "E1526", {"start": v(1009.9, 1536.45) * mm, "end": v(1014.14, 1540.54) * mm});
            skLineSegment(sketch, "E1527", {"start": v(1014.14, 1540.54) * mm, "end": v(1018.72, 1544.82) * mm});
            skLineSegment(sketch, "E1528", {"start": v(1018.72, 1544.82) * mm, "end": v(1023.63, 1549.3) * mm});
            skLineSegment(sketch, "E1529", {"start": v(1023.63, 1549.3) * mm, "end": v(1028.9, 1553.95) * mm});
            skLineSegment(sketch, "E1530", {"start": v(1028.9, 1553.95) * mm, "end": v(1034.53, 1558.78) * mm});
            skLineSegment(sketch, "E1531", {"start": v(1034.53, 1558.78) * mm, "end": v(1040.51, 1563.76) * mm});
            skLineSegment(sketch, "E1532", {"start": v(1040.51, 1563.76) * mm, "end": v(1046.87, 1568.9) * mm});
            skLineSegment(sketch, "E1533", {"start": v(1046.87, 1568.9) * mm, "end": v(1053.6, 1574.18) * mm});
            skLineSegment(sketch, "E1534", {"start": v(1053.6, 1574.18) * mm, "end": v(1060.7, 1579.59) * mm});
            skLineSegment(sketch, "E1535", {"start": v(1060.7, 1579.59) * mm, "end": v(1068.19, 1585.12) * mm});
            skLineSegment(sketch, "E1536", {"start": v(1068.19, 1585.12) * mm, "end": v(1076.06, 1590.76) * mm});
            skLineSegment(sketch, "E1537", {"start": v(1076.06, 1590.76) * mm, "end": v(1084.33, 1596.51) * mm});
            skLineSegment(sketch, "E1538", {"start": v(1084.33, 1596.51) * mm, "end": v(1093, 1602.35) * mm});
            skLineSegment(sketch, "E1539", {"start": v(1093, 1602.35) * mm, "end": v(1102.07, 1608.27) * mm});
            skLineSegment(sketch, "E1540", {"start": v(1102.07, 1608.27) * mm, "end": v(1111.55, 1614.25) * mm});
            skLineSegment(sketch, "E1541", {"start": v(1111.55, 1614.25) * mm, "end": v(1121.43, 1620.3) * mm});
            skLineSegment(sketch, "E1542", {"start": v(1121.43, 1620.3) * mm, "end": v(1131.73, 1626.4) * mm});
            skLineSegment(sketch, "E1543", {"start": v(1131.73, 1626.4) * mm, "end": v(1142.45, 1632.54) * mm});
            skLineSegment(sketch, "E1544", {"start": v(1142.45, 1632.54) * mm, "end": v(1153.6, 1638.7) * mm});
            skLineSegment(sketch, "E1545", {"start": v(1153.6, 1638.7) * mm, "end": v(1165.15, 1644.88) * mm});
            skLineSegment(sketch, "E1546", {"start": v(1165.15, 1644.88) * mm, "end": v(1177.14, 1651.07) * mm});
            skLineSegment(sketch, "E1547", {"start": v(1177.14, 1651.07) * mm, "end": v(1189.56, 1657.24) * mm});
            skLineSegment(sketch, "E1548", {"start": v(1189.56, 1657.24) * mm, "end": v(1202.4, 1663.4) * mm});
            skLineSegment(sketch, "E1549", {"start": v(1202.4, 1663.4) * mm, "end": v(1215.69, 1669.54) * mm});
            skLineSegment(sketch, "E1550", {"start": v(1215.69, 1669.54) * mm, "end": v(1229.4, 1675.64) * mm});
            skLineSegment(sketch, "E1551", {"start": v(1229.4, 1675.64) * mm, "end": v(1243.56, 1681.68) * mm});
            skLineSegment(sketch, "E1552", {"start": v(1243.56, 1681.68) * mm, "end": v(1258.15, 1687.66) * mm});
            skLineSegment(sketch, "E1553", {"start": v(1258.15, 1687.66) * mm, "end": v(1273.18, 1693.57) * mm});
            skLineSegment(sketch, "E1554", {"start": v(1273.18, 1693.57) * mm, "end": v(1288.65, 1699.4) * mm});
            skLineSegment(sketch, "E1555", {"start": v(1288.65, 1699.4) * mm, "end": v(1304.56, 1705.12) * mm});
            skLineSegment(sketch, "E1556", {"start": v(1304.56, 1705.12) * mm, "end": v(1320.92, 1710.74) * mm});
            skLineSegment(sketch, "E1557", {"start": v(1320.92, 1710.74) * mm, "end": v(1337.7, 1716.23) * mm});
            skLineSegment(sketch, "E1558", {"start": v(1337.7, 1716.23) * mm, "end": v(1350.8, 1716.33) * mm});
            skLineSegment(sketch, "E1559", {"start": v(1350.8, 1716.33) * mm, "end": v(1401.6, 1675.1) * mm});
            skLineSegment(sketch, "E1560", {"start": v(1401.6, 1675.1) * mm, "end": v(1404.2, 1662.27) * mm});
            skLineSegment(sketch, "E1561", {"start": v(1404.2, 1662.27) * mm, "end": v(1402.28, 1644.7) * mm});
            skLineSegment(sketch, "E1562", {"start": v(1402.28, 1644.7) * mm, "end": v(1400.14, 1627.55) * mm});
            skLineSegment(sketch, "E1563", {"start": v(1400.14, 1627.55) * mm, "end": v(1397.82, 1610.8) * mm});
            skLineSegment(sketch, "E1564", {"start": v(1397.82, 1610.8) * mm, "end": v(1395.3, 1594.46) * mm});
            skLineSegment(sketch, "E1565", {"start": v(1395.3, 1594.46) * mm, "end": v(1392.61, 1578.54) * mm});
            skLineSegment(sketch, "E1566", {"start": v(1392.61, 1578.54) * mm, "end": v(1389.76, 1563.03) * mm});
            skLineSegment(sketch, "E1567", {"start": v(1389.76, 1563.03) * mm, "end": v(1386.76, 1547.93) * mm});
            skLineSegment(sketch, "E1568", {"start": v(1386.76, 1547.93) * mm, "end": v(1383.62, 1533.25) * mm});
            skLineSegment(sketch, "E1569", {"start": v(1383.62, 1533.25) * mm, "end": v(1380.35, 1519) * mm});
            skLineSegment(sketch, "E1570", {"start": v(1380.35, 1519) * mm, "end": v(1376.96, 1505.15) * mm});
            skLineSegment(sketch, "E1571", {"start": v(1376.96, 1505.15) * mm, "end": v(1373.47, 1491.73) * mm});
            skLineSegment(sketch, "E1572", {"start": v(1373.47, 1491.73) * mm, "end": v(1369.89, 1478.72) * mm});
            skLineSegment(sketch, "E1573", {"start": v(1369.89, 1478.72) * mm, "end": v(1366.22, 1466.14) * mm});
            skLineSegment(sketch, "E1574", {"start": v(1366.22, 1466.14) * mm, "end": v(1362.48, 1453.97) * mm});
            skLineSegment(sketch, "E1575", {"start": v(1362.48, 1453.97) * mm, "end": v(1358.68, 1442.22) * mm});
            skLineSegment(sketch, "E1576", {"start": v(1358.68, 1442.22) * mm, "end": v(1354.83, 1430.88) * mm});
            skLineSegment(sketch, "E1577", {"start": v(1354.83, 1430.88) * mm, "end": v(1350.95, 1419.96) * mm});
            skLineSegment(sketch, "E1578", {"start": v(1350.95, 1419.96) * mm, "end": v(1347.04, 1409.46) * mm});
            skLineSegment(sketch, "E1579", {"start": v(1347.04, 1409.46) * mm, "end": v(1343.11, 1399.36) * mm});
            skLineSegment(sketch, "E1580", {"start": v(1343.11, 1399.36) * mm, "end": v(1339.18, 1389.68) * mm});
            skLineSegment(sketch, "E1581", {"start": v(1339.18, 1389.68) * mm, "end": v(1335.26, 1380.4) * mm});
            skLineSegment(sketch, "E1582", {"start": v(1335.26, 1380.4) * mm, "end": v(1331.36, 1371.53) * mm});
            skLineSegment(sketch, "E1583", {"start": v(1331.36, 1371.53) * mm, "end": v(1327.49, 1363.07) * mm});
            skLineSegment(sketch, "E1584", {"start": v(1327.49, 1363.07) * mm, "end": v(1323.66, 1355) * mm});
            skLineSegment(sketch, "E1585", {"start": v(1323.66, 1355) * mm, "end": v(1319.87, 1347.33) * mm});
            skLineSegment(sketch, "E1586", {"start": v(1319.87, 1347.33) * mm, "end": v(1316.16, 1340.06) * mm});
            skLineSegment(sketch, "E1587", {"start": v(1316.16, 1340.06) * mm, "end": v(1312.5, 1333.18) * mm});
            skLineSegment(sketch, "E1588", {"start": v(1312.5, 1333.18) * mm, "end": v(1308.94, 1326.68) * mm});
            skLineSegment(sketch, "E1589", {"start": v(1308.94, 1326.68) * mm, "end": v(1305.47, 1320.57) * mm});
            skLineSegment(sketch, "E1590", {"start": v(1305.47, 1320.57) * mm, "end": v(1302.1, 1314.83) * mm});
            skLineSegment(sketch, "E1591", {"start": v(1302.1, 1314.83) * mm, "end": v(1298.86, 1309.47) * mm});
            skLineSegment(sketch, "E1592", {"start": v(1298.86, 1309.47) * mm, "end": v(1295.73, 1304.48) * mm});
            skLineSegment(sketch, "E1593", {"start": v(1295.73, 1304.48) * mm, "end": v(1292.73, 1299.85) * mm});
            skLineSegment(sketch, "E1594", {"start": v(1292.73, 1299.85) * mm, "end": v(1289.88, 1295.59) * mm});
            skLineSegment(sketch, "E1595", {"start": v(1289.88, 1295.59) * mm, "end": v(1287.19, 1291.68) * mm});
            skLineSegment(sketch, "E1596", {"start": v(1287.19, 1291.68) * mm, "end": v(1289, 1289) * mm});
            skLineSegment(sketch, "E1597", {"start": v(1289, 1289) * mm, "end": v(1357.32, 1216.84) * mm});
            skLineSegment(sketch, "E1598", {"start": v(1357.32, 1216.84) * mm, "end": v(1359.9, 1214.89) * mm});
            skLineSegment(sketch, "E1599", {"start": v(1359.9, 1214.89) * mm, "end": v(1363.95, 1217.37) * mm});
            skLineSegment(sketch, "E1600", {"start": v(1363.95, 1217.37) * mm, "end": v(1368.37, 1219.98) * mm});
            skLineSegment(sketch, "E1601", {"start": v(1368.37, 1219.98) * mm, "end": v(1373.15, 1222.72) * mm});
            skLineSegment(sketch, "E1602", {"start": v(1373.15, 1222.72) * mm, "end": v(1378.3, 1225.57) * mm});
            skLineSegment(sketch, "E1603", {"start": v(1378.3, 1225.57) * mm, "end": v(1383.83, 1228.52) * mm});
            skLineSegment(sketch, "E1604", {"start": v(1383.83, 1228.52) * mm, "end": v(1389.74, 1231.57) * mm});
            skLineSegment(sketch, "E1605", {"start": v(1389.74, 1231.57) * mm, "end": v(1396.04, 1234.7) * mm});
            skLineSegment(sketch, "E1606", {"start": v(1396.04, 1234.7) * mm, "end": v(1402.72, 1237.9) * mm});
            skLineSegment(sketch, "E1607", {"start": v(1402.72, 1237.9) * mm, "end": v(1409.8, 1241.17) * mm});
            skLineSegment(sketch, "E1608", {"start": v(1409.8, 1241.17) * mm, "end": v(1417.26, 1244.5) * mm});
            skLineSegment(sketch, "E1609", {"start": v(1417.26, 1244.5) * mm, "end": v(1425.12, 1247.85) * mm});
            skLineSegment(sketch, "E1610", {"start": v(1425.12, 1247.85) * mm, "end": v(1433.38, 1251.24) * mm});
            skLineSegment(sketch, "E1611", {"start": v(1433.38, 1251.24) * mm, "end": v(1442.05, 1254.64) * mm});
            skLineSegment(sketch, "E1612", {"start": v(1442.05, 1254.64) * mm, "end": v(1451.12, 1258.06) * mm});
            skLineSegment(sketch, "E1613", {"start": v(1451.12, 1258.06) * mm, "end": v(1460.6, 1261.47) * mm});
            skLineSegment(sketch, "E1614", {"start": v(1460.6, 1261.47) * mm, "end": v(1470.48, 1264.86) * mm});
            skLineSegment(sketch, "E1615", {"start": v(1470.48, 1264.86) * mm, "end": v(1480.77, 1268.23) * mm});
            skLineSegment(sketch, "E1616", {"start": v(1480.77, 1268.23) * mm, "end": v(1491.47, 1271.56) * mm});
            skLineSegment(sketch, "E1617", {"start": v(1491.47, 1271.56) * mm, "end": v(1502.59, 1274.84) * mm});
            skLineSegment(sketch, "E1618", {"start": v(1502.59, 1274.84) * mm, "end": v(1514.11, 1278.07) * mm});
            skLineSegment(sketch, "E1619", {"start": v(1514.11, 1278.07) * mm, "end": v(1526.06, 1281.22) * mm});
            skLineSegment(sketch, "E1620", {"start": v(1526.06, 1281.22) * mm, "end": v(1538.41, 1284.3) * mm});
            skLineSegment(sketch, "E1621", {"start": v(1538.41, 1284.3) * mm, "end": v(1551.18, 1287.27) * mm});
            skLineSegment(sketch, "E1622", {"start": v(1551.18, 1287.27) * mm, "end": v(1564.36, 1290.14) * mm});
            skLineSegment(sketch, "E1623", {"start": v(1564.36, 1290.14) * mm, "end": v(1577.95, 1292.9) * mm});
            skLineSegment(sketch, "E1624", {"start": v(1577.95, 1292.9) * mm, "end": v(1591.96, 1295.52) * mm});
            skLineSegment(sketch, "E1625", {"start": v(1591.96, 1295.52) * mm, "end": v(1606.38, 1298.01) * mm});
            skLineSegment(sketch, "E1626", {"start": v(1606.38, 1298.01) * mm, "end": v(1621.2, 1300.35) * mm});
            skLineSegment(sketch, "E1627", {"start": v(1621.2, 1300.35) * mm, "end": v(1636.44, 1302.52) * mm});
            skLineSegment(sketch, "E1628", {"start": v(1636.44, 1302.52) * mm, "end": v(1652.08, 1304.52) * mm});
            skLineSegment(sketch, "E1629", {"start": v(1652.08, 1304.52) * mm, "end": v(1668.13, 1306.34) * mm});
            skLineSegment(sketch, "E1630", {"start": v(1668.13, 1306.34) * mm, "end": v(1684.58, 1307.96) * mm});
            skLineSegment(sketch, "E1631", {"start": v(1684.58, 1307.96) * mm, "end": v(1701.43, 1309.37) * mm});
            skLineSegment(sketch, "E1632", {"start": v(1701.43, 1309.37) * mm, "end": v(1718.68, 1310.57) * mm});
            skLineSegment(sketch, "E1633", {"start": v(1718.68, 1310.57) * mm, "end": v(1736.32, 1311.53) * mm});
            skLineSegment(sketch, "E1634", {"start": v(1736.32, 1311.53) * mm, "end": v(1748.99, 1308.24) * mm});
            skLineSegment(sketch, "E1635", {"start": v(1748.99, 1308.24) * mm, "end": v(1787.4, 1255.26) * mm});
            skLineSegment(sketch, "E1636", {"start": v(1787.4, 1255.26) * mm, "end": v(1786.58, 1242.2) * mm});
            skLineSegment(sketch, "E1637", {"start": v(1786.58, 1242.2) * mm, "end": v(1780.18, 1225.73) * mm});
            skLineSegment(sketch, "E1638", {"start": v(1780.18, 1225.73) * mm, "end": v(1773.68, 1209.7) * mm});
            skLineSegment(sketch, "E1639", {"start": v(1773.68, 1209.7) * mm, "end": v(1767.1, 1194.13) * mm});
            skLineSegment(sketch, "E1640", {"start": v(1767.1, 1194.13) * mm, "end": v(1760.44, 1179) * mm});
            skLineSegment(sketch, "E1641", {"start": v(1760.44, 1179) * mm, "end": v(1753.72, 1164.31) * mm});
            skLineSegment(sketch, "E1642", {"start": v(1753.72, 1164.31) * mm, "end": v(1746.95, 1150.07) * mm});
            skLineSegment(sketch, "E1643", {"start": v(1746.95, 1150.07) * mm, "end": v(1740.14, 1136.27) * mm});
            skLineSegment(sketch, "E1644", {"start": v(1740.14, 1136.27) * mm, "end": v(1733.3, 1122.9) * mm});
            skLineSegment(sketch, "E1645", {"start": v(1733.3, 1122.9) * mm, "end": v(1726.46, 1109.98) * mm});
            skLineSegment(sketch, "E1646", {"start": v(1726.46, 1109.98) * mm, "end": v(1719.6, 1097.48) * mm});
            skLineSegment(sketch, "E1647", {"start": v(1719.6, 1097.48) * mm, "end": v(1712.76, 1085.42) * mm});
            skLineSegment(sketch, "E1648", {"start": v(1712.76, 1085.42) * mm, "end": v(1705.93, 1073.79) * mm});
            skLineSegment(sketch, "E1649", {"start": v(1705.93, 1073.79) * mm, "end": v(1699.13, 1062.58) * mm});
            skLineSegment(sketch, "E1650", {"start": v(1699.13, 1062.58) * mm, "end": v(1692.37, 1051.8) * mm});
            skLineSegment(sketch, "E1651", {"start": v(1692.37, 1051.8) * mm, "end": v(1685.66, 1041.42) * mm});
            skLineSegment(sketch, "E1652", {"start": v(1685.66, 1041.42) * mm, "end": v(1679, 1031.47) * mm});
            skLineSegment(sketch, "E1653", {"start": v(1679, 1031.47) * mm, "end": v(1672.43, 1021.93) * mm});
            skLineSegment(sketch, "E1654", {"start": v(1672.43, 1021.93) * mm, "end": v(1665.93, 1012.8) * mm});
            skLineSegment(sketch, "E1655", {"start": v(1665.93, 1012.8) * mm, "end": v(1659.53, 1004.06) * mm});
            skLineSegment(sketch, "E1656", {"start": v(1659.53, 1004.06) * mm, "end": v(1653.23, 995.72) * mm});
            skLineSegment(sketch, "E1657", {"start": v(1653.23, 995.72) * mm, "end": v(1647.04, 987.78) * mm});
            skLineSegment(sketch, "E1658", {"start": v(1647.04, 987.78) * mm, "end": v(1640.98, 980.22) * mm});
            skLineSegment(sketch, "E1659", {"start": v(1640.98, 980.22) * mm, "end": v(1635.04, 973.04) * mm});
            skLineSegment(sketch, "E1660", {"start": v(1635.04, 973.04) * mm, "end": v(1629.25, 966.24) * mm});
            skLineSegment(sketch, "E1661", {"start": v(1629.25, 966.24) * mm, "end": v(1623.62, 959.82) * mm});
            skLineSegment(sketch, "E1662", {"start": v(1623.62, 959.82) * mm, "end": v(1618.14, 953.75) * mm});
            skLineSegment(sketch, "E1663", {"start": v(1618.14, 953.75) * mm, "end": v(1612.84, 948.05) * mm});
            skLineSegment(sketch, "E1664", {"start": v(1612.84, 948.05) * mm, "end": v(1607.71, 942.7) * mm});
            skLineSegment(sketch, "E1665", {"start": v(1607.71, 942.7) * mm, "end": v(1602.78, 937.69) * mm});
            skLineSegment(sketch, "E1666", {"start": v(1602.78, 937.69) * mm, "end": v(1598.04, 933.02) * mm});
            skLineSegment(sketch, "E1667", {"start": v(1598.04, 933.02) * mm, "end": v(1593.51, 928.68) * mm});
            skLineSegment(sketch, "E1668", {"start": v(1593.51, 928.68) * mm, "end": v(1589.2, 924.67) * mm});
            skLineSegment(sketch, "E1669", {"start": v(1589.2, 924.67) * mm, "end": v(1585.11, 920.98) * mm});
            skLineSegment(sketch, "E1670", {"start": v(1585.11, 920.98) * mm, "end": v(1581.25, 917.6) * mm});
            skLineSegment(sketch, "E1671", {"start": v(1581.25, 917.6) * mm, "end": v(1577.64, 914.51) * mm});
            skLineSegment(sketch, "E1672", {"start": v(1577.64, 914.51) * mm, "end": v(1578.69, 911.46) * mm});
            skLineSegment(sketch, "E1673", {"start": v(1578.69, 911.46) * mm, "end": v(1626.01, 824.07) * mm});
            skLineSegment(sketch, "E1674", {"start": v(1626.01, 824.07) * mm, "end": v(1628, 821.52) * mm});
            skLineSegment(sketch, "E1675", {"start": v(1628, 821.52) * mm, "end": v(1632.56, 822.87) * mm});
            skLineSegment(sketch, "E1676", {"start": v(1632.56, 822.87) * mm, "end": v(1637.5, 824.25) * mm});
            skLineSegment(sketch, "E1677", {"start": v(1637.5, 824.25) * mm, "end": v(1642.82, 825.66) * mm});
            skLineSegment(sketch, "E1678", {"start": v(1642.82, 825.66) * mm, "end": v(1648.54, 827.08) * mm});
            skLineSegment(sketch, "E1679", {"start": v(1648.54, 827.08) * mm, "end": v(1654.65, 828.5) * mm});
            skLineSegment(sketch, "E1680", {"start": v(1654.65, 828.5) * mm, "end": v(1661.14, 829.92) * mm});
            skLineSegment(sketch, "E1681", {"start": v(1661.14, 829.92) * mm, "end": v(1668.03, 831.31) * mm});
            skLineSegment(sketch, "E1682", {"start": v(1668.03, 831.31) * mm, "end": v(1675.32, 832.68) * mm});
            skLineSegment(sketch, "E1683", {"start": v(1675.32, 832.68) * mm, "end": v(1683, 834) * mm});
            skLineSegment(sketch, "E1684", {"start": v(1683, 834) * mm, "end": v(1691.06, 835.27) * mm});
            skLineSegment(sketch, "E1685", {"start": v(1691.06, 835.27) * mm, "end": v(1699.53, 836.48) * mm});
            skLineSegment(sketch, "E1686", {"start": v(1699.53, 836.48) * mm, "end": v(1708.39, 837.62) * mm});
            skLineSegment(sketch, "E1687", {"start": v(1708.39, 837.62) * mm, "end": v(1717.64, 838.66) * mm});
            skLineSegment(sketch, "E1688", {"start": v(1717.64, 838.66) * mm, "end": v(1727.28, 839.61) * mm});
            skLineSegment(sketch, "E1689", {"start": v(1727.28, 839.61) * mm, "end": v(1737.32, 840.45) * mm});
            skLineSegment(sketch, "E1690", {"start": v(1737.32, 840.45) * mm, "end": v(1747.74, 841.17) * mm});
            skLineSegment(sketch, "E1691", {"start": v(1747.74, 841.17) * mm, "end": v(1758.55, 841.76) * mm});
            skLineSegment(sketch, "E1692", {"start": v(1758.55, 841.76) * mm, "end": v(1769.76, 842.21) * mm});
            skLineSegment(sketch, "E1693", {"start": v(1769.76, 842.21) * mm, "end": v(1781.34, 842.5) * mm});
            skLineSegment(sketch, "E1694", {"start": v(1781.34, 842.5) * mm, "end": v(1793.31, 842.64) * mm});
            skLineSegment(sketch, "E1695", {"start": v(1793.31, 842.64) * mm, "end": v(1805.66, 842.6) * mm});
            skLineSegment(sketch, "E1696", {"start": v(1805.66, 842.6) * mm, "end": v(1818.39, 842.36) * mm});
            skLineSegment(sketch, "E1697", {"start": v(1818.39, 842.36) * mm, "end": v(1831.5, 841.93) * mm});
            skLineSegment(sketch, "E1698", {"start": v(1831.5, 841.93) * mm, "end": v(1844.97, 841.3) * mm});
            skLineSegment(sketch, "E1699", {"start": v(1844.97, 841.3) * mm, "end": v(1858.81, 840.44) * mm});
            skLineSegment(sketch, "E1700", {"start": v(1858.81, 840.44) * mm, "end": v(1873.02, 839.35) * mm});
            skLineSegment(sketch, "E1701", {"start": v(1873.02, 839.35) * mm, "end": v(1887.59, 838.02) * mm});
            skLineSegment(sketch, "E1702", {"start": v(1887.59, 838.02) * mm, "end": v(1902.52, 836.44) * mm});
            skLineSegment(sketch, "E1703", {"start": v(1902.52, 836.44) * mm, "end": v(1917.8, 834.6) * mm});
            skLineSegment(sketch, "E1704", {"start": v(1917.8, 834.6) * mm, "end": v(1933.42, 832.48) * mm});
            skLineSegment(sketch, "E1705", {"start": v(1933.42, 832.48) * mm, "end": v(1949.4, 830.08) * mm});
            skLineSegment(sketch, "E1706", {"start": v(1949.4, 830.08) * mm, "end": v(1965.7, 827.4) * mm});
            skLineSegment(sketch, "E1707", {"start": v(1965.7, 827.4) * mm, "end": v(1982.35, 824.4) * mm});
            skLineSegment(sketch, "E1708", {"start": v(1982.35, 824.4) * mm, "end": v(1999.32, 821.08) * mm});
            skLineSegment(sketch, "E1709", {"start": v(1999.32, 821.08) * mm, "end": v(2016.6, 817.45) * mm});
            skLineSegment(sketch, "E1710", {"start": v(2016.6, 817.45) * mm, "end": v(2028, 810.99) * mm});
            skLineSegment(sketch, "E1711", {"start": v(2028, 810.99) * mm, "end": v(2051.37, 749.88) * mm});
            skLineSegment(sketch, "E1712", {"start": v(2051.37, 749.88) * mm, "end": v(2047.2, 737.47) * mm});
            skLineSegment(sketch, "E1713", {"start": v(2047.2, 737.47) * mm, "end": v(2036.76, 723.22) * mm});
            skLineSegment(sketch, "E1714", {"start": v(2036.76, 723.22) * mm, "end": v(2026.34, 709.43) * mm});
            skLineSegment(sketch, "E1715", {"start": v(2026.34, 709.43) * mm, "end": v(2015.94, 696.09) * mm});
            skLineSegment(sketch, "E1716", {"start": v(2015.94, 696.09) * mm, "end": v(2005.6, 683.2) * mm});
            skLineSegment(sketch, "E1717", {"start": v(2005.6, 683.2) * mm, "end": v(1995.3, 670.75) * mm});
            skLineSegment(sketch, "E1718", {"start": v(1995.3, 670.75) * mm, "end": v(1985.08, 658.74) * mm});
            skLineSegment(sketch, "E1719", {"start": v(1985.08, 658.74) * mm, "end": v(1974.94, 647.17) * mm});
            skLineSegment(sketch, "E1720", {"start": v(1974.94, 647.17) * mm, "end": v(1964.88, 636.03) * mm});
            skLineSegment(sketch, "E1721", {"start": v(1964.88, 636.03) * mm, "end": v(1954.91, 625.31) * mm});
            skLineSegment(sketch, "E1722", {"start": v(1954.91, 625.31) * mm, "end": v(1945.06, 615.02) * mm});
            skLineSegment(sketch, "E1723", {"start": v(1945.06, 615.02) * mm, "end": v(1935.33, 605.14) * mm});
            skLineSegment(sketch, "E1724", {"start": v(1935.33, 605.14) * mm, "end": v(1925.72, 595.67) * mm});
            skLineSegment(sketch, "E1725", {"start": v(1925.72, 595.67) * mm, "end": v(1916.25, 586.6) * mm});
            skLineSegment(sketch, "E1726", {"start": v(1916.25, 586.6) * mm, "end": v(1906.92, 577.94) * mm});
            skLineSegment(sketch, "E1727", {"start": v(1906.92, 577.94) * mm, "end": v(1897.76, 569.66) * mm});
            skLineSegment(sketch, "E1728", {"start": v(1897.76, 569.66) * mm, "end": v(1888.76, 561.77) * mm});
            skLineSegment(sketch, "E1729", {"start": v(1888.76, 561.77) * mm, "end": v(1879.94, 554.25) * mm});
            skLineSegment(sketch, "E1730", {"start": v(1879.94, 554.25) * mm, "end": v(1871.3, 547.1) * mm});
            skLineSegment(sketch, "E1731", {"start": v(1871.3, 547.1) * mm, "end": v(1862.85, 540.33) * mm});
            skLineSegment(sketch, "E1732", {"start": v(1862.85, 540.33) * mm, "end": v(1854.6, 533.9) * mm});
            skLineSegment(sketch, "E1733", {"start": v(1854.6, 533.9) * mm, "end": v(1846.57, 527.83) * mm});
            skLineSegment(sketch, "E1734", {"start": v(1846.57, 527.83) * mm, "end": v(1838.76, 522.1) * mm});
            skLineSegment(sketch, "E1735", {"start": v(1838.76, 522.1) * mm, "end": v(1831.17, 516.7) * mm});
            skLineSegment(sketch, "E1736", {"start": v(1831.17, 516.7) * mm, "end": v(1823.82, 511.64) * mm});
            skLineSegment(sketch, "E1737", {"start": v(1823.82, 511.64) * mm, "end": v(1816.71, 506.89) * mm});
            skLineSegment(sketch, "E1738", {"start": v(1816.71, 506.89) * mm, "end": v(1809.85, 502.45) * mm});
            skLineSegment(sketch, "E1739", {"start": v(1809.85, 502.45) * mm, "end": v(1803.25, 498.31) * mm});
            skLineSegment(sketch, "E1740", {"start": v(1803.25, 498.31) * mm, "end": v(1796.92, 494.47) * mm});
            skLineSegment(sketch, "E1741", {"start": v(1796.92, 494.47) * mm, "end": v(1790.86, 490.9) * mm});
            skLineSegment(sketch, "E1742", {"start": v(1790.86, 490.9) * mm, "end": v(1785.07, 487.62) * mm});
            skLineSegment(sketch, "E1743", {"start": v(1785.07, 487.62) * mm, "end": v(1779.58, 484.6) * mm});
            skLineSegment(sketch, "E1744", {"start": v(1779.58, 484.6) * mm, "end": v(1774.37, 481.85) * mm});
            skLineSegment(sketch, "E1745", {"start": v(1774.37, 481.85) * mm, "end": v(1769.47, 479.34) * mm});
            skLineSegment(sketch, "E1746", {"start": v(1769.47, 479.34) * mm, "end": v(1764.87, 477.07) * mm});
            skLineSegment(sketch, "E1747", {"start": v(1764.87, 477.07) * mm, "end": v(1760.58, 475.03) * mm});
            skLineSegment(sketch, "E1748", {"start": v(1760.58, 475.03) * mm, "end": v(1760.8, 471.8) * mm});
            skLineSegment(sketch, "E1749", {"start": v(1760.8, 471.8) * mm, "end": v(1783.9, 375.15) * mm});
            skLineSegment(sketch, "E1750", {"start": v(1783.9, 375.15) * mm, "end": v(1785.15, 372.17) * mm});
            skLineSegment(sketch, "E1751", {"start": v(1785.15, 372.17) * mm, "end": v(1789.9, 372.3) * mm});
            skLineSegment(sketch, "E1752", {"start": v(1789.9, 372.3) * mm, "end": v(1795.03, 372.35) * mm});
            skLineSegment(sketch, "E1753", {"start": v(1795.03, 372.35) * mm, "end": v(1800.54, 372.33) * mm});
            skLineSegment(sketch, "E1754", {"start": v(1800.54, 372.33) * mm, "end": v(1806.43, 372.22) * mm});
            skLineSegment(sketch, "E1755", {"start": v(1806.43, 372.22) * mm, "end": v(1812.7, 372.02) * mm});
            skLineSegment(sketch, "E1756", {"start": v(1812.7, 372.02) * mm, "end": v(1819.34, 371.7) * mm});
            skLineSegment(sketch, "E1757", {"start": v(1819.34, 371.7) * mm, "end": v(1826.36, 371.27) * mm});
            skLineSegment(sketch, "E1758", {"start": v(1826.36, 371.27) * mm, "end": v(1833.74, 370.7) * mm});
            skLineSegment(sketch, "E1759", {"start": v(1833.74, 370.7) * mm, "end": v(1841.5, 370) * mm});
            skLineSegment(sketch, "E1760", {"start": v(1841.5, 370) * mm, "end": v(1849.63, 369.13) * mm});
            skLineSegment(sketch, "E1761", {"start": v(1849.63, 369.13) * mm, "end": v(1858.12, 368.1) * mm});
            skLineSegment(sketch, "E1762", {"start": v(1858.12, 368.1) * mm, "end": v(1866.96, 366.91) * mm});
            skLineSegment(sketch, "E1763", {"start": v(1866.96, 366.91) * mm, "end": v(1876.17, 365.53) * mm});
            skLineSegment(sketch, "E1764", {"start": v(1876.17, 365.53) * mm, "end": v(1885.73, 363.95) * mm});
            skLineSegment(sketch, "E1765", {"start": v(1885.73, 363.95) * mm, "end": v(1895.64, 362.16) * mm});
            skLineSegment(sketch, "E1766", {"start": v(1895.64, 362.16) * mm, "end": v(1905.9, 360.16) * mm});
            skLineSegment(sketch, "E1767", {"start": v(1905.9, 360.16) * mm, "end": v(1916.5, 357.93) * mm});
            skLineSegment(sketch, "E1768", {"start": v(1916.5, 357.93) * mm, "end": v(1927.43, 355.47) * mm});
            skLineSegment(sketch, "E1769", {"start": v(1927.43, 355.47) * mm, "end": v(1938.7, 352.75) * mm});
            skLineSegment(sketch, "E1770", {"start": v(1938.7, 352.75) * mm, "end": v(1950.3, 349.78) * mm});
            skLineSegment(sketch, "E1771", {"start": v(1950.3, 349.78) * mm, "end": v(1962.21, 346.54) * mm});
            skLineSegment(sketch, "E1772", {"start": v(1962.21, 346.54) * mm, "end": v(1974.45, 343.02) * mm});
            skLineSegment(sketch, "E1773", {"start": v(1974.45, 343.02) * mm, "end": v(1987, 339.22) * mm});
            skLineSegment(sketch, "E1774", {"start": v(1987, 339.22) * mm, "end": v(1999.84, 335.11) * mm});
            skLineSegment(sketch, "E1775", {"start": v(1999.84, 335.11) * mm, "end": v(2013, 330.7) * mm});
            skLineSegment(sketch, "E1776", {"start": v(2013, 330.7) * mm, "end": v(2026.44, 325.98) * mm});
            skLineSegment(sketch, "E1777", {"start": v(2026.44, 325.98) * mm, "end": v(2040.17, 320.92) * mm});
            skLineSegment(sketch, "E1778", {"start": v(2040.17, 320.92) * mm, "end": v(2054.18, 315.53) * mm});
            skLineSegment(sketch, "E1779", {"start": v(2054.18, 315.53) * mm, "end": v(2068.46, 309.8) * mm});
            skLineSegment(sketch, "E1780", {"start": v(2068.46, 309.8) * mm, "end": v(2083, 303.71) * mm});
            skLineSegment(sketch, "E1781", {"start": v(2083, 303.71) * mm, "end": v(2097.81, 297.26) * mm});
            skLineSegment(sketch, "E1782", {"start": v(2097.81, 297.26) * mm, "end": v(2112.87, 290.44) * mm});
            skLineSegment(sketch, "E1783", {"start": v(2112.87, 290.44) * mm, "end": v(2128.17, 283.24) * mm});
            skLineSegment(sketch, "E1784", {"start": v(2128.17, 283.24) * mm, "end": v(2143.7, 275.64) * mm});
            skLineSegment(sketch, "E1785", {"start": v(2143.7, 275.64) * mm, "end": v(2159.46, 267.66) * mm});
            skLineSegment(sketch, "E1786", {"start": v(2159.46, 267.66) * mm, "end": v(2168.79, 258.47) * mm});
            skLineSegment(sketch, "E1787", {"start": v(2168.79, 258.47) * mm, "end": v(2175.56, 193.4) * mm});
            skLineSegment(sketch, "E1788", {"start": v(2175.56, 193.4) * mm, "end": v(2168.32, 182.48) * mm});
            skLineSegment(sketch, "E1789", {"start": v(2168.32, 182.48) * mm, "end": v(2154.54, 171.42) * mm});
            skLineSegment(sketch, "E1790", {"start": v(2154.54, 171.42) * mm, "end": v(2140.9, 160.8) * mm});
            skLineSegment(sketch, "E1791", {"start": v(2140.9, 160.8) * mm, "end": v(2127.41, 150.6) * mm});
            skLineSegment(sketch, "E1792", {"start": v(2127.41, 150.6) * mm, "end": v(2114.08, 140.83) * mm});
            skLineSegment(sketch, "E1793", {"start": v(2114.08, 140.83) * mm, "end": v(2100.92, 131.47) * mm});
            skLineSegment(sketch, "E1794", {"start": v(2100.92, 131.47) * mm, "end": v(2087.94, 122.52) * mm});
            skLineSegment(sketch, "E1795", {"start": v(2087.94, 122.52) * mm, "end": v(2075.14, 113.97) * mm});
            skLineSegment(sketch, "E1796", {"start": v(2075.14, 113.97) * mm, "end": v(2062.54, 105.8) * mm});
            skLineSegment(sketch, "E1797", {"start": v(2062.54, 105.8) * mm, "end": v(2050.15, 98.04) * mm});
            skLineSegment(sketch, "E1798", {"start": v(2050.15, 98.04) * mm, "end": v(2037.96, 90.64) * mm});
            skLineSegment(sketch, "E1799", {"start": v(2037.96, 90.64) * mm, "end": v(2026, 83.62) * mm});
            skLineSegment(sketch, "E1800", {"start": v(2026, 83.62) * mm, "end": v(2014.27, 76.96) * mm});
            skLineSegment(sketch, "E1801", {"start": v(2014.27, 76.96) * mm, "end": v(2002.78, 70.66) * mm});
            skLineSegment(sketch, "E1802", {"start": v(2002.78, 70.66) * mm, "end": v(1991.53, 64.7) * mm});
            skLineSegment(sketch, "E1803", {"start": v(1991.53, 64.7) * mm, "end": v(1980.53, 59.07) * mm});
            skLineSegment(sketch, "E1804", {"start": v(1980.53, 59.07) * mm, "end": v(1969.8, 53.78) * mm});
            skLineSegment(sketch, "E1805", {"start": v(1969.8, 53.78) * mm, "end": v(1959.33, 48.8) * mm});
            skLineSegment(sketch, "E1806", {"start": v(1959.33, 48.8) * mm, "end": v(1949.14, 44.14) * mm});
            skLineSegment(sketch, "E1807", {"start": v(1949.14, 44.14) * mm, "end": v(1939.22, 39.78) * mm});
            skLineSegment(sketch, "E1808", {"start": v(1939.22, 39.78) * mm, "end": v(1929.6, 35.7) * mm});
            skLineSegment(sketch, "E1809", {"start": v(1929.6, 35.7) * mm, "end": v(1920.27, 31.92) * mm});
            skLineSegment(sketch, "E1810", {"start": v(1920.27, 31.92) * mm, "end": v(1911.24, 28.4) * mm});
            skLineSegment(sketch, "E1811", {"start": v(1911.24, 28.4) * mm, "end": v(1902.51, 25.16) * mm});
            skLineSegment(sketch, "E1812", {"start": v(1902.51, 25.16) * mm, "end": v(1894.1, 22.17) * mm});
            skLineSegment(sketch, "E1813", {"start": v(1894.1, 22.17) * mm, "end": v(1886, 19.42) * mm});
            skLineSegment(sketch, "E1814", {"start": v(1886, 19.42) * mm, "end": v(1878.23, 16.9) * mm});
            skLineSegment(sketch, "E1815", {"start": v(1878.23, 16.9) * mm, "end": v(1870.78, 14.61) * mm});
            skLineSegment(sketch, "E1816", {"start": v(1870.78, 14.61) * mm, "end": v(1863.67, 12.54) * mm});
            skLineSegment(sketch, "E1817", {"start": v(1863.67, 12.54) * mm, "end": v(1856.9, 10.67) * mm});
            skLineSegment(sketch, "E1818", {"start": v(1856.9, 10.67) * mm, "end": v(1850.46, 9) * mm});
            skLineSegment(sketch, "E1819", {"start": v(1850.46, 9) * mm, "end": v(1844.36, 7.5) * mm});
            skLineSegment(sketch, "E1820", {"start": v(1844.36, 7.5) * mm, "end": v(1838.62, 6.19) * mm});
            skLineSegment(sketch, "E1821", {"start": v(1838.62, 6.19) * mm, "end": v(1833.24, 5.03) * mm});
            skLineSegment(sketch, "E1822", {"start": v(1833.24, 5.03) * mm, "end": v(1828.2, 4.03) * mm});
            skLineSegment(sketch, "E1823", {"start": v(1828.2, 4.03) * mm, "end": v(1823.53, 3.17) * mm});
            skLineSegment(sketch, "E1824", {"start": v(67.2, 0) * mm, "end": v(-67.2, 0) * mm});
            skLineSegment(sketch, "E1825", {"start": v(0, -67.2) * mm, "end": v(0, 67.2) * mm});
            skCircle(sketch, "E1826", {"center": v(2005.3, 208.58) * mm, "radius": 65.94 * mm});
            skCircle(sketch, "E1827", {"center": v(0, 0) * mm, "radius": 2016.13 * mm, "construction": true});
            skCircle(sketch, "E1828", {"center": v(0, 0) * mm, "radius": 2184.14 * mm, "construction": true});
            skCircle(sketch, "E1829", {"center": v(0, 0) * mm, "radius": 1796.37 * mm, "construction": true});
            skSolve(sketch);
        }
        {
            var Q0;
            Q0=makeQuery(id+"F0.imprint","IMPRINT",FACE,{"disambiguationData":[TD([[makeQuery(id+"F0.imprint","IMPRINT",EDGE,{"derivedFrom":sQuery(id+"F0.wireOp",EDGE,"E0")}),-1.0]])]});
            extrude(context, id + "F1", {"entities" : qUnion([Q0]), "depth" : 50.8 * mm, "offsetDistance" : 25.4 * mm});
        }
    });
